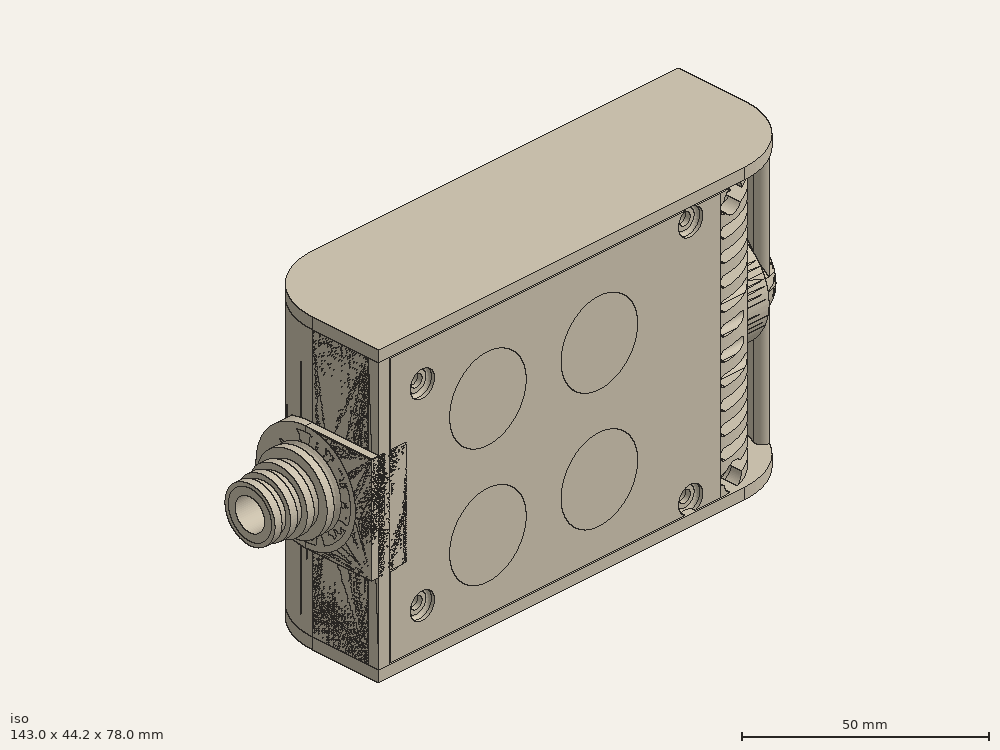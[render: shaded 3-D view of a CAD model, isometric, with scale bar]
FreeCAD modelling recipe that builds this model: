
FCSTD DOCUMENT  (FreeCAD 0.19R0.19.2)
Label: enclosure_137
License: All rights reserved
LicenseURL: http://en.wikipedia.org/wiki/All_rights_reserved
objects: Part::Feature×90, Part::Revolution×90, Part::MultiFuse×67, Sketcher::SketchObject×48, Part::Extrusion×36, Part::Cut×32, Part::Fillet×27, Part::Cylinder×26, Part::Box×19, App::MeasureDistance×4
note: 435 computed .brp shape members not serialized (recipe doc carries the construction recipe); baked Part::Feature solids carry a one-line shape summary decoded from their .brp

FEATURE [Sketcher::SketchObject] Sketch  label="topSketch"
  FullyConstrained = true
  sketch-geometry (20):
    g0: LineSegment StartX=5.21097e-06 StartY=3 StartZ=0 EndX=5.21097e-06 EndY=19 EndZ=0
    g1: ArcOfCircle CenterX=19 CenterY=19 CenterZ=0 NormalX=0 NormalY=0 NormalZ=1 AngleXU=0 Radius=19 StartAngle=1.5708 EndAngle=3.14159
    g2: ArcOfCircle CenterX=19 CenterY=19 CenterZ=0 NormalX=0 NormalY=0 NormalZ=1 AngleXU=0 Radius=16 StartAngle=1.5708 EndAngle=3.14159
    g3: LineSegment StartX=114 StartY=35 StartZ=0 EndX=19 EndY=35 EndZ=0
    g4: LineSegment StartX=5.21097e-06 StartY=3 StartZ=0 EndX=5.21097e-06 EndY=0 EndZ=0
    g5: LineSegment StartX=3 StartY=0 StartZ=0 EndX=5.21097e-06 EndY=0 EndZ=0
    g6: LineSegment StartX=3 StartY=19 StartZ=0 EndX=3 EndY=0 EndZ=0
    g7: LineSegment StartX=19 StartY=38 StartZ=0 EndX=124 EndY=38 EndZ=0
    g8: Circle CenterX=119 CenterY=35 CenterZ=0 NormalX=0 NormalY=0 NormalZ=1 AngleXU=0 Radius=1
    g9: Circle CenterX=121 CenterY=35 CenterZ=0 NormalX=0 NormalY=0 NormalZ=1 AngleXU=0 Radius=1
    g10: Circle CenterX=121 CenterY=33 CenterZ=0 NormalX=0 NormalY=0 NormalZ=1 AngleXU=0 Radius=1
    g11: BSplineCurve PolesCount=3 KnotsCount=2 Degree=2 IsPeriodic=0
    g12: GeomPoint X=119 Y=35 Z=0
    g13: GeomPoint X=121 Y=33 Z=0
    g14: LineSegment StartX=119 StartY=35 StartZ=0 EndX=114 EndY=35 EndZ=0
    g15: ArcOfCircle CenterX=105 CenterY=19 CenterZ=0 NormalX=0 NormalY=0 NormalZ=1 AngleXU=0 Radius=19 StartAngle=5.7297 EndAngle=6.28319
    g16: ArcOfCircle CenterX=105 CenterY=19 CenterZ=0 NormalX=0 NormalY=0 NormalZ=1 AngleXU=0 Radius=16 StartAngle=5.60905 EndAngle=6.28319
    g17: LineSegment StartX=121 StartY=33 StartZ=0 EndX=121 EndY=19 EndZ=0
    g18: LineSegment StartX=124 StartY=38 StartZ=0 EndX=124 EndY=19 EndZ=0
    g19: LineSegment StartX=117.5 StartY=9.01251 StartZ=0 EndX=121.163 EndY=9.0125 EndZ=0
  constraints (46):
    c: Vertical(g0)
    c: Block(g0)
    c: Coincident(g1,g0)
    c: Block(g1)
    c: Coincident(g2,g1)
    c: Block(g2)
    c: Coincident(g3,g2)
    c: Horizontal(g3)
    c: Tangent(g3,g2)
    c: Coincident(g4,g0)
    c: Distance(g4) = 3
    c: Vertical(g4)
    c: Coincident(g5,g4)
    c: Horizontal(g5)
    c: Coincident(g6,g2)
    c: Coincident(g6,g5)
    c: Vertical(g6)
    c: Horizontal(g7)
    c: Distance(g7) = 105
    c: Coincident(g7,g1)
    c: Block(g3)
    c: Weight(g8) = 1
    c: Equal(g8,g9)
    c: Equal(g8,g10)
    c: InternalAlignment(g8,g11)
    c: InternalAlignment(g9,g11)
    c: InternalAlignment(g10,g11)
    c: InternalAlignment(g12,g11)
    c: InternalAlignment(g13,g11)
    c: Block(g11)
    c: Coincident(g14,g11)
    c: Coincident(g14,g3)
    c: Horizontal(g14)
    c: Block(g15)
    c: Coincident(g16,g15)
    c: Block(g16)
    c: Coincident(g17,g11)
    c: Coincident(g17,g16)
    c: Vertical(g17)
    c: Distance(g17) = 14
    c: Coincident(g18,g7)
    c: Coincident(g18,g15)
    c: Vertical(g18)
    c: Distance(g18) = 19
    c: Coincident(g19,g16)
    c: Coincident(g19,g15)
FEATURE [Sketcher::SketchObject] Sketch001  label="bottomSketch"
  FullyConstrained = true
  sketch-geometry (32):
    g0: LineSegment StartX=3.3 StartY=-6.03275e-07 StartZ=0 EndX=98 EndY=-6.03275e-07 EndZ=0
    g1: ArcOfCircle CenterX=98 CenterY=19 CenterZ=0 NormalX=0 NormalY=0 NormalZ=1 AngleXU=0 Radius=19 StartAngle=4.71239 EndAngle=5.71103
    g2: LineSegment StartX=6.3 StartY=8 StartZ=0 EndX=3.3 EndY=8 EndZ=0
    g3: LineSegment StartX=3.3 StartY=8 StartZ=0 EndX=3.3 EndY=-6.03275e-07 EndZ=0
    g4: ArcOfCircle CenterX=8.3 CenterY=5 CenterZ=0 NormalX=0 NormalY=0 NormalZ=1 AngleXU=0 Radius=2 StartAngle=3.14159 EndAngle=4.71239
    g5: LineSegment StartX=6.3 StartY=8 StartZ=0 EndX=6.3 EndY=5 EndZ=0
    g6: ArcOfCircle CenterX=98 CenterY=19 CenterZ=0 NormalX=0 NormalY=0 NormalZ=1 AngleXU=0 Radius=12.7 StartAngle=4.71239 EndAngle=6.28319
    g7: LineSegment StartX=94.7 StartY=3 StartZ=0 EndX=8.3 EndY=3 EndZ=0
    g8-g12: Circle x5 (B-spline internal-alignment scaffolding for g13; pole/knot coordinates omitted)
    g13: BSplineCurve PolesCount=5 KnotsCount=3 Degree=3 IsPeriodic=0
    g14: GeomPoint X=98 Y=6.3 Z=0
    g15: GeomPoint X=96.3938 Y=4.71946 Z=0
    g16: GeomPoint X=94.7 Y=3 Z=0
    g17-g23: Circle x7 (B-spline internal-alignment scaffolding for g24; pole/knot coordinates omitted)
    g24: BSplineCurve PolesCount=7 KnotsCount=5 Degree=3 IsPeriodic=0
    g25-g29: GeomPoint x5 (B-spline internal-alignment scaffolding for g24; pole/knot coordinates omitted)
    g30: ArcOfCircle CenterX=98 CenterY=19 CenterZ=0 NormalX=0 NormalY=0 NormalZ=1 AngleXU=0 Radius=15.7 StartAngle=5.81226 EndAngle=6.28319
    g31: LineSegment StartX=110.7 StartY=19 StartZ=0 EndX=113.7 EndY=19 EndZ=0
  constraints (41):
    c: Horizontal(g0)
    c: Coincident(g1,g0)
    c: Block(g1)
    c: Horizontal(g2)
    c: Distance(g2) = 3
    c: Coincident(g3,g2)
    c: Vertical(g3)
    c: Coincident(g3,g0)
    c: Block(g4)
    c: Block(g2)
    c: Coincident(g5,g2)
    c: Coincident(g5,g4)
    c: Vertical(g5)
    c: Coincident(g6,g1)
    c: Block(g6)
    c: Coincident(g7,g4)
    c: Horizontal(g7)
    c: Block(g0)
    c: Block(g7)
    c: Block(g3)
    c: Coincident(g13,g6)
    c: Weight(g8) = 1
    c: Equal(g8, g9-g12) x4
    c: Coincident(g13,g7)
    c: InternalAlignment(g8-g12 -> g13) x5
    c: InternalAlignment(g14,g13)
    c: InternalAlignment(g15,g13)
    c: InternalAlignment(g16,g13)
    c: Block(g13)
    c: Weight(g17) = 1
    c: Equal(g17, g18-g23) x6
    c: Coincident(g24,g1)
    c: InternalAlignment(g17-g23 -> g24) x7
    c: InternalAlignment(g25-g29 -> g24) x5
    c: Block(g24)
    c: Coincident(g30,g24)
    c: Coincident(g31,g6)
    c: Coincident(g31,g30)
    c: Horizontal(g31)
    c: Block(g31)
    c: Block(g30)
FEATURE [Part::Extrusion] Extrude  label="top"
  Base = -> Sketch
  Dir = (0,0,1)
  DirMode = 2
  FaceMakerClass = Part::FaceMakerBullseye
  LengthFwd = 72
  LengthRev = 0
  Solid = true
  Symmetric = false
FEATURE [Part::Extrusion] Extrude001  label="bottom"
  Base = -> Sketch001
  Dir = (0,0,1)
  DirMode = 2
  FaceMakerClass = Part::FaceMakerBullseye
  LengthFwd = 71.4
  LengthRev = 0
  Placement = pos=(0,0,0.3) rot=(0,0,1;0rad)
  Solid = true
  Symmetric = false
FEATURE [Sketcher::SketchObject] Sketch002  label="topSketch001"
  FullyConstrained = true
  sketch-geometry (6):
    g0: ArcOfCircle CenterX=19 CenterY=19 CenterZ=0 NormalX=0 NormalY=0 NormalZ=1 AngleXU=0 Radius=19 StartAngle=1.5708 EndAngle=3.14159
    g1: LineSegment StartX=5.22862e-06 StartY=19 StartZ=0 EndX=5.22862e-06 EndY=1.19904e-11 EndZ=0
    g2: LineSegment StartX=19 StartY=38 StartZ=0 EndX=124 EndY=38 EndZ=0
    g3: LineSegment StartX=5.22862e-06 StartY=1.19904e-11 StartZ=0 EndX=105 EndY=1.19904e-11 EndZ=0
    g4: ArcOfCircle CenterX=105 CenterY=19 CenterZ=0 NormalX=0 NormalY=0 NormalZ=1 AngleXU=0 Radius=19 StartAngle=4.71239 EndAngle=6.28319
    g5: LineSegment StartX=124 StartY=38 StartZ=0 EndX=124 EndY=19 EndZ=0
  constraints (16):
    c: Block(g0)
    c: Coincident(g1,g0)
    c: Vertical(g1)
    c: Horizontal(g2)
    c: Distance(g2) = 105
    c: Coincident(g2,g0)
    c: Distance(g1) = 19
    c: Coincident(g3,g1)
    c: Horizontal(g3)
    c: Distance(g3) = 105
    c: Block(g4)
    c: Coincident(g4,g3)
    c: Coincident(g5,g2)
    c: Coincident(g5,g4)
    c: Vertical(g5)
    c: Distance(g5) = 19
FEATURE [Part::Extrusion] Extrude002  label="sideA"
  Base = -> Sketch002
  Dir = (0,0,1)
  DirMode = 2
  FaceMakerClass = Part::FaceMakerBullseye
  LengthFwd = 3
  LengthRev = 0
  Placement = pos=(0,0,-3) rot=(0,0,1;0rad)
  Solid = true
  Symmetric = false
FEATURE [Sketcher::SketchObject] Sketch003  label="topSketch002"
  FullyConstrained = true
  sketch-geometry (6):
    g0: LineSegment StartX=19 StartY=38 StartZ=0 EndX=117 EndY=38 EndZ=0
    g1: ArcOfCircle CenterX=19 CenterY=19 CenterZ=0 NormalX=0 NormalY=0 NormalZ=1 AngleXU=0 Radius=19 StartAngle=1.5708 EndAngle=3.14159
    g2: LineSegment StartX=117 StartY=38 StartZ=0 EndX=117 EndY=19 EndZ=0
    g3: LineSegment StartX=98 StartY=1.0161e-12 StartZ=0 EndX=5.22862e-06 EndY=1.0161e-12 EndZ=0
    g4: LineSegment StartX=5.22862e-06 StartY=19 StartZ=0 EndX=5.22862e-06 EndY=1.0161e-12 EndZ=0
    g5: ArcOfCircle CenterX=98 CenterY=19 CenterZ=0 NormalX=0 NormalY=0 NormalZ=1 AngleXU=0 Radius=19 StartAngle=4.71239 EndAngle=6.28319
  constraints (16):
    c: Horizontal(g0)
    c: Distance(g0) = 98
    c: Coincident(g1,g0)
    c: Block(g1)
    c: Coincident(g2,g0)
    c: Vertical(g2)
    c: Distance(g2) = 19
    c: Horizontal(g3)
    c: Coincident(g4,g1)
    c: Vertical(g4)
    c: Coincident(g3,g4)
    c: Block(g3)
    c: Coincident(g5,g2)
    c: Coincident(g5,g3)
    c: Block(g0)
    c: Block(g5)
FEATURE [Sketcher::SketchObject] Sketch004
  FullyConstrained = true
  MapMode = 3
  Placement = pos=(0,0,0) rot=(1,0,0;1.5708rad)
  Support = -> [Extrude]
  sketch-geometry (8):
    g0: Circle CenterX=80.351 CenterY=-67.6202 CenterZ=0 NormalX=0 NormalY=0 NormalZ=1 AngleXU=0 Radius=2
    g1: Circle CenterX=80.351 CenterY=-67.6202 CenterZ=0 NormalX=0 NormalY=0 NormalZ=1 AngleXU=0 Radius=3
    g2: Circle CenterX=80.351 CenterY=-4.92017 CenterZ=0 NormalX=0 NormalY=0 NormalZ=1 AngleXU=0 Radius=2
    g3: Circle CenterX=80.351 CenterY=-4.92017 CenterZ=0 NormalX=0 NormalY=0 NormalZ=1 AngleXU=0 Radius=3
    g4: Circle CenterX=23.851 CenterY=-4.92017 CenterZ=0 NormalX=0 NormalY=0 NormalZ=1 AngleXU=0 Radius=2
    g5: Circle CenterX=23.851 CenterY=-4.92017 CenterZ=0 NormalX=0 NormalY=0 NormalZ=1 AngleXU=0 Radius=3
    g6: Circle CenterX=23.851 CenterY=-67.6202 CenterZ=0 NormalX=0 NormalY=0 NormalZ=1 AngleXU=0 Radius=2
    g7: Circle CenterX=23.851 CenterY=-67.6202 CenterZ=0 NormalX=0 NormalY=0 NormalZ=1 AngleXU=0 Radius=3
  constraints (8):
    c: Block(g3)
    c: Block(g2)
    c: Block(g1)
    c: Block(g0)
    c: Block(g6)
    c: Block(g7)
    c: Block(g4)
    c: Block(g5)
FEATURE [Part::Extrusion] Extrude004
  Base = -> Sketch004
  Dir = (0,-1,2e-16)
  DirMode = 2
  FaceMakerClass = Part::FaceMakerBullseye
  LengthFwd = 6
  LengthRev = 0
  Placement = pos=(0,9,0) rot=(0,0,1;0rad)
  Solid = true
  Symmetric = false
FEATURE [Sketcher::SketchObject] Sketch005
  FullyConstrained = true
  MapMode = 3
  Placement = pos=(0,0,0) rot=(1,0,0;1.5708rad)
  Support = -> [Extrude]
  sketch-geometry (8):
    g0: Circle CenterX=80.351 CenterY=-67.6202 CenterZ=0 NormalX=0 NormalY=0 NormalZ=1 AngleXU=0 Radius=3
    g1: Circle CenterX=80.351 CenterY=-4.92017 CenterZ=0 NormalX=0 NormalY=0 NormalZ=1 AngleXU=0 Radius=3
    g2: Circle CenterX=23.851 CenterY=-4.92017 CenterZ=0 NormalX=0 NormalY=0 NormalZ=1 AngleXU=0 Radius=3
    g3: Circle CenterX=23.851 CenterY=-67.6202 CenterZ=0 NormalX=0 NormalY=0 NormalZ=1 AngleXU=0 Radius=3
    g4: Circle CenterX=23.851 CenterY=-67.6202 CenterZ=0 NormalX=0 NormalY=0 NormalZ=1 AngleXU=0 Radius=5
    g5: Circle CenterX=80.351 CenterY=-67.6202 CenterZ=0 NormalX=0 NormalY=0 NormalZ=1 AngleXU=0 Radius=5
    g6: Circle CenterX=23.851 CenterY=-4.92017 CenterZ=0 NormalX=0 NormalY=0 NormalZ=1 AngleXU=0 Radius=5
    g7: Circle CenterX=80.351 CenterY=-4.92017 CenterZ=0 NormalX=0 NormalY=0 NormalZ=1 AngleXU=0 Radius=5
  constraints (8):
    c: Block(g1)
    c: Block(g0)
    c: Block(g3)
    c: Block(g2)
    c: Block(g5)
    c: Block(g4)
    c: Block(g6)
    c: Block(g7)
FEATURE [Part::Extrusion] Extrude005
  Base = -> Sketch005
  Dir = (0,-1,2e-16)
  DirMode = 2
  FaceMakerClass = Part::FaceMakerBullseye
  LengthFwd = 2
  LengthRev = 0
  Solid = true
  Symmetric = false
FEATURE [Sketcher::SketchObject] Sketch006
  FullyConstrained = true
  MapMode = 3
  Placement = pos=(0,0,0) rot=(1,0,0;1.5708rad)
  sketch-geometry (8):
    g0: Circle CenterX=80.351 CenterY=-67.6202 CenterZ=0 NormalX=0 NormalY=0 NormalZ=1 AngleXU=0 Radius=3
    g1: Circle CenterX=80.351 CenterY=-4.92017 CenterZ=0 NormalX=0 NormalY=0 NormalZ=1 AngleXU=0 Radius=3
    g2: Circle CenterX=23.851 CenterY=-4.92017 CenterZ=0 NormalX=0 NormalY=0 NormalZ=1 AngleXU=0 Radius=3
    g3: Circle CenterX=23.851 CenterY=-67.6202 CenterZ=0 NormalX=0 NormalY=0 NormalZ=1 AngleXU=0 Radius=3
    g4: Circle CenterX=23.851 CenterY=-67.6202 CenterZ=0 NormalX=0 NormalY=0 NormalZ=1 AngleXU=0 Radius=5
    g5: Circle CenterX=80.351 CenterY=-67.6202 CenterZ=0 NormalX=0 NormalY=0 NormalZ=1 AngleXU=0 Radius=5
    g6: Circle CenterX=23.851 CenterY=-4.92017 CenterZ=0 NormalX=0 NormalY=0 NormalZ=1 AngleXU=0 Radius=5
    g7: Circle CenterX=80.351 CenterY=-4.92017 CenterZ=0 NormalX=0 NormalY=0 NormalZ=1 AngleXU=0 Radius=5
  constraints (8):
    c: Block(g1)
    c: Block(g0)
    c: Block(g3)
    c: Block(g2)
    c: Block(g5)
    c: Block(g4)
    c: Block(g6)
    c: Block(g7)
FEATURE [Part::Extrusion] Extrude007
  Base = -> Sketch006
  Dir = (0,-1,2e-16)
  DirMode = 2
  FaceMakerClass = Part::FaceMakerBullseye
  LengthFwd = 2
  LengthRev = 0
  Solid = true
  Symmetric = false
FEATURE [Part::Fillet] Fillet
  Base = -> Extrude007
  Edges = 4 edges r=1.99: [Edge6,Edge12,Edge18,Edge24]
FEATURE [Part::Cut] Cut
  Base = -> Extrude005
  Placement = pos=(0,5,0) rot=(0,0,1;0rad)
  Tool = -> Fillet
FEATURE [Part::MultiFuse] Fusion  label="pCBScrews"
  Placement = pos=(-2.5,0,72.3) rot=(0,0,1;0rad)
  Shapes = -> [Extrude004,Cut]
FEATURE [App::MeasureDistance] Distance  label="Distance: 0.69 mm"
  Distance = 0.685967
  P1 = (24.0138,2.9647,0.3)
  P2 = (23.8901,3,-0.373787)
FEATURE [App::MeasureDistance] Distance001  label="Distance: 0.53 mm"
  Distance = 0.533607
  P1 = (80.2939,3,72.2334)
  P2 = (80.281,2.99661,71.7)
FEATURE [Part::Fillet] Fillet001
  Base = -> Extrude001
  Edges = 1 edges r=2.4: [Edge17]
FEATURE [Part::Fillet] Fillet002  label="bottom001"
  Base = -> Fillet001
  Edges = 1 edges r=2.4: [Edge36]
FEATURE [Part::Fillet] Fillet003  label="top001"
  Base = -> Extrude
  Edges = 1 edges r=2: [Edge1]
FEATURE [Sketcher::SketchObject] Sketch007
  FullyConstrained = true
  sketch-geometry (16):
    g0: LineSegment StartX=4 StartY=0 StartZ=0 EndX=4 EndY=2.4 EndZ=0
    g1: LineSegment StartX=4 StartY=2.4 StartZ=0 EndX=7 EndY=2.4 EndZ=0
    g2: LineSegment StartX=4 StartY=0 StartZ=0 EndX=5.7 EndY=0 EndZ=0
    g3: LineSegment StartX=5.7 StartY=0 StartZ=0 EndX=5.7 EndY=-5.6 EndZ=0
    g4-g8: Circle x5 (B-spline internal-alignment scaffolding for g9; pole/knot coordinates omitted)
    g9: BSplineCurve PolesCount=5 KnotsCount=3 Degree=3 IsPeriodic=0
    g10: GeomPoint X=7 Y=2.4 Z=0
    g11: GeomPoint X=10.4582 Y=-1.55472 Z=0
    g12: GeomPoint X=14 Y=-5.6 Z=0
    g13: LineSegment StartX=14 StartY=-5.6 StartZ=0 EndX=14 EndY=-14.1 EndZ=0
    g14: LineSegment StartX=14 StartY=-14.1 StartZ=0 EndX=6.5 EndY=-14.1 EndZ=0
    g15: LineSegment StartX=5.7 StartY=-5.6 StartZ=0 EndX=6.5 EndY=-14.1 EndZ=0
  constraints (28):
    c: Distance(g0) = 2.4
    c: Vertical(g0)
    c: Block(g0)
    c: Coincident(g1,g0)
    c: Horizontal(g1)
    c: Distance(g1) = 3
    c: Coincident(g2,g0)
    c: Horizontal(g2)
    c: Distance(g2) = 1.7
    c: Coincident(g3,g2)
    c: Vertical(g3)
    c: Distance(g3) = 5.6
    c: Coincident(g9,g1)
    c: Weight(g4) = 1
    c: Equal(g4, g5-g8) x4
    c: InternalAlignment(g4-g8 -> g9) x5
    c: InternalAlignment(g10,g9)
    c: InternalAlignment(g11,g9)
    c: InternalAlignment(g12,g9)
    c: Block(g9)
    c: Coincident(g13,g9)
    c: Vertical(g13)
    c: Distance(g13) = 8.5
    c: Coincident(g14,g13)
    c: Horizontal(g14)
    c: Distance(g14) = 7.5
    c: Coincident(g15,g3)
    c: Coincident(g15,g14)
FEATURE [Part::Feature] Face
  shape: bbox 10 x 16.5 x 2e-07 mm, 1 faces, 0 solids (baked)
FEATURE [Part::Revolution] Revolve  label="plugHousing"
  Angle = 360
  Axis = (0,1,0)
  Base = (0,0,0)
  FaceMakerClass = Part::FaceMakerBullseye
  Placement = pos=(0,0,36.15) rot=(0,0,1;0rad)
  Solid = false
  Source = -> Face
  Symmetric = false
FEATURE [Part::Feature] Face001
  shape: bbox 10 x 16.5 x 2e-07 mm, 1 faces, 0 solids (baked)
FEATURE [Part::Revolution] Revolve001  label="plugHousing001"
  Angle = 360
  Axis = (0,1,0)
  Base = (0,0,0)
  FaceMakerClass = Part::FaceMakerBullseye
  Placement = pos=(0,0,36.15) rot=(0,0,1;0rad)
  Solid = false
  Source = -> Face001
  Symmetric = false
FEATURE [Part::MultiFuse] Fusion001  label="plugHousing002"
  Placement = pos=(0,0,0) rot=(0,0,1;1.5708rad)
  Shapes = -> [Revolve001,Revolve]
FEATURE [Part::Feature] Face002
  shape: bbox 10 x 16.5 x 2e-07 mm, 1 faces, 0 solids (baked)
FEATURE [Part::Revolution] Revolve003  label="plugHousing005"
  Angle = 360
  Axis = (0,1,0)
  Base = (0,0,0)
  FaceMakerClass = Part::FaceMakerBullseye
  Placement = pos=(0,0,36.15) rot=(0,0,1;0rad)
  Solid = false
  Source = -> Face002
  Symmetric = false
FEATURE [Part::Feature] Face003
  shape: bbox 10 x 16.5 x 2e-07 mm, 1 faces, 0 solids (baked)
FEATURE [Part::Revolution] Revolve002  label="plugHousing003"
  Angle = 360
  Axis = (0,1,0)
  Base = (0,0,0)
  FaceMakerClass = Part::FaceMakerBullseye
  Placement = pos=(0,0,36.15) rot=(0,0,1;0rad)
  Solid = false
  Source = -> Face003
  Symmetric = false
FEATURE [Part::MultiFuse] Fusion002  label="plugHousing004"
  Placement = pos=(0,0,0) rot=(0,0,1;1.5708rad)
  Shapes = -> [Revolve002,Revolve003]
FEATURE [Part::MultiFuse] Fusion003  label="plugHousing006"
  Placement = pos=(0,19,0) rot=(0,0,1;3.14159rad)
  Shapes = -> [Fusion002,Fusion001]
FEATURE [Part::Feature] Face004
  shape: bbox 10 x 16.5 x 2e-07 mm, 1 faces, 0 solids (baked)
FEATURE [Part::Revolution] Revolve006  label="plugHousing010"
  Angle = 360
  Axis = (0,1,0)
  Base = (0,0,0)
  FaceMakerClass = Part::FaceMakerBullseye
  Placement = pos=(0,0,36.15) rot=(0,0,1;0rad)
  Solid = false
  Source = -> Face004
  Symmetric = false
FEATURE [Part::Feature] Face005
  shape: bbox 10 x 16.5 x 2e-07 mm, 1 faces, 0 solids (baked)
FEATURE [Part::Revolution] Revolve007  label="plugHousing011"
  Angle = 360
  Axis = (0,1,0)
  Base = (0,0,0)
  FaceMakerClass = Part::FaceMakerBullseye
  Placement = pos=(0,0,36.15) rot=(0,0,1;0rad)
  Solid = false
  Source = -> Face005
  Symmetric = false
FEATURE [Part::Feature] Face006
  shape: bbox 10 x 16.5 x 2e-07 mm, 1 faces, 0 solids (baked)
FEATURE [Part::Revolution] Revolve004  label="plugHousing007"
  Angle = 360
  Axis = (0,1,0)
  Base = (0,0,0)
  FaceMakerClass = Part::FaceMakerBullseye
  Placement = pos=(0,0,36.15) rot=(0,0,1;0rad)
  Solid = false
  Source = -> Face006
  Symmetric = false
FEATURE [Part::MultiFuse] Fusion004  label="plugHousing009"
  Placement = pos=(0,0,0) rot=(0,0,1;1.5708rad)
  Shapes = -> [Revolve004,Revolve007]
FEATURE [Part::Feature] Face007
  shape: bbox 10 x 16.5 x 2e-07 mm, 1 faces, 0 solids (baked)
FEATURE [Part::Revolution] Revolve005  label="plugHousing008"
  Angle = 360
  Axis = (0,1,0)
  Base = (0,0,0)
  FaceMakerClass = Part::FaceMakerBullseye
  Placement = pos=(0,0,36.15) rot=(0,0,1;0rad)
  Solid = false
  Source = -> Face007
  Symmetric = false
FEATURE [Part::MultiFuse] Fusion005  label="plugHousing012"
  Placement = pos=(0,0,0) rot=(0,0,1;1.5708rad)
  Shapes = -> [Revolve006,Revolve005]
FEATURE [Part::MultiFuse] Fusion006  label="plugHousing013"
  Placement = pos=(0,19,0) rot=(0,0,1;3.14159rad)
  Shapes = -> [Fusion005,Fusion004]
FEATURE [Part::MultiFuse] Fusion007  label="plugHousing014"
  Placement = pos=(122.621,0,-0.15) rot=(0,0,1;0rad)
  Shapes = -> [Fusion003,Fusion006]
FEATURE [Part::Cylinder] Cylinder002
  Angle = 360
  AttacherType = Attacher::AttachEngine3D
  Height = 20
  Placement = pos=(0,0,36.15) rot=(0,0,1;0rad)
  Radius = 4
FEATURE [Part::Cylinder] Cylinder003
  Angle = 360
  AttacherType = Attacher::AttachEngine3D
  Height = 10
  Placement = pos=(0,0,36.15) rot=(0,0,1;0rad)
  Radius = 4
FEATURE [Part::MultiFuse] Fusion009  label="removeToCreateHoleForPlugHousing"
  Placement = pos=(70,19,36.15) rot=(0,1,0;1.5708rad)
  Shapes = -> [Cylinder002,Cylinder003]
FEATURE [Part::Cylinder] Cylinder004
  Angle = 360
  AttacherType = Attacher::AttachEngine3D
  Height = 20
  Placement = pos=(0,0,36.15) rot=(0,0,1;0rad)
  Radius = 4
FEATURE [Part::Cylinder] Cylinder005
  Angle = 360
  AttacherType = Attacher::AttachEngine3D
  Height = 10
  Placement = pos=(0,0,36.15) rot=(0,0,1;0rad)
  Radius = 4
FEATURE [Part::MultiFuse] Fusion010  label="removeToCreateHoleForPlugHousing001"
  Placement = pos=(70,19,36.15) rot=(0,1,0;1.5708rad)
  Shapes = -> [Cylinder004,Cylinder005]
FEATURE [Part::Cut] Cut001
  Base = -> Fillet003
  Tool = -> Fusion010
FEATURE [Part::Cut] Cut002  label="Bottom"
  Base = -> Fillet002
  Tool = -> Fusion009
FEATURE [Part::Feature] Face008
  shape: bbox 10 x 16.5 x 2e-07 mm, 1 faces, 0 solids (baked)
FEATURE [Part::Revolution] Revolve011  label="plugHousing021"
  Angle = 360
  Axis = (0,1,0)
  Base = (0,0,0)
  FaceMakerClass = Part::FaceMakerBullseye
  Placement = pos=(0,0,36.15) rot=(0,0,1;0rad)
  Solid = false
  Source = -> Face008
  Symmetric = false
FEATURE [Part::Feature] Face009
  shape: bbox 10 x 16.5 x 2e-07 mm, 1 faces, 0 solids (baked)
FEATURE [Part::Revolution] Revolve012  label="plugHousing022"
  Angle = 360
  Axis = (0,1,0)
  Base = (0,0,0)
  FaceMakerClass = Part::FaceMakerBullseye
  Placement = pos=(0,0,36.15) rot=(0,0,1;0rad)
  Solid = false
  Source = -> Face009
  Symmetric = false
FEATURE [Part::Feature] Face010 .. Face013  x4 (patterned run collapsed; names and placements below)
  shape: bbox 10 x 16.5 x 2e-07 mm, 1 faces, 0 solids (baked)
FEATURE [Part::Revolution] Revolve015  label="plugHousing027"
  Angle = 360
  Axis = (0,1,0)
  Base = (0,0,0)
  FaceMakerClass = Part::FaceMakerBullseye
  Placement = pos=(0,0,36.15) rot=(0,0,1;0rad)
  Solid = false
  Source = -> Face013
  Symmetric = false
FEATURE [Part::Feature] Face014
  shape: bbox 10 x 16.5 x 2e-07 mm, 1 faces, 0 solids (baked)
FEATURE [Part::Feature] Face015
  shape: bbox 10 x 16.5 x 2e-07 mm, 1 faces, 0 solids (baked)
FEATURE [Part::Feature] Face016
  shape: bbox 10 x 16.5 x 2e-07 mm, 1 faces, 0 solids (baked)
FEATURE [Part::Revolution] Revolve019  label="plugHousing033"
  Angle = 360
  Axis = (0,1,0)
  Base = (0,0,0)
  FaceMakerClass = Part::FaceMakerBullseye
  Placement = pos=(0,0,36.15) rot=(0,0,1;0rad)
  Solid = false
  Source = -> Face016
  Symmetric = false
FEATURE [Part::Feature] Face017
  shape: bbox 10 x 16.5 x 2e-07 mm, 1 faces, 0 solids (baked)
FEATURE [Part::Revolution] Revolve020  label="plugHousing034"
  Angle = 360
  Axis = (0,1,0)
  Base = (0,0,0)
  FaceMakerClass = Part::FaceMakerBullseye
  Placement = pos=(0,0,36.15) rot=(0,0,1;0rad)
  Solid = false
  Source = -> Face017
  Symmetric = false
FEATURE [Part::Feature] Face018
  shape: bbox 10 x 16.5 x 2e-07 mm, 1 faces, 0 solids (baked)
FEATURE [Part::Revolution] Revolve016  label="plugHousing030"
  Angle = 360
  Axis = (0,1,0)
  Base = (0,0,0)
  FaceMakerClass = Part::FaceMakerBullseye
  Placement = pos=(0,0,36.15) rot=(0,0,1;0rad)
  Solid = false
  Source = -> Face018
  Symmetric = false
FEATURE [Part::MultiFuse] Fusion020  label="plugHousing038"
  Placement = pos=(0,0,0) rot=(0,0,1;1.5708rad)
  Shapes = -> [Revolve016,Revolve020]
FEATURE [Part::Feature] Face019
  shape: bbox 10 x 16.5 x 2e-07 mm, 1 faces, 0 solids (baked)
FEATURE [Part::Feature] Face020
  shape: bbox 10 x 16.5 x 2e-07 mm, 1 faces, 0 solids (baked)
FEATURE [Part::Revolution] Revolve017  label="plugHousing031"
  Angle = 360
  Axis = (0,1,0)
  Base = (0,0,0)
  FaceMakerClass = Part::FaceMakerBullseye
  Placement = pos=(0,0,36.15) rot=(0,0,1;0rad)
  Solid = false
  Source = -> Face020
  Symmetric = false
FEATURE [Part::MultiFuse] Fusion021  label="plugHousing039"
  Placement = pos=(0,0,0) rot=(0,0,1;1.5708rad)
  Shapes = -> [Revolve019,Revolve017]
FEATURE [Part::MultiFuse] Fusion023  label="plugHousing041"
  Placement = pos=(0,19,0) rot=(0,0,1;3.14159rad)
  Shapes = -> [Fusion021,Fusion020]
FEATURE [Part::Revolution] Revolve022  label="plugHousing043"
  Angle = 360
  Axis = (0,1,0)
  Base = (0,0,0)
  FaceMakerClass = Part::FaceMakerBullseye
  Placement = pos=(0,0,36.15) rot=(0,0,1;0rad)
  Solid = false
  Source = -> Face019
  Symmetric = false
FEATURE [Part::Feature] Face021
  shape: bbox 10 x 16.5 x 2e-07 mm, 1 faces, 0 solids (baked)
FEATURE [Part::Revolution] Revolve023  label="plugHousing044"
  Angle = 360
  Axis = (0,1,0)
  Base = (0,0,0)
  FaceMakerClass = Part::FaceMakerBullseye
  Placement = pos=(0,0,36.15) rot=(0,0,1;0rad)
  Solid = false
  Source = -> Face021
  Symmetric = false
FEATURE [Part::Feature] Face022
  shape: bbox 10 x 16.5 x 2e-07 mm, 1 faces, 0 solids (baked)
FEATURE [Part::Revolution] Revolve018  label="plugHousing032"
  Angle = 360
  Axis = (0,1,0)
  Base = (0,0,0)
  FaceMakerClass = Part::FaceMakerBullseye
  Placement = pos=(0,0,36.15) rot=(0,0,1;0rad)
  Solid = false
  Source = -> Face022
  Symmetric = false
FEATURE [Part::MultiFuse] Fusion022  label="plugHousing040"
  Placement = pos=(0,0,0) rot=(0,0,1;1.5708rad)
  Shapes = -> [Revolve018,Revolve023]
FEATURE [Part::Feature] Face023
  shape: bbox 10 x 16.5 x 2e-07 mm, 1 faces, 0 solids (baked)
FEATURE [Part::Revolution] Revolve021  label="plugHousing035"
  Angle = 360
  Axis = (0,1,0)
  Base = (0,0,0)
  FaceMakerClass = Part::FaceMakerBullseye
  Placement = pos=(0,0,36.15) rot=(0,0,1;0rad)
  Solid = false
  Source = -> Face023
  Symmetric = false
FEATURE [Part::MultiFuse] Fusion018  label="plugHousing036"
  Placement = pos=(0,0,0) rot=(0,0,1;1.5708rad)
  Shapes = -> [Revolve022,Revolve021]
FEATURE [Part::MultiFuse] Fusion019  label="plugHousing037"
  Placement = pos=(0,19,0) rot=(0,0,1;3.14159rad)
  Shapes = -> [Fusion018,Fusion022]
FEATURE [Part::MultiFuse] Fusion024  label="plugHousing042"
  Placement = pos=(122.621,0,-0.15) rot=(0,0,1;0rad)
  Shapes = -> [Fusion023,Fusion019]
FEATURE [Part::Cylinder] Cylinder006
  Angle = 360
  AttacherType = Attacher::AttachEngine3D
  Height = 20
  Placement = pos=(0,0,36.15) rot=(0,0,1;0rad)
  Radius = 14.3
FEATURE [Part::Cylinder] Cylinder007
  Angle = 360
  AttacherType = Attacher::AttachEngine3D
  Height = 10
  Placement = pos=(0,0,36.15) rot=(0,0,1;0rad)
  Radius = 4
FEATURE [Part::MultiFuse] Fusion026  label="removeToCreteHoleForPlugHousing"
  Placement = pos=(70,19,36) rot=(0,1,0;1.5708rad)
  Shapes = -> [Cylinder006,Cylinder007]
FEATURE [Part::Box] Box001  label="Cube001"
  AttacherType = Attacher::AttachEngine3D
  Height = 28
  Length = 3
  Placement = pos=(110.7,19,22) rot=(0,0,1;0rad)
  Width = 15.7
FEATURE [Part::Cut] Cut003  label="top002"
  Base = -> Cut001
  Tool = -> Fusion007
FEATURE [Part::Revolution] Revolve008  label="plugHousing015"
  Angle = 360
  Axis = (0,1,0)
  Base = (0,0,0)
  FaceMakerClass = Part::FaceMakerBullseye
  Placement = pos=(0,0,36.15) rot=(0,0,1;0rad)
  Solid = false
  Source = -> Face010
  Symmetric = false
FEATURE [Part::MultiFuse] Fusion013  label="plugHousing020"
  Placement = pos=(0,0,0) rot=(0,0,1;1.5708rad)
  Shapes = -> [Revolve008,Revolve012]
FEATURE [Part::Cut] Cut004  label="top003"
  Base = -> Cut003
  Placement = pos=(1,0,0) rot=(0,0,1;0rad)
  Tool = -> Fusion026
FEATURE [Part::Cylinder] Cylinder008
  Angle = 360
  AttacherType = Attacher::AttachEngine3D
  Height = 20
  Placement = pos=(0,0,36.15) rot=(0,0,1;0rad)
  Radius = 10.3
FEATURE [Part::Cylinder] Cylinder009
  Angle = 360
  AttacherType = Attacher::AttachEngine3D
  Height = 10
  Placement = pos=(0,0,36.15) rot=(0,0,1;0rad)
  Radius = 4
FEATURE [Part::MultiFuse] Fusion027  label="removeToCreteHoleForPlugHousing001"
  Placement = pos=(70,19,36) rot=(0,1,0;1.5708rad)
  Shapes = -> [Cylinder008,Cylinder009]
FEATURE [Part::Cut] Cut005  label="plugHousingTab"
  Base = -> Box001
  Tool = -> Fusion027
FEATURE [Part::MultiFuse] Fusion028  label="plugHousing045"
  Shapes = -> [Fusion024,Cut005]
FEATURE [Part::Box] Box002  label="Cube002"
  AttacherType = Attacher::AttachEngine3D
  Height = 28.8
  Length = 3
  Placement = pos=(107.3,28,21.6) rot=(0,0,1;0rad)
  Width = 7
FEATURE [Part::Box] Box003  label="Cube003"
  AttacherType = Attacher::AttachEngine3D
  Height = 3
  Length = 6.4
  Placement = pos=(107.3,28,18.6) rot=(0,0,1;0rad)
  Width = 7
FEATURE [Part::Box] Box004  label="Cube004"
  AttacherType = Attacher::AttachEngine3D
  Height = 3
  Length = 6.4
  Placement = pos=(107.3,28,50.4) rot=(0,0,1;0rad)
  Width = 7
FEATURE [Part::MultiFuse] Fusion029  label="plugHousingBracketHolder"
  Shapes = -> [Box004,Box002,Box003]
FEATURE [Part::Cylinder] Cylinder010
  Angle = 360
  AttacherType = Attacher::AttachEngine3D
  Height = 20
  Placement = pos=(0,0,36.15) rot=(0,0,1;0rad)
  Radius = 14.3
FEATURE [Part::Cylinder] Cylinder011
  Angle = 360
  AttacherType = Attacher::AttachEngine3D
  Height = 10
  Placement = pos=(0,0,36.15) rot=(0,0,1;0rad)
  Radius = 4
FEATURE [Part::MultiFuse] Fusion030  label="removeToCreteHoleForPlugHousing002"
  Placement = pos=(70,19,36) rot=(0,1,0;1.5708rad)
  Shapes = -> [Cylinder010,Cylinder011]
FEATURE [Part::Cut] Cut006  label="plugHousingBracketHolder001"
  Base = -> Fusion029
  Tool = -> Fusion030
FEATURE [Part::Cylinder] Cylinder012
  Angle = 360
  AttacherType = Attacher::AttachEngine3D
  Height = 20
  Placement = pos=(0,0,36.15) rot=(0,0,1;0rad)
  Radius = 7
FEATURE [Part::Cylinder] Cylinder013
  Angle = 360
  AttacherType = Attacher::AttachEngine3D
  Height = 10
  Placement = pos=(0,0,36.15) rot=(0,0,1;0rad)
  Radius = 4
FEATURE [Part::MultiFuse] Fusion032  label="removeToCreteHoleForPlugHousing003"
  Placement = pos=(70,19,36) rot=(0,1,0;1.5708rad)
  Shapes = -> [Cylinder012,Cylinder013]
FEATURE [Part::Cut] Cut007  label="bottom002"
  Base = -> Cut002
  Tool = -> Fusion032
FEATURE [Sketcher::SketchObject] Sketch008
  FullyConstrained = true
  sketch-geometry (54):
    g0: LineSegment StartX=-4.2 StartY=0 StartZ=0 EndX=-6.2 EndY=0 EndZ=0
    g1: LineSegment StartX=-14 StartY=-18 StartZ=0 EndX=-14 EndY=-26.5 EndZ=0
    g2: LineSegment StartX=-4.2 StartY=0 StartZ=0 EndX=-4.2 EndY=-13.4877 EndZ=0
    g3: Circle CenterX=-4.2 CenterY=-13.4877 CenterZ=0 NormalX=0 NormalY=0 NormalZ=1 AngleXU=0 Radius=1
    g4: Circle CenterX=-4.2 CenterY=-26.5 CenterZ=0 NormalX=0 NormalY=0 NormalZ=1 AngleXU=0 Radius=1
    g5: Circle CenterX=-8.2 CenterY=-26.5 CenterZ=0 NormalX=0 NormalY=0 NormalZ=1 AngleXU=0 Radius=1
    g6: BSplineCurve PolesCount=3 KnotsCount=2 Degree=2 IsPeriodic=0
    g7: GeomPoint X=-4.2 Y=-13.4877 Z=0
    g8: GeomPoint X=-8.2 Y=-26.5 Z=0
    g9: LineSegment StartX=-14 StartY=-26.5 StartZ=0 EndX=-8.2 EndY=-26.5 EndZ=0
    g10: LineSegment StartX=-10.15 StartY=-12 StartZ=0 EndX=-10.15 EndY=-14 EndZ=0
    g11: LineSegment StartX=-12.8401 StartY=-16 StartZ=0 EndX=-10.1571 EndY=-16 EndZ=0
    g12: LineSegment StartX=-10.15 StartY=-14 StartZ=0 EndX=-8.70761 EndY=-14 EndZ=0
    g13: LineSegment StartX=-12.8401 StartY=-16 StartZ=0 EndX=-12.8401 EndY=-17.6958 EndZ=0
    g14: LineSegment StartX=-10.15 StartY=-12 StartZ=0 EndX=-7.79258 EndY=-12 EndZ=0
    g15: Circle CenterX=-6.2215 CenterY=-2 CenterZ=0 NormalX=0 NormalY=0 NormalZ=1 AngleXU=0 Radius=1
    g16: Circle CenterX=-6.22762 CenterY=-2.58724 CenterZ=0 NormalX=0 NormalY=0 NormalZ=1 AngleXU=0 Radius=1
    g17: Circle CenterX=-6.32538 CenterY=-4 CenterZ=0 NormalX=0 NormalY=0 NormalZ=1 AngleXU=0 Radius=1
    g18: BSplineCurve PolesCount=3 KnotsCount=2 Degree=2 IsPeriodic=0
    g19: GeomPoint X=-6.2215 Y=-2 Z=0
    g20: GeomPoint X=-6.32538 Y=-4 Z=0
    g21: Circle CenterX=-6.48644 CenterY=-5.99526 CenterZ=0 NormalX=0 NormalY=0 NormalZ=1 AngleXU=0 Radius=1
    g22: Circle CenterX=-6.58486 CenterY=-6.99526 CenterZ=0 NormalX=0 NormalY=0 NormalZ=1 AngleXU=0 Radius=1
    g23: Circle CenterX=-6.77343 CenterY=-8 CenterZ=0 NormalX=0 NormalY=0 NormalZ=1 AngleXU=0 Radius=1
    g24: BSplineCurve PolesCount=3 KnotsCount=2 Degree=2 IsPeriodic=0
    g25: GeomPoint X=-6.48644 Y=-5.99526 Z=0
    g26: GeomPoint X=-6.77343 Y=-8 Z=0
    g27: Circle CenterX=-7.19003 CenterY=-10 CenterZ=0 NormalX=0 NormalY=0 NormalZ=1 AngleXU=0 Radius=1
    g28: Circle CenterX=-7.44407 CenterY=-11.0915 CenterZ=0 NormalX=0 NormalY=0 NormalZ=1 AngleXU=0 Radius=1
    g29: Circle CenterX=-7.79258 CenterY=-12 CenterZ=0 NormalX=0 NormalY=0 NormalZ=1 AngleXU=0 Radius=1
    g30: BSplineCurve PolesCount=3 KnotsCount=2 Degree=2 IsPeriodic=0
    g31: GeomPoint X=-7.19003 Y=-10 Z=0
    g32: GeomPoint X=-7.79258 Y=-12 Z=0
    g33: Circle CenterX=-8.70761 CenterY=-14 CenterZ=0 NormalX=0 NormalY=0 NormalZ=1 AngleXU=0 Radius=1
    g34: Circle CenterX=-9.33087 CenterY=-15.1837 CenterZ=0 NormalX=0 NormalY=0 NormalZ=1 AngleXU=0 Radius=1
    g35: Circle CenterX=-10.1571 CenterY=-16 CenterZ=0 NormalX=0 NormalY=0 NormalZ=1 AngleXU=0 Radius=1
    g36: BSplineCurve PolesCount=3 KnotsCount=2 Degree=2 IsPeriodic=0
    g37: GeomPoint X=-8.70761 Y=-14 Z=0
    g38: GeomPoint X=-10.1571 Y=-16 Z=0
    g39: Circle CenterX=-12.8401 CenterY=-17.6958 CenterZ=0 NormalX=0 NormalY=0 NormalZ=1 AngleXU=0 Radius=1
    g40: Circle CenterX=-13.3521 CenterY=-17.9027 CenterZ=0 NormalX=0 NormalY=0 NormalZ=1 AngleXU=0 Radius=1
    g41: Circle CenterX=-14 CenterY=-18 CenterZ=0 NormalX=0 NormalY=0 NormalZ=1 AngleXU=0 Radius=1
    g42: BSplineCurve PolesCount=3 KnotsCount=2 Degree=2 IsPeriodic=0
    g43: GeomPoint X=-12.8401 Y=-17.6958 Z=0
    g44: GeomPoint X=-14 Y=-18 Z=0
    g45: LineSegment StartX=-6.2 StartY=0 StartZ=0 EndX=-7.2 EndY=0 EndZ=0
    g46: LineSegment StartX=-7.2 StartY=0 StartZ=0 EndX=-7.2 EndY=-2 EndZ=0
    g47: LineSegment StartX=-7.2 StartY=-2 StartZ=0 EndX=-6.2215 EndY=-2 EndZ=0
    g48: LineSegment StartX=-6.32538 StartY=-4 StartZ=0 EndX=-7.65538 EndY=-4 EndZ=0
    g49: LineSegment StartX=-7.65538 StartY=-4 StartZ=0 EndX=-7.65538 EndY=-5.99526 EndZ=0
    g50: LineSegment StartX=-7.65538 StartY=-5.99526 StartZ=0 EndX=-6.48644 EndY=-5.99526 EndZ=0
    g51: LineSegment StartX=-6.77343 StartY=-8 StartZ=0 EndX=-8.43343 EndY=-8 EndZ=0
    g52: LineSegment StartX=-8.43343 StartY=-8 StartZ=0 EndX=-8.43343 EndY=-10 EndZ=0
    g53: LineSegment StartX=-8.43343 StartY=-10 StartZ=0 EndX=-7.19003 EndY=-10 EndZ=0
  constraints (112):
    c: Horizontal(g0)
    c: Distance(g0) = 2
    c: Block(g0)
    c: Vertical(g1)
    c: Coincident(g2,g0)
    c: Vertical(g2)
    c: Block(g2)
    c: Coincident(g6,g2)
    c: Weight(g3) = 1
    c: Equal(g3,g4)
    c: Equal(g3,g5)
    c: InternalAlignment(g3,g6)
    c: InternalAlignment(g4,g6)
    c: InternalAlignment(g5,g6)
    c: InternalAlignment(g7,g6)
    c: InternalAlignment(g8,g6)
    c: Block(g6)
    c: Coincident(g9,g1)
    c: Coincident(g9,g6)
    c: Horizontal(g9)
    c: Vertical(g10)
    c: Block(g10)
    c: Horizontal(g11)
    c: Block(g11)
    c: Coincident(g12,g10)
    c: Horizontal(g12)
    c: Block(g12)
    c: Coincident(g13,g11)
    c: Vertical(g13)
    c: Block(g13)
    c: Coincident(g14,g10)
    c: Horizontal(g14)
    c: Block(g14)
    c: Block(g9)
    c: Block(g1)
    c: Weight(g15) = 1
    c: Equal(g15,g16)
    c: Equal(g15,g17)
    c: InternalAlignment(g15,g18)
    c: InternalAlignment(g16,g18)
    c: InternalAlignment(g17,g18)
    c: InternalAlignment(g19,g18)
    c: InternalAlignment(g20,g18)
    c: Weight(g21) = 1
    c: Equal(g21,g22)
    c: Equal(g21,g23)
    c: InternalAlignment(g21,g24)
    c: InternalAlignment(g22,g24)
    c: InternalAlignment(g23,g24)
    c: InternalAlignment(g25,g24)
    c: InternalAlignment(g26,g24)
    c: Weight(g27) = 1
    c: Equal(g27,g28)
    c: Equal(g27,g29)
    c: Coincident(g30,g14)
    c: InternalAlignment(g27,g30)
    c: InternalAlignment(g28,g30)
    c: InternalAlignment(g29,g30)
    c: InternalAlignment(g31,g30)
    c: InternalAlignment(g32,g30)
    c: Coincident(g36,g12)
    c: Weight(g33) = 1
    c: Equal(g33,g34)
    c: Equal(g33,g35)
    c: Coincident(g36,g11)
    c: InternalAlignment(g33,g36)
    c: InternalAlignment(g34,g36)
    c: InternalAlignment(g35,g36)
    c: InternalAlignment(g37,g36)
    c: InternalAlignment(g38,g36)
    c: Coincident(g42,g13)
    c: Weight(g39) = 1
    c: Equal(g39,g40)
    c: Equal(g39,g41)
    c: Coincident(g42,g1)
    c: InternalAlignment(g39,g42)
    c: InternalAlignment(g40,g42)
    c: InternalAlignment(g41,g42)
    c: InternalAlignment(g43,g42)
    c: InternalAlignment(g44,g42)
    c: Block(g18)
    c: Block(g24)
    c: Block(g30)
    c: Block(g36)
    c: Block(g42)
    c: Horizontal(g45)
    c: Coincident(g45,g0)
    c: Vertical(g46)
    c: Coincident(g46,g45)
    c: Coincident(g47,g46)
    c: Coincident(g47,g18)
    c: Horizontal(g47)
    c: Block(g46)
    c: Coincident(g48,g18)
    c: Horizontal(g48)
    c: Distance(g48) = 1.33
    c: Vertical(g49)
    c: Coincident(g49,g48)
    c: Coincident(g50,g49)
    c: Coincident(g50,g24)
    c: Horizontal(g50)
    c: Tangent(g50,g22)
    c: Horizontal(g51)
    c: Coincident(g51,g24)
    c: Block(g51)
    c: Vertical(g52)
    c: Block(g52)
    c: Coincident(g52,g51)
    c: Coincident(g53,g52)
    c: Coincident(g53,g30)
    c: Horizontal(g53)
    c: Distance(g1) = 8.5
FEATURE [Part::Feature] Face024
  shape: bbox 9.8 x 26.5 x 2e-07 mm, 1 faces, 0 solids (baked)
FEATURE [Part::Revolution] Revolve024
  Angle = 360
  Axis = (0,1,0)
  Base = (0,0,0)
  FaceMakerClass = Part::FaceMakerBullseye
  Placement = pos=(0,0,0) rot=(0,0,1;1.5708rad)
  Solid = false
  Source = -> Face024
  Symmetric = false
FEATURE [Part::Feature] Face025
  shape: bbox 9.8 x 26.5 x 2e-07 mm, 1 faces, 0 solids (baked)
FEATURE [Part::Revolution] Revolve025
  Angle = 360
  Axis = (0,1,0)
  Base = (0,0,0)
  FaceMakerClass = Part::FaceMakerBullseye
  Placement = pos=(0,0,0) rot=(0,0,1;1.5708rad)
  Solid = false
  Source = -> Face025
  Symmetric = false
FEATURE [Part::MultiFuse] Fusion033
  Placement = pos=(-18,19,36) rot=(0,0,1;0rad)
  Shapes = -> [Revolve025,Revolve024]
FEATURE [Part::Cylinder] Cylinder014
  Angle = 360
  AttacherType = Attacher::AttachEngine3D
  Height = 20
  Placement = pos=(0,0,36.15) rot=(0,0,1;0rad)
  Radius = 14.3
FEATURE [Part::Cylinder] Cylinder015
  Angle = 360
  AttacherType = Attacher::AttachEngine3D
  Height = 10
  Placement = pos=(0,0,36.15) rot=(0,0,1;0rad)
  Radius = 4
FEATURE [Part::MultiFuse] Fusion034  label="removeToCreteHoleForPlugHousing004"
  Placement = pos=(-42,19,36) rot=(0,1,0;1.5708rad)
  Shapes = -> [Cylinder014,Cylinder015]
FEATURE [Part::Cut] Cut008  label="top004"
  Base = -> Cut004
  Placement = pos=(-1,0,0) rot=(0,0,1;0rad)
  Tool = -> Fusion034
FEATURE [Part::Box] Box005  label="Cube005"
  AttacherType = Attacher::AttachEngine3D
  Height = 28
  Length = 3
  Placement = pos=(110.7,19,22) rot=(0,0,1;0rad)
  Width = 15.7
FEATURE [Part::Cylinder] Cylinder016
  Angle = 360
  AttacherType = Attacher::AttachEngine3D
  Height = 10
  Placement = pos=(0,0,36.15) rot=(0,0,1;0rad)
  Radius = 4
FEATURE [Part::Cylinder] Cylinder017
  Angle = 360
  AttacherType = Attacher::AttachEngine3D
  Height = 20
  Placement = pos=(0,0,36.15) rot=(0,0,1;0rad)
  Radius = 10.3
FEATURE [Part::MultiFuse] Fusion035  label="removeToCreteHoleForPlugHousing005"
  Placement = pos=(70,19,36) rot=(0,1,0;1.5708rad)
  Shapes = -> [Cylinder017,Cylinder016]
FEATURE [Part::Cut] Cut009  label="plugHousingTab001"
  Base = -> Box005
  Placement = pos=(-107.4,-14,0) rot=(0,0,1;0rad)
  Tool = -> Fusion035
FEATURE [Part::Box] Box006  label="Cube006"
  AttacherType = Attacher::AttachEngine3D
  Height = 28
  Length = 3
  Placement = pos=(110.7,19,22) rot=(0,0,1;0rad)
  Width = 15.7
FEATURE [Part::Cylinder] Cylinder018
  Angle = 360
  AttacherType = Attacher::AttachEngine3D
  Height = 10
  Placement = pos=(0,0,36.15) rot=(0,0,1;0rad)
  Radius = 4
FEATURE [Part::Cylinder] Cylinder019
  Angle = 360
  AttacherType = Attacher::AttachEngine3D
  Height = 20
  Placement = pos=(0,0,36.15) rot=(0,0,1;0rad)
  Radius = 10.3
FEATURE [Part::MultiFuse] Fusion036  label="removeToCreteHoleForPlugHousing006"
  Placement = pos=(70,19,36) rot=(0,1,0;1.5708rad)
  Shapes = -> [Cylinder019,Cylinder018]
FEATURE [Part::Cut] Cut010  label="plugHousingTab002"
  Base = -> Box006
  Placement = pos=(-107.4,-14,0) rot=(0,0,1;0rad)
  Tool = -> Fusion036
FEATURE [Part::MultiFuse] Fusion037
  Placement = pos=(9.6,23,0) rot=(0,0,1;3.14159rad)
  Shapes = -> [Cut009,Cut010]
FEATURE [Part::Box] Box  label="Cube"
  AttacherType = Attacher::AttachEngine3D
  Height = 10
  Length = 3
  Placement = pos=(3.3,4,12) rot=(0,0,1;0rad)
  Width = 10
FEATURE [Part::Fillet] Fillet004
  Base = -> Fusion028
  Edges = 1 edges r=2: [Edge25]
FEATURE [Part::Fillet] Fillet005  label="plugHousing046"
  Base = -> Fillet004
  Edges = 1 edges r=2: [Edge8]
FEATURE [Part::Fillet] Fillet006
  Base = -> Box
  Edges = 1 edges r=2: [Edge11]
FEATURE [Part::Box] Box007  label="Cube007"
  AttacherType = Attacher::AttachEngine3D
  Height = 10
  Length = 3
  Placement = pos=(3.3,4,50) rot=(0,0,1;0rad)
  Width = 10
FEATURE [Part::Fillet] Fillet007
  Base = -> Box007
  Edges = 1 edges r=2: [Edge12]
FEATURE [Part::Box] Box008  label="Cube008"
  AttacherType = Attacher::AttachEngine3D
  Height = 28
  Length = 4
  Placement = pos=(5,0,22) rot=(0,0,1;0rad)
  Width = 10
FEATURE [Part::Fillet] Fillet008
  Base = -> Box008
  Edges = 1 edges r=1: [Edge7]
FEATURE [Part::Fillet] Fillet009
  Base = -> Fillet008
  Edges = 1 edges r=2: [Edge5]
FEATURE [Part::Fillet] Fillet010
  Base = -> Fillet009
  Edges = 1 edges r=2: [Edge2]
FEATURE [Sketcher::SketchObject] Sketch009  label="topSketch003"
  FullyConstrained = true
  sketch-geometry (4):
    g0: LineSegment StartX=16.8446 StartY=31.512 StartZ=0 EndX=16.3251 EndY=34.4666 EndZ=0
    g1: ArcOfCircle CenterX=19 CenterY=19.2524 CenterZ=0 NormalX=0 NormalY=0 NormalZ=1 AngleXU=0 Radius=15.4476 StartAngle=1.74483 EndAngle=2.72717
    g2: ArcOfCircle CenterX=19 CenterY=19.2524 CenterZ=0 NormalX=0 NormalY=0 NormalZ=1 AngleXU=0 Radius=12.4476 StartAngle=1.74483 EndAngle=2.73189
    g3: LineSegment StartX=4.86004 StartY=25.4725 StartZ=0 EndX=7.58253 EndY=24.2107 EndZ=0
  constraints (7):
    c: Block(g0)
    c: Coincident(g1,g0)
    c: Coincident(g2,g0)
    c: Coincident(g3,g1)
    c: Coincident(g3,g2)
    c: Block(g1)
    c: Block(g2)
FEATURE [Part::Extrusion] Extrude008
  Base = -> Sketch009
  Dir = (0,0,1)
  DirMode = 2
  FaceMakerClass = Part::FaceMakerBullseye
  LengthFwd = 10
  LengthRev = 0
  Placement = pos=(0,0,31) rot=(0,0,1;0rad)
  Solid = true
  Symmetric = false
FEATURE [Part::Cylinder] Cylinder020
  Angle = 360
  AttacherType = Attacher::AttachEngine3D
  Height = 20
  Placement = pos=(0,0,36.15) rot=(0,0,1;0rad)
  Radius = 8.2
FEATURE [Part::Cylinder] Cylinder021
  Angle = 360
  AttacherType = Attacher::AttachEngine3D
  Height = 10
  Placement = pos=(0,0,36.15) rot=(0,0,1;0rad)
  Radius = 4
FEATURE [Part::MultiFuse] Fusion038  label="removeToCreteHoleForPlugHousing007"
  Placement = pos=(-42,19,36) rot=(0,1,0;1.5708rad)
  Shapes = -> [Cylinder020,Cylinder021]
FEATURE [Part::Cut] Cut011
  Base = -> Extrude008
  Tool = -> Fusion038
FEATURE [Part::Fillet] Fillet011
  Base = -> Cut011
  Edges = 1 edges r=2: [Edge1]
FEATURE [Part::Fillet] Fillet012
  Base = -> Fillet011
  Edges = 1 edges r=2.5: [Edge1]
FEATURE [Part::Fillet] Fillet013
  Base = -> Fillet012
  Edges = 1 edges r=2.5: [Edge2]
FEATURE [Part::Box] Box010  label="Cube010"
  AttacherType = Attacher::AttachEngine3D
  Height = 16
  Length = 8
  Placement = pos=(12.7,31.52,28) rot=(0,0,1;0rad)
  Width = 4
FEATURE [Sketcher::SketchObject] Sketch010  label="topSketch004"
  FullyConstrained = true
  sketch-geometry (4):
    g0: LineSegment StartX=16.8446 StartY=31.512 StartZ=0 EndX=16.3251 EndY=34.4666 EndZ=0
    g1: ArcOfCircle CenterX=19 CenterY=19.2524 CenterZ=0 NormalX=0 NormalY=0 NormalZ=1 AngleXU=0 Radius=15.4476 StartAngle=1.74483 EndAngle=2.72717
    g2: ArcOfCircle CenterX=19 CenterY=19.2524 CenterZ=0 NormalX=0 NormalY=0 NormalZ=1 AngleXU=0 Radius=12.4476 StartAngle=1.74483 EndAngle=2.73189
    g3: LineSegment StartX=4.86004 StartY=25.4725 StartZ=0 EndX=7.58253 EndY=24.2107 EndZ=0
  constraints (7):
    c: Block(g0)
    c: Coincident(g1,g0)
    c: Coincident(g2,g0)
    c: Coincident(g3,g1)
    c: Coincident(g3,g2)
    c: Block(g1)
    c: Block(g2)
FEATURE [Part::Cylinder] Cylinder022
  Angle = 360
  AttacherType = Attacher::AttachEngine3D
  Height = 10
  Placement = pos=(0,0,36.15) rot=(0,0,1;0rad)
  Radius = 4
FEATURE [Sketcher::SketchObject] Sketch011  label="topSketch005"
  FullyConstrained = true
  sketch-geometry (4):
    g0: LineSegment StartX=16.8446 StartY=31.512 StartZ=0 EndX=16.3251 EndY=34.4666 EndZ=0
    g1: ArcOfCircle CenterX=19 CenterY=19.2524 CenterZ=0 NormalX=0 NormalY=0 NormalZ=1 AngleXU=0 Radius=15.4476 StartAngle=1.74483 EndAngle=2.72717
    g2: ArcOfCircle CenterX=19 CenterY=19.2524 CenterZ=0 NormalX=0 NormalY=0 NormalZ=1 AngleXU=0 Radius=12.4476 StartAngle=1.74483 EndAngle=2.73189
    g3: LineSegment StartX=4.86004 StartY=25.4725 StartZ=0 EndX=7.58253 EndY=24.2107 EndZ=0
  constraints (7):
    c: Block(g0)
    c: Coincident(g1,g0)
    c: Coincident(g2,g0)
    c: Coincident(g3,g1)
    c: Coincident(g3,g2)
    c: Block(g1)
    c: Block(g2)
FEATURE [Part::Extrusion] Extrude010
  Base = -> Sketch011
  Dir = (0,0,1)
  DirMode = 2
  FaceMakerClass = Part::FaceMakerBullseye
  LengthFwd = 10.6
  LengthRev = 0
  Placement = pos=(0,0,31) rot=(0,0,1;0rad)
  Solid = true
  Symmetric = false
FEATURE [Part::Cylinder] Cylinder023
  Angle = 360
  AttacherType = Attacher::AttachEngine3D
  Height = 20
  Placement = pos=(0,0,36.15) rot=(0,0,1;0rad)
  Radius = 8.2
FEATURE [Part::MultiFuse] Fusion039  label="removeToCreteHoleForPlugHousing008"
  Placement = pos=(-42,19,36) rot=(0,1,0;1.5708rad)
  Shapes = -> [Cylinder023,Cylinder022]
FEATURE [Part::Cut] Cut012
  Base = -> Extrude010
  Placement = pos=(0,0,-0.3) rot=(0,0,1;0rad)
  Tool = -> Fusion039
FEATURE [Part::Cut] Cut013
  Base = -> Box010
  Tool = -> Cut012
FEATURE [Part::Fillet] Fillet014
  Base = -> Cut013
  Edges = 1 edges r=0.7: [Edge13]
FEATURE [Part::Fillet] Fillet015
  Base = -> Fillet014
  Edges = 1 edges r=0.7: [Edge13]
FEATURE [Part::Fillet] Fillet016
  Base = -> Fillet015
  Edges = 1 edges r=0.7: [Edge16]
FEATURE [Part::Fillet] Fillet017
  Base = -> Fillet016
  Edges = 1 edges r=0.7: [Edge11]
FEATURE [Part::Fillet] Fillet018
  Base = -> Fillet017
  Edges = 1 edges r=0.7: [Edge10]
FEATURE [Part::Fillet] Fillet019
  Base = -> Fillet018
  Edges = 1 edges r=1.2: [Edge5]
FEATURE [Part::Fillet] Fillet020
  Base = -> Fillet019
  Edges = 1 edges r=1.2: [Edge12]
FEATURE [Part::Fillet] Fillet021
  Base = -> Fillet020
  Edges = 1 edges r=2: [Edge1]
  Placement = pos=(0.3,0,0) rot=(0,0,1;0rad)
FEATURE [Part::MultiFuse] Fusion040  label="top005"
  Shapes = -> [Cut008,Fillet021]
FEATURE [Part::MultiFuse] Fusion041  label="wireHolder"
  Shapes = -> [Fusion033,Fillet013]
FEATURE [Part::MultiFuse] Fusion042
  Shapes = -> [Fillet007,Fusion041]
FEATURE [Part::MultiFuse] Fusion043  label="wireHolder001"
  Shapes = -> [Fusion042,Fillet010]
FEATURE [Part::MultiFuse] Fusion044  label="wireHolder002"
  Shapes = -> [Fillet006,Fusion037,Fusion043]
FEATURE [Part::Feature] Face026
  shape: bbox 11 x 6 x 2e-07 mm, 1 faces, 0 solids (baked)
FEATURE [Part::Revolution] Revolve026
  Angle = 360
  Axis = (0,1,0)
  Base = (0,0,0)
  FaceMakerClass = Part::FaceMakerBullseye
  Placement = pos=(30.3,-1,19.7) rot=(0,0,1;0rad)
  Solid = false
  Source = -> Face026
  Symmetric = false
FEATURE [Sketcher::SketchObject] Sketch013  label="topSketch006"
  FullyConstrained = true
  sketch-geometry (13):
    g0: LineSegment StartX=117 StartY=19 StartZ=0 EndX=117 EndY=38 EndZ=0
    g1: ArcOfCircle CenterX=98 CenterY=19 CenterZ=0 NormalX=0 NormalY=0 NormalZ=1 AngleXU=0 Radius=19 StartAngle=5.7297 EndAngle=6.28319
    g2: LineSegment StartX=0 StartY=3 StartZ=0 EndX=0 EndY=19 EndZ=0
    g3: LineSegment StartX=19 StartY=38 StartZ=0 EndX=117 EndY=38 EndZ=0
    g4: ArcOfCircle CenterX=19 CenterY=19 CenterZ=0 NormalX=0 NormalY=0 NormalZ=1 AngleXU=0 Radius=19 StartAngle=1.5708 EndAngle=3.14159
    g5: ArcOfCircle CenterX=19 CenterY=19 CenterZ=0 NormalX=0 NormalY=0 NormalZ=1 AngleXU=0 Radius=16 StartAngle=1.5708 EndAngle=3.14159
    g6: ArcOfCircle CenterX=98 CenterY=19 CenterZ=0 NormalX=0 NormalY=0 NormalZ=1 AngleXU=0 Radius=16 StartAngle=5.60905 EndAngle=6.28319
    g7: LineSegment StartX=114 StartY=19 StartZ=0 EndX=114 EndY=35 EndZ=0
    g8: LineSegment StartX=110.5 StartY=9.01251 StartZ=0 EndX=114.163 EndY=9.01251 EndZ=0
    g9: LineSegment StartX=114 StartY=35 StartZ=0 EndX=19 EndY=35 EndZ=0
    g10: LineSegment StartX=0 StartY=3 StartZ=0 EndX=0 EndY=0 EndZ=0
    g11: LineSegment StartX=3 StartY=0 StartZ=0 EndX=0 EndY=0 EndZ=0
    g12: LineSegment StartX=3 StartY=19 StartZ=0 EndX=3 EndY=0 EndZ=0
  constraints (33):
    c: Vertical(g0)
    c: Distance(g0) = 19
    c: Block(g0)
    c: Coincident(g1,g0)
    c: Block(g1)
    c: Vertical(g2)
    c: Block(g2)
    c: Coincident(g3,g0)
    c: Horizontal(g3)
    c: Distance(g3) = 98
    c: Coincident(g4,g3)
    c: Coincident(g4,g2)
    c: Block(g4)
    c: Coincident(g5,g4)
    c: Coincident(g6,g1)
    c: Block(g6)
    c: Block(g5)
    c: Coincident(g7,g6)
    c: Vertical(g7)
    c: Coincident(g8,g6)
    c: Coincident(g8,g1)
    c: Coincident(g9,g7)
    c: Coincident(g9,g5)
    c: Horizontal(g9)
    c: Tangent(g9,g5)
    c: Coincident(g10,g2)
    c: Distance(g10) = 3
    c: Vertical(g10)
    c: Coincident(g11,g10)
    c: Horizontal(g11)
    c: Coincident(g12,g5)
    c: Coincident(g12,g11)
    c: Vertical(g12)
FEATURE [Part::Extrusion] Extrude011  label="top006"
  Base = -> Sketch013
  Dir = (0,0,1)
  DirMode = 2
  FaceMakerClass = Part::FaceMakerBullseye
  LengthFwd = 72
  LengthRev = 0
  Solid = true
  Symmetric = false
FEATURE [Sketcher::SketchObject] Sketch014
  FullyConstrained = true
  MapMode = 3
  Placement = pos=(0,0,0) rot=(1,0,0;1.5708rad)
  Support = -> [Extrude011]
  sketch-geometry (8):
    g0: Circle CenterX=80.351 CenterY=-67.6202 CenterZ=0 NormalX=0 NormalY=0 NormalZ=1 AngleXU=0 Radius=2
    g1: Circle CenterX=80.351 CenterY=-67.6202 CenterZ=0 NormalX=0 NormalY=0 NormalZ=1 AngleXU=0 Radius=3
    g2: Circle CenterX=80.351 CenterY=-4.92017 CenterZ=0 NormalX=0 NormalY=0 NormalZ=1 AngleXU=0 Radius=2
    g3: Circle CenterX=80.351 CenterY=-4.92017 CenterZ=0 NormalX=0 NormalY=0 NormalZ=1 AngleXU=0 Radius=3
    g4: Circle CenterX=23.851 CenterY=-4.92017 CenterZ=0 NormalX=0 NormalY=0 NormalZ=1 AngleXU=0 Radius=2
    g5: Circle CenterX=23.851 CenterY=-4.92017 CenterZ=0 NormalX=0 NormalY=0 NormalZ=1 AngleXU=0 Radius=3
    g6: Circle CenterX=23.851 CenterY=-67.6202 CenterZ=0 NormalX=0 NormalY=0 NormalZ=1 AngleXU=0 Radius=2
    g7: Circle CenterX=23.851 CenterY=-67.6202 CenterZ=0 NormalX=0 NormalY=0 NormalZ=1 AngleXU=0 Radius=3
  constraints (8):
    c: Block(g3)
    c: Block(g2)
    c: Block(g1)
    c: Block(g0)
    c: Block(g6)
    c: Block(g7)
    c: Block(g4)
    c: Block(g5)
FEATURE [Part::Feature] Face027
  shape: bbox 11 x 6 x 2e-07 mm, 1 faces, 0 solids (baked)
FEATURE [Part::Revolution] Revolve027
  Angle = 360
  Axis = (0,1,0)
  Base = (0,0,0)
  FaceMakerClass = Part::FaceMakerBullseye
  Placement = pos=(30.3,-1,51.7) rot=(0,0,1;0rad)
  Solid = false
  Source = -> Face027
  Symmetric = false
FEATURE [Part::Feature] Face028
  shape: bbox 11 x 6 x 2e-07 mm, 1 faces, 0 solids (baked)
FEATURE [Part::Revolution] Revolve028
  Angle = 360
  Axis = (0,1,0)
  Base = (0,0,0)
  FaceMakerClass = Part::FaceMakerBullseye
  Placement = pos=(62.3,-1,19.7) rot=(0,0,1;0rad)
  Solid = false
  Source = -> Face028
  Symmetric = false
FEATURE [Part::Feature] Face029
  shape: bbox 11 x 6 x 2e-07 mm, 1 faces, 0 solids (baked)
FEATURE [Part::Revolution] Revolve029
  Angle = 360
  Axis = (0,1,0)
  Base = (0,0,0)
  FaceMakerClass = Part::FaceMakerBullseye
  Placement = pos=(62.3,-1,51.7) rot=(0,0,1;0rad)
  Solid = false
  Source = -> Face029
  Symmetric = false
FEATURE [Part::Feature] Wire
  shape: bbox 11 x 5.2 x 2e-07 mm, 0 faces, 0 solids (baked)
FEATURE [Part::Revolution] Revolve030
  Angle = 360
  Axis = (0,1,0)
  Base = (0,0,0)
  FaceMakerClass = Part::FaceMakerBullseye
  Placement = pos=(30.3,38,19.7) rot=(0,0,1;0rad)
  Solid = true
  Source = -> Wire
  Symmetric = false
FEATURE [Part::Feature] Wire001
  shape: bbox 11 x 5.2 x 2e-07 mm, 0 faces, 0 solids (baked)
FEATURE [Part::Revolution] Revolve031
  Angle = 360
  Axis = (0,1,0)
  Base = (0,0,0)
  FaceMakerClass = Part::FaceMakerBullseye
  Placement = pos=(30.3,38,51.7) rot=(0,0,1;0rad)
  Solid = true
  Source = -> Wire001
  Symmetric = false
FEATURE [Part::Feature] Wire002
  shape: bbox 11 x 5.2 x 2e-07 mm, 0 faces, 0 solids (baked)
FEATURE [Part::Revolution] Revolve032
  Angle = 360
  Axis = (0,1,0)
  Base = (0,0,0)
  FaceMakerClass = Part::FaceMakerBullseye
  Placement = pos=(62.3,38,51.7) rot=(0,0,1;0rad)
  Solid = true
  Source = -> Wire002
  Symmetric = false
FEATURE [Part::Feature] Wire003
  shape: bbox 11 x 5.2 x 2e-07 mm, 0 faces, 0 solids (baked)
FEATURE [Part::Revolution] Revolve033
  Angle = 360
  Axis = (0,1,0)
  Base = (0,0,0)
  FaceMakerClass = Part::FaceMakerBullseye
  Placement = pos=(62.3,38,19.7) rot=(0,0,1;0rad)
  Solid = true
  Source = -> Wire003
  Symmetric = false
FEATURE [Part::MultiFuse] Fusion045  label="altRandScrewHousing"
  Shapes = -> [Revolve029,Revolve027,Revolve028,Revolve026]
FEATURE [Part::MultiFuse] Fusion046  label="fanScrewHousing"
  Shapes = -> [Revolve033,Revolve032,Revolve031,Revolve030]
FEATURE [Sketcher::SketchObject] Sketch015
  FullyConstrained = true
  sketch-geometry (17):
    g0: Circle CenterX=-3.5 CenterY=23.5 CenterZ=0 NormalX=0 NormalY=0 NormalZ=1 AngleXU=0 Radius=1
    g1: Circle CenterX=-1 CenterY=15.25 CenterZ=0 NormalX=0 NormalY=0 NormalZ=1 AngleXU=0 Radius=1
    g2: Circle CenterX=-3.5 CenterY=7 CenterZ=0 NormalX=0 NormalY=0 NormalZ=1 AngleXU=0 Radius=1
    g3: BSplineCurve PolesCount=3 KnotsCount=2 Degree=2 IsPeriodic=0
    g4: GeomPoint X=-3.5 Y=23.5 Z=0
    g5: GeomPoint X=-3.5 Y=7 Z=0
    g6: Circle CenterX=-4.8 CenterY=30.5 CenterZ=0 NormalX=0 NormalY=0 NormalZ=1 AngleXU=0 Radius=1
    g7: Circle CenterX=-3.5 CenterY=30.5 CenterZ=0 NormalX=0 NormalY=0 NormalZ=1 AngleXU=0 Radius=1
    g8: Circle CenterX=-3.5 CenterY=29.2 CenterZ=0 NormalX=0 NormalY=0 NormalZ=1 AngleXU=0 Radius=1
    g9: BSplineCurve PolesCount=3 KnotsCount=2 Degree=2 IsPeriodic=0
    g10: GeomPoint X=-4.8 Y=30.5 Z=0
    g11: GeomPoint X=-3.5 Y=29.2 Z=0
    g12: LineSegment StartX=-3.5 StartY=29.2 StartZ=0 EndX=-3.5 EndY=23.5 EndZ=0
    g13: LineSegment StartX=-4.8 StartY=30.5 StartZ=0 EndX=0 EndY=30.5 EndZ=0
    g14: LineSegment StartX=-3.5 StartY=0.3 StartZ=0 EndX=0 EndY=0.3 EndZ=0
    g15: LineSegment StartX=-3.5 StartY=0.3 StartZ=0 EndX=-3.5 EndY=7 EndZ=0
    g16: LineSegment StartX=0 StartY=0.3 StartZ=0 EndX=0 EndY=30.5 EndZ=0
  constraints (33):
    c: Weight(g0) = 1
    c: Equal(g0,g1)
    c: Equal(g0,g2)
    c: InternalAlignment(g0,g3)
    c: InternalAlignment(g1,g3)
    c: InternalAlignment(g2,g3)
    c: InternalAlignment(g4,g3)
    c: InternalAlignment(g5,g3)
    c: Block(g3)
    c: Weight(g6) = 1
    c: Equal(g6,g7)
    c: Equal(g6,g8)
    c: InternalAlignment(g6,g9)
    c: InternalAlignment(g7,g9)
    c: InternalAlignment(g8,g9)
    c: InternalAlignment(g10,g9)
    c: InternalAlignment(g11,g9)
    c: Block(g9)
    c: Coincident(g12,g9)
    c: Coincident(g12,g3)
    c: Vertical(g12)
    c: Coincident(g13,g9)
    c: Horizontal(g13)
    c: Distance(g13) = 4.8
    c: Horizontal(g14)
    c: Block(g14)
    c: Coincident(g15,g14)
    c: Coincident(g15,g3)
    c: Vertical(g15)
    c: Coincident(g16,g14)
    c: Coincident(g16,g13)
    c: Vertical(g16)
    c: Tangent(g16,g1)
FEATURE [Sketcher::SketchObject] Sketch016
  FullyConstrained = true
  sketch-geometry (16):
    g0: Circle CenterX=-3.5 CenterY=23.5 CenterZ=0 NormalX=0 NormalY=0 NormalZ=1 AngleXU=0 Radius=1
    g1: Circle CenterX=-1 CenterY=15.25 CenterZ=0 NormalX=0 NormalY=0 NormalZ=1 AngleXU=0 Radius=1
    g2: Circle CenterX=-3.5 CenterY=7 CenterZ=0 NormalX=0 NormalY=0 NormalZ=1 AngleXU=0 Radius=1
    g3: BSplineCurve PolesCount=3 KnotsCount=2 Degree=2 IsPeriodic=0
    g4: GeomPoint X=-3.5 Y=23.5 Z=0
    g5: GeomPoint X=-3.5 Y=7 Z=0
    g6: LineSegment StartX=-3.5 StartY=28.2 StartZ=0 EndX=-3.5 EndY=23.5 EndZ=0
    g7: LineSegment StartX=0 StartY=29.5 StartZ=0 EndX=0 EndY=30 EndZ=0
    g8: LineSegment StartX=-3.5 StartY=28.2 StartZ=0 EndX=-3.5 EndY=30 EndZ=0
    g9: LineSegment StartX=0 StartY=30 StartZ=0 EndX=0 EndY=30.5 EndZ=0
    g10: LineSegment StartX=0 StartY=30.5 StartZ=0 EndX=-3.5 EndY=30.5 EndZ=0
    g11: LineSegment StartX=-3.5 StartY=30.5 StartZ=0 EndX=-3.5 EndY=30 EndZ=0
    g12: LineSegment StartX=0 StartY=29.5 StartZ=0 EndX=0 EndY=5 EndZ=0
    g13: LineSegment StartX=-3.5 StartY=0.3 StartZ=0 EndX=-3.5 EndY=7 EndZ=0
    g14: LineSegment StartX=-3.5 StartY=0.3 StartZ=0 EndX=0 EndY=0.3 EndZ=0
    g15: LineSegment StartX=0 StartY=5 StartZ=0 EndX=0 EndY=0.3 EndZ=0
  constraints (39):
    c: Weight(g0) = 1
    c: Equal(g0,g1)
    c: Equal(g0,g2)
    c: InternalAlignment(g0,g3)
    c: InternalAlignment(g1,g3)
    c: InternalAlignment(g2,g3)
    c: InternalAlignment(g4,g3)
    c: InternalAlignment(g5,g3)
    c: Block(g3)
    c: Coincident(g6,g3)
    c: Vertical(g6)
    c: Vertical(g7)
    c: Distance(g7) = 0.5
    c: Coincident(g8,g6)
    c: Vertical(g8)
    c: Block(g6)
    c: Block(g7)
    c: Vertical(g9)
    c: Equal(g7,g9) = 0.5
    c: Block(g9)
    c: Coincident(g9,g7)
    c: Horizontal(g10)
    c: Coincident(g10,g9)
    c: Coincident(g11,g10)
    c: Coincident(g11,g8)
    c: Vertical(g11)
    c: Block(g11)
    c: Coincident(g12,g7)
    c: Vertical(g12)
    c: Coincident(g13,g3)
    c: Vertical(g13)
    c: Distance(g13) = 6.7
    c: Coincident(g14,g13)
    c: Horizontal(g14)
    c: Block(g14)
    c: Coincident(g15,g12)
    c: Coincident(g15,g14)
    c: Vertical(g15)
    c: Block(g15)
FEATURE [Sketcher::SketchObject] Sketch017
  FullyConstrained = true
  sketch-geometry (11):
    g0: LineSegment StartX=-3.5 StartY=1e-16 StartZ=0 EndX=-1.6 EndY=1e-16 EndZ=0
    g1: LineSegment StartX=-1.6 StartY=1e-16 StartZ=0 EndX=-1.6 EndY=1.5 EndZ=0
    g2: LineSegment StartX=-3.5 StartY=1.5 StartZ=0 EndX=-1.6 EndY=1.5 EndZ=0
    g3: LineSegment StartX=-3.5 StartY=1e-16 StartZ=0 EndX=-4.8 EndY=1e-16 EndZ=0
    g4: Circle CenterX=-3.5 CenterY=1.3 CenterZ=0 NormalX=0 NormalY=0 NormalZ=1 AngleXU=0 Radius=1
    g5: Circle CenterX=-3.5 CenterY=1e-16 CenterZ=0 NormalX=0 NormalY=0 NormalZ=1 AngleXU=0 Radius=1
    g6: Circle CenterX=-4.8 CenterY=1e-16 CenterZ=0 NormalX=0 NormalY=0 NormalZ=1 AngleXU=0 Radius=1
    g7: BSplineCurve PolesCount=3 KnotsCount=2 Degree=2 IsPeriodic=0
    g8: GeomPoint X=-3.5 Y=1.3 Z=0
    g9: GeomPoint X=-4.8 Y=1e-16 Z=0
    g10: LineSegment StartX=-3.5 StartY=1.3 StartZ=0 EndX=-3.5 EndY=1.5 EndZ=0
  constraints (24):
    c: Horizontal(g0)
    c: Distance(g0) = 1.9
    c: Block(g0)
    c: Coincident(g1,g0)
    c: Vertical(g1)
    c: Coincident(g2,g1)
    c: Horizontal(g2)
    c: Coincident(g3,g0)
    c: Horizontal(g3)
    c: Distance(g3) = 1.3
    c: Weight(g4) = 1
    c: Equal(g4,g5)
    c: Coincident(g5,g0)
    c: Equal(g4,g6)
    c: Coincident(g7,g3)
    c: InternalAlignment(g4,g7)
    c: InternalAlignment(g5,g7)
    c: InternalAlignment(g6,g7)
    c: InternalAlignment(g8,g7)
    c: InternalAlignment(g9,g7)
    c: Coincident(g10,g7)
    c: Coincident(g10,g2)
    c: Vertical(g10)
    c: Block(g10)
FEATURE [Part::Feature] Face035
  shape: bbox 3.2 x 1.5 x 2e-07 mm, 1 faces, 0 solids (baked)
FEATURE [Part::Revolution] Revolve039  label="backCaseScrewRetainer"
  Angle = 360
  Axis = (0,1,0)
  Base = (0,0,0)
  FaceMakerClass = Part::FaceMakerBullseye
  Placement = pos=(12.5,3,62) rot=(0,0,1;0rad)
  Solid = false
  Source = -> Face035
  Symmetric = false
FEATURE [Part::Feature] Face036
  shape: bbox 3.2 x 1.5 x 2e-07 mm, 1 faces, 0 solids (baked)
FEATURE [Part::Feature] Face039
  shape: bbox 4.8 x 30.2 x 2e-07 mm, 1 faces, 0 solids (baked)
FEATURE [Part::Revolution] Revolve043  label="frontCaseScrewPost002"
  Angle = 360
  Axis = (0,1,0)
  Base = (0,0,0)
  FaceMakerClass = Part::FaceMakerBullseye
  Placement = pos=(89.5,4.5,3.5) rot=(0,0,1;0rad)
  Solid = false
  Source = -> Face039
  Symmetric = false
FEATURE [Part::Feature] Face042
  shape: bbox 4.8 x 30.2 x 2e-07 mm, 1 faces, 0 solids (baked)
FEATURE [Part::Revolution] Revolve046  label="frontCaseScrewPost003"
  Angle = 360
  Axis = (0,1,0)
  Base = (0,0,0)
  FaceMakerClass = Part::FaceMakerBullseye
  Placement = pos=(89.5,4.5,68.5) rot=(0,0,1;0rad)
  Solid = false
  Source = -> Face042
  Symmetric = false
FEATURE [Part::Feature] Face043
  shape: bbox 3.2 x 1.5 x 2e-07 mm, 1 faces, 0 solids (baked)
FEATURE [Part::Revolution] Revolve047  label="frontCaseScrewRetainer002"
  Angle = 360
  Axis = (0,1,0)
  Base = (0,0,0)
  FaceMakerClass = Part::FaceMakerBullseye
  Placement = pos=(89.5,3,68.5) rot=(0,0,1;0rad)
  Solid = false
  Source = -> Face043
  Symmetric = false
FEATURE [Part::Feature] Face044
  shape: bbox 3.2 x 1.5 x 2e-07 mm, 1 faces, 0 solids (baked)
FEATURE [Part::Revolution] Revolve048  label="frontCaseScrewRetainer003"
  Angle = 360
  Axis = (0,1,0)
  Base = (0,0,0)
  FaceMakerClass = Part::FaceMakerBullseye
  Placement = pos=(89.5,3,3.5) rot=(0,0,1;0rad)
  Solid = false
  Source = -> Face044
  Symmetric = false
FEATURE [App::MeasureDistance] Distance002  label="Distance: 1.67 mm"
  Distance = 1.66921
  P1 = (99.2361,4.7524,71.7)
  P2 = (99.2347,6.42161,71.7)
FEATURE [Sketcher::SketchObject] Sketch018
  FullyConstrained = true
  sketch-geometry (7):
    g0: LineSegment StartX=0 StartY=0 StartZ=0 EndX=0 EndY=6 EndZ=0
    g1: Circle CenterX=0 CenterY=0 CenterZ=0 NormalX=0 NormalY=0 NormalZ=1 AngleXU=0 Radius=1
    g2: Circle CenterX=8 CenterY=6 CenterZ=0 NormalX=0 NormalY=0 NormalZ=1 AngleXU=0 Radius=1
    g3: BSplineCurve PolesCount=3 KnotsCount=2 Degree=2 IsPeriodic=0
    g4: GeomPoint X=0 Y=0 Z=0
    g5: GeomPoint X=8 Y=6 Z=0
    g6: LineSegment StartX=0 StartY=6 StartZ=0 EndX=8 EndY=6 EndZ=0
  constraints (14):
    c: Coincident(g0,g-1)
    c: Distance(g0) = 6
    c: Vertical(g0)
    c: Coincident(g3,g0)
    c: Weight(g1) = 1
    c: Equal(g1,g2)
    c: InternalAlignment(g1,g3)
    c: InternalAlignment(g2,g3)
    c: InternalAlignment(g4,g3)
    c: InternalAlignment(g5,g3)
    c: Block(g3)
    c: Coincident(g6,g0)
    c: Coincident(g6,g3)
    c: Horizontal(g6)
FEATURE [Part::Extrusion] Extrude012  label="caseScrewPillarBracket"
  Base = -> Sketch018
  Dir = (0,0,1)
  DirMode = 2
  FaceMakerClass = Part::FaceMakerBullseye
  LengthFwd = 2.4
  LengthRev = 0
  Placement = pos=(15.76,29,8.8) rot=(0,1,0;0rad)
  Solid = true
  Symmetric = false
FEATURE [Sketcher::SketchObject] Sketch019
  FullyConstrained = true
  sketch-geometry (7):
    g0: LineSegment StartX=0 StartY=0 StartZ=0 EndX=0 EndY=6 EndZ=0
    g1: Circle CenterX=0 CenterY=0 CenterZ=0 NormalX=0 NormalY=0 NormalZ=1 AngleXU=0 Radius=1
    g2: Circle CenterX=8 CenterY=6 CenterZ=0 NormalX=0 NormalY=0 NormalZ=1 AngleXU=0 Radius=1
    g3: BSplineCurve PolesCount=3 KnotsCount=2 Degree=2 IsPeriodic=0
    g4: GeomPoint X=0 Y=0 Z=0
    g5: GeomPoint X=8 Y=6 Z=0
    g6: LineSegment StartX=0 StartY=6 StartZ=0 EndX=8 EndY=6 EndZ=0
  constraints (14):
    c: Coincident(g0,g-1)
    c: Distance(g0) = 6
    c: Vertical(g0)
    c: Coincident(g3,g0)
    c: Weight(g1) = 1
    c: Equal(g1,g2)
    c: InternalAlignment(g1,g3)
    c: InternalAlignment(g2,g3)
    c: InternalAlignment(g4,g3)
    c: InternalAlignment(g5,g3)
    c: Block(g3)
    c: Coincident(g6,g0)
    c: Coincident(g6,g3)
    c: Horizontal(g6)
FEATURE [Part::Extrusion] Extrude013  label="caseScrewPillarBracket001"
  Base = -> Sketch019
  Dir = (0,0,1)
  DirMode = 2
  FaceMakerClass = Part::FaceMakerBullseye
  LengthFwd = 2.4
  LengthRev = 0
  Placement = pos=(15.76,29,60.8) rot=(0,0,1;0rad)
  Solid = true
  Symmetric = false
FEATURE [Sketcher::SketchObject] Sketch020
  FullyConstrained = true
  sketch-geometry (7):
    g0: LineSegment StartX=0 StartY=0 StartZ=0 EndX=0 EndY=6 EndZ=0
    g1: Circle CenterX=0 CenterY=0 CenterZ=0 NormalX=0 NormalY=0 NormalZ=1 AngleXU=0 Radius=1
    g2: Circle CenterX=8 CenterY=6 CenterZ=0 NormalX=0 NormalY=0 NormalZ=1 AngleXU=0 Radius=1
    g3: BSplineCurve PolesCount=3 KnotsCount=2 Degree=2 IsPeriodic=0
    g4: GeomPoint X=0 Y=0 Z=0
    g5: GeomPoint X=8 Y=6 Z=0
    g6: LineSegment StartX=0 StartY=6 StartZ=0 EndX=8 EndY=6 EndZ=0
  constraints (14):
    c: Coincident(g0,g-1)
    c: Distance(g0) = 6
    c: Vertical(g0)
    c: Coincident(g3,g0)
    c: Weight(g1) = 1
    c: Equal(g1,g2)
    c: InternalAlignment(g1,g3)
    c: InternalAlignment(g2,g3)
    c: InternalAlignment(g4,g3)
    c: InternalAlignment(g5,g3)
    c: Block(g3)
    c: Coincident(g6,g0)
    c: Coincident(g6,g3)
    c: Horizontal(g6)
FEATURE [Part::Extrusion] Extrude014  label="caseScrewPillarBracket002"
  Base = -> Sketch020
  Dir = (0,0,1)
  DirMode = 2
  FaceMakerClass = Part::FaceMakerBullseye
  LengthFwd = 2.4
  LengthRev = 0
  Placement = pos=(13.7,29,13.26) rot=(0,-1,0;1.5708rad)
  Solid = true
  Symmetric = false
FEATURE [Sketcher::SketchObject] Sketch021
  FullyConstrained = true
  sketch-geometry (7):
    g0: LineSegment StartX=0 StartY=0 StartZ=0 EndX=0 EndY=6 EndZ=0
    g1: Circle CenterX=0 CenterY=0 CenterZ=0 NormalX=0 NormalY=0 NormalZ=1 AngleXU=0 Radius=1
    g2: Circle CenterX=8 CenterY=6 CenterZ=0 NormalX=0 NormalY=0 NormalZ=1 AngleXU=0 Radius=1
    g3: BSplineCurve PolesCount=3 KnotsCount=2 Degree=2 IsPeriodic=0
    g4: GeomPoint X=0 Y=0 Z=0
    g5: GeomPoint X=8 Y=6 Z=0
    g6: LineSegment StartX=0 StartY=6 StartZ=0 EndX=8 EndY=6 EndZ=0
  constraints (14):
    c: Coincident(g0,g-1)
    c: Distance(g0) = 6
    c: Vertical(g0)
    c: Coincident(g3,g0)
    c: Weight(g1) = 1
    c: Equal(g1,g2)
    c: InternalAlignment(g1,g3)
    c: InternalAlignment(g2,g3)
    c: InternalAlignment(g4,g3)
    c: InternalAlignment(g5,g3)
    c: Block(g3)
    c: Coincident(g6,g0)
    c: Coincident(g6,g3)
    c: Horizontal(g6)
FEATURE [Part::Extrusion] Extrude015  label="caseScrewPillarBracket003"
  Base = -> Sketch021
  Dir = (0,0,1)
  DirMode = 2
  FaceMakerClass = Part::FaceMakerBullseye
  LengthFwd = 2.4
  LengthRev = 0
  Placement = pos=(11.3,29,58.74) rot=(0,1,0;1.5708rad)
  Solid = true
  Symmetric = false
FEATURE [Sketcher::SketchObject] Sketch022
  FullyConstrained = true
  sketch-geometry (7):
    g0: LineSegment StartX=0 StartY=0 StartZ=0 EndX=0 EndY=6 EndZ=0
    g1: Circle CenterX=0 CenterY=0 CenterZ=0 NormalX=0 NormalY=0 NormalZ=1 AngleXU=0 Radius=1
    g2: Circle CenterX=8 CenterY=6 CenterZ=0 NormalX=0 NormalY=0 NormalZ=1 AngleXU=0 Radius=1
    g3: BSplineCurve PolesCount=3 KnotsCount=2 Degree=2 IsPeriodic=0
    g4: GeomPoint X=0 Y=0 Z=0
    g5: GeomPoint X=8 Y=6 Z=0
    g6: LineSegment StartX=0 StartY=6 StartZ=0 EndX=8 EndY=6 EndZ=0
  constraints (14):
    c: Coincident(g0,g-1)
    c: Distance(g0) = 6
    c: Vertical(g0)
    c: Coincident(g3,g0)
    c: Weight(g1) = 1
    c: Equal(g1,g2)
    c: InternalAlignment(g1,g3)
    c: InternalAlignment(g2,g3)
    c: InternalAlignment(g4,g3)
    c: InternalAlignment(g5,g3)
    c: Block(g3)
    c: Coincident(g6,g0)
    c: Coincident(g6,g3)
    c: Horizontal(g6)
FEATURE [Part::Extrusion] Extrude016  label="caseScrewPillarBracket004"
  Base = -> Sketch022
  Dir = (0,0,1)
  DirMode = 2
  FaceMakerClass = Part::FaceMakerBullseye
  LengthFwd = 2.4
  LengthRev = 0
  Placement = pos=(88.3,29,65.23) rot=(0,1,0;1.5708rad)
  Solid = true
  Symmetric = false
FEATURE [Sketcher::SketchObject] Sketch023
  FullyConstrained = true
  sketch-geometry (7):
    g0: LineSegment StartX=0 StartY=0 StartZ=0 EndX=0 EndY=6 EndZ=0
    g1: Circle CenterX=0 CenterY=0 CenterZ=0 NormalX=0 NormalY=0 NormalZ=1 AngleXU=0 Radius=1
    g2: Circle CenterX=8 CenterY=6 CenterZ=0 NormalX=0 NormalY=0 NormalZ=1 AngleXU=0 Radius=1
    g3: BSplineCurve PolesCount=3 KnotsCount=2 Degree=2 IsPeriodic=0
    g4: GeomPoint X=0 Y=0 Z=0
    g5: GeomPoint X=8 Y=6 Z=0
    g6: LineSegment StartX=0 StartY=6 StartZ=0 EndX=8 EndY=6 EndZ=0
  constraints (14):
    c: Coincident(g0,g-1)
    c: Distance(g0) = 6
    c: Vertical(g0)
    c: Coincident(g3,g0)
    c: Weight(g1) = 1
    c: Equal(g1,g2)
    c: InternalAlignment(g1,g3)
    c: InternalAlignment(g2,g3)
    c: InternalAlignment(g4,g3)
    c: InternalAlignment(g5,g3)
    c: Block(g3)
    c: Coincident(g6,g0)
    c: Coincident(g6,g3)
    c: Horizontal(g6)
FEATURE [Part::Extrusion] Extrude017  label="caseScrewPillarBracket005"
  Base = -> Sketch023
  Dir = (0,0,1)
  DirMode = 2
  FaceMakerClass = Part::FaceMakerBullseye
  LengthFwd = 2.4
  LengthRev = 0
  Placement = pos=(90.7,29,6.77) rot=(0,-1,0;1.5708rad)
  Solid = true
  Symmetric = false
FEATURE [Sketcher::SketchObject] Sketch024
  FullyConstrained = true
  sketch-geometry (7):
    g0: LineSegment StartX=0 StartY=0 StartZ=0 EndX=0 EndY=6 EndZ=0
    g1: Circle CenterX=0 CenterY=0 CenterZ=0 NormalX=0 NormalY=0 NormalZ=1 AngleXU=0 Radius=1
    g2: Circle CenterX=8 CenterY=6 CenterZ=0 NormalX=0 NormalY=0 NormalZ=1 AngleXU=0 Radius=1
    g3: BSplineCurve PolesCount=3 KnotsCount=2 Degree=2 IsPeriodic=0
    g4: GeomPoint X=0 Y=0 Z=0
    g5: GeomPoint X=8 Y=6 Z=0
    g6: LineSegment StartX=0 StartY=6 StartZ=0 EndX=8 EndY=6 EndZ=0
  constraints (14):
    c: Coincident(g0,g-1)
    c: Distance(g0) = 6
    c: Vertical(g0)
    c: Coincident(g3,g0)
    c: Weight(g1) = 1
    c: Equal(g1,g2)
    c: InternalAlignment(g1,g3)
    c: InternalAlignment(g2,g3)
    c: InternalAlignment(g4,g3)
    c: InternalAlignment(g5,g3)
    c: Block(g3)
    c: Coincident(g6,g0)
    c: Coincident(g6,g3)
    c: Horizontal(g6)
FEATURE [Part::Extrusion] Extrude018  label="caseScrewPillarBracket006"
  Base = -> Sketch024
  Dir = (0,0,1)
  DirMode = 2
  FaceMakerClass = Part::FaceMakerBullseye
  LengthFwd = 2.4
  LengthRev = 0
  Placement = pos=(103.7,29,6.77) rot=(0,-1,0;1.5708rad)
  Solid = true
  Symmetric = false
FEATURE [Sketcher::SketchObject] Sketch025
  FullyConstrained = true
  sketch-geometry (7):
    g0: LineSegment StartX=0 StartY=0 StartZ=0 EndX=0 EndY=6 EndZ=0
    g1: Circle CenterX=0 CenterY=0 CenterZ=0 NormalX=0 NormalY=0 NormalZ=1 AngleXU=0 Radius=1
    g2: Circle CenterX=8 CenterY=6 CenterZ=0 NormalX=0 NormalY=0 NormalZ=1 AngleXU=0 Radius=1
    g3: BSplineCurve PolesCount=3 KnotsCount=2 Degree=2 IsPeriodic=0
    g4: GeomPoint X=0 Y=0 Z=0
    g5: GeomPoint X=8 Y=6 Z=0
    g6: LineSegment StartX=0 StartY=6 StartZ=0 EndX=8 EndY=6 EndZ=0
  constraints (14):
    c: Coincident(g0,g-1)
    c: Distance(g0) = 6
    c: Vertical(g0)
    c: Coincident(g3,g0)
    c: Weight(g1) = 1
    c: Equal(g1,g2)
    c: InternalAlignment(g1,g3)
    c: InternalAlignment(g2,g3)
    c: InternalAlignment(g4,g3)
    c: InternalAlignment(g5,g3)
    c: Block(g3)
    c: Coincident(g6,g0)
    c: Coincident(g6,g3)
    c: Horizontal(g6)
FEATURE [Part::Extrusion] Extrude019  label="caseScrewPillarBracket007"
  Base = -> Sketch025
  Dir = (0,0,1)
  DirMode = 2
  FaceMakerClass = Part::FaceMakerBullseye
  LengthFwd = 2.4
  LengthRev = 0
  Placement = pos=(101.3,29,65.23) rot=(0,1,0;1.5708rad)
  Solid = true
  Symmetric = false
FEATURE [Part::Box] Box011  label="frontCaseScrewPillarBracket"
  AttacherType = Attacher::AttachEngine3D
  Height = 2.4
  Length = 16
  Placement = pos=(87,28,2.3) rot=(0,0,1;0rad)
  Width = 7
FEATURE [Part::Box] Box012  label="frontCaseScrewPillarBracket001"
  AttacherType = Attacher::AttachEngine3D
  Height = 2.4
  Length = 16
  Placement = pos=(87,28,67.3) rot=(0,0,1;0rad)
  Width = 7
FEATURE [Sketcher::SketchObject] Sketch026
  FullyConstrained = true
  sketch-geometry (17):
    g0: Circle CenterX=-3.5 CenterY=23.5 CenterZ=0 NormalX=0 NormalY=0 NormalZ=1 AngleXU=0 Radius=1
    g1: Circle CenterX=-1 CenterY=15.25 CenterZ=0 NormalX=0 NormalY=0 NormalZ=1 AngleXU=0 Radius=1
    g2: Circle CenterX=-3.5 CenterY=7 CenterZ=0 NormalX=0 NormalY=0 NormalZ=1 AngleXU=0 Radius=1
    g3: BSplineCurve PolesCount=3 KnotsCount=2 Degree=2 IsPeriodic=0
    g4: GeomPoint X=-3.5 Y=23.5 Z=0
    g5: GeomPoint X=-3.5 Y=7 Z=0
    g6: Circle CenterX=-4.8 CenterY=30.5 CenterZ=0 NormalX=0 NormalY=0 NormalZ=1 AngleXU=0 Radius=1
    g7: Circle CenterX=-3.5 CenterY=30.5 CenterZ=0 NormalX=0 NormalY=0 NormalZ=1 AngleXU=0 Radius=1
    g8: Circle CenterX=-3.5 CenterY=29.2 CenterZ=0 NormalX=0 NormalY=0 NormalZ=1 AngleXU=0 Radius=1
    g9: BSplineCurve PolesCount=3 KnotsCount=2 Degree=2 IsPeriodic=0
    g10: GeomPoint X=-4.8 Y=30.5 Z=0
    g11: GeomPoint X=-3.5 Y=29.2 Z=0
    g12: LineSegment StartX=-3.5 StartY=29.2 StartZ=0 EndX=-3.5 EndY=23.5 EndZ=0
    g13: LineSegment StartX=-4.8 StartY=30.5 StartZ=0 EndX=0 EndY=30.5 EndZ=0
    g14: LineSegment StartX=-3.5 StartY=5 StartZ=0 EndX=-3.5 EndY=7 EndZ=0
    g15: LineSegment StartX=0 StartY=5 StartZ=0 EndX=0 EndY=30.5 EndZ=0
    g16: LineSegment StartX=-3.5 StartY=5 StartZ=0 EndX=0 EndY=5 EndZ=0
  constraints (33):
    c: Weight(g0) = 1
    c: Equal(g0,g1)
    c: Equal(g0,g2)
    c: InternalAlignment(g0,g3)
    c: InternalAlignment(g1,g3)
    c: InternalAlignment(g2,g3)
    c: InternalAlignment(g4,g3)
    c: InternalAlignment(g5,g3)
    c: Block(g3)
    c: Weight(g6) = 1
    c: Equal(g6,g7)
    c: Equal(g6,g8)
    c: InternalAlignment(g6,g9)
    c: InternalAlignment(g7,g9)
    c: InternalAlignment(g8,g9)
    c: InternalAlignment(g10,g9)
    c: InternalAlignment(g11,g9)
    c: Block(g9)
    c: Coincident(g12,g9)
    c: Coincident(g12,g3)
    c: Vertical(g12)
    c: Coincident(g13,g9)
    c: Horizontal(g13)
    c: Distance(g13) = 4.8
    c: Coincident(g14,g3)
    c: Vertical(g14)
    c: Coincident(g15,g13)
    c: Vertical(g15)
    c: Tangent(g15,g1)
    c: Distance(g14) = 2
    c: Coincident(g16,g14)
    c: Horizontal(g16)
    c: Coincident(g15,g16)
FEATURE [Part::Feature] Face050
  shape: bbox 4.8 x 25.5 x 2e-07 mm, 1 faces, 0 solids (baked)
FEATURE [Part::Revolution] Revolve054  label="moreFrontCaseScrewPost001"
  Angle = 360
  Axis = (0,1,0)
  Base = (0,0,0)
  FaceMakerClass = Part::FaceMakerBullseye
  Placement = pos=(102.5,4.5,3.5) rot=(0,0,1;0rad)
  Solid = false
  Source = -> Face050
  Symmetric = false
FEATURE [Part::Feature] Face051
  shape: bbox 4.8 x 25.5 x 2e-07 mm, 1 faces, 0 solids (baked)
FEATURE [Part::Revolution] Revolve055  label="moreFrontCaseScrewPost002"
  Angle = 360
  Axis = (0,1,0)
  Base = (0,0,0)
  FaceMakerClass = Part::FaceMakerBullseye
  Placement = pos=(102.5,4.5,68.5) rot=(0,0,1;0rad)
  Solid = false
  Source = -> Face051
  Symmetric = false
FEATURE [Sketcher::SketchObject] Sketch027
  FullyConstrained = true
  sketch-geometry (10):
    g0: LineSegment StartX=-1.6 StartY=4.7 StartZ=0 EndX=-1.6 EndY=1.7 EndZ=0
    g1: LineSegment StartX=-3.5 StartY=4.7 StartZ=0 EndX=-1.6 EndY=4.7 EndZ=0
    g2: LineSegment StartX=-1.6 StartY=1.7 StartZ=0 EndX=-1.6 EndY=1.5 EndZ=0
    g3: LineSegment StartX=-1.6 StartY=1.5 StartZ=0 EndX=-5.2 EndY=1.5 EndZ=0
    g4: Circle CenterX=-3.5 CenterY=4.7 CenterZ=0 NormalX=0 NormalY=0 NormalZ=1 AngleXU=0 Radius=1
    g5: Circle CenterX=-3.59627 CenterY=2.99743 CenterZ=0 NormalX=0 NormalY=0 NormalZ=1 AngleXU=0 Radius=1
    g6: Circle CenterX=-5.2 CenterY=1.5 CenterZ=0 NormalX=0 NormalY=0 NormalZ=1 AngleXU=0 Radius=1
    g7: BSplineCurve PolesCount=3 KnotsCount=2 Degree=2 IsPeriodic=0
    g8: GeomPoint X=-3.5 Y=4.7 Z=0
    g9: GeomPoint X=-5.2 Y=1.5 Z=0
  constraints (23):
    c: Vertical(g0)
    c: Distance(g0) = 3
    c: Coincident(g1,g0)
    c: Horizontal(g1)
    c: Block(g0)
    c: Block(g1)
    c: Coincident(g2,g0)
    c: Vertical(g2)
    c: Distance(g2) = 0.2
    c: Coincident(g3,g2)
    c: Horizontal(g3)
    c: Block(g3)
    c: Coincident(g7,g1)
    c: Weight(g4) = 1
    c: Equal(g4,g5)
    c: Equal(g4,g6)
    c: Coincident(g7,g3)
    c: InternalAlignment(g4,g7)
    c: InternalAlignment(g5,g7)
    c: InternalAlignment(g6,g7)
    c: InternalAlignment(g8,g7)
    c: InternalAlignment(g9,g7)
    c: Block(g7)
FEATURE [Sketcher::SketchObject] Sketch028
  FullyConstrained = true
  sketch-geometry (18):
    g0: LineSegment StartX=0 StartY=3e-16 StartZ=0 EndX=0 EndY=1.7 EndZ=0
    g1: LineSegment StartX=-3.5 StartY=0 StartZ=0 EndX=-3.5 EndY=0.9 EndZ=0
    g2: Circle CenterX=-2.7 CenterY=1.7 CenterZ=0 NormalX=0 NormalY=0 NormalZ=1 AngleXU=0 Radius=1
    g3: Circle CenterX=-3.5 CenterY=1.7 CenterZ=0 NormalX=0 NormalY=0 NormalZ=1 AngleXU=0 Radius=1
    g4: Circle CenterX=-3.5 CenterY=0.9 CenterZ=0 NormalX=0 NormalY=0 NormalZ=1 AngleXU=0 Radius=1
    g5: BSplineCurve PolesCount=3 KnotsCount=2 Degree=2 IsPeriodic=0
    g6: GeomPoint X=-2.7 Y=1.7 Z=0
    g7: GeomPoint X=-3.5 Y=0.9 Z=0
    g8: LineSegment StartX=-3.5 StartY=0 StartZ=0 EndX=-3.5 EndY=-7 EndZ=0
    g9: LineSegment StartX=0 StartY=3e-16 StartZ=0 EndX=0 EndY=-7 EndZ=0
    g10: LineSegment StartX=-3.5 StartY=-7 StartZ=0 EndX=0 EndY=-7 EndZ=0
    g11: LineSegment StartX=-2.7 StartY=1.7 StartZ=0 EndX=-1.6 EndY=1.7 EndZ=0
    g12: LineSegment StartX=0 StartY=1.7 StartZ=0 EndX=0 EndY=4.5 EndZ=0
    g13: LineSegment StartX=0 StartY=4.5 StartZ=0 EndX=0 EndY=10.8 EndZ=0
    g14: LineSegment StartX=0 StartY=10.8 StartZ=0 EndX=-2 EndY=10.8 EndZ=0
    g15: LineSegment StartX=-1.6 StartY=4.7 StartZ=0 EndX=-1.6 EndY=1.7 EndZ=0
    g16: LineSegment StartX=-1.6 StartY=4.7 StartZ=0 EndX=-2 EndY=4.7 EndZ=0
    g17: LineSegment StartX=-2 StartY=4.7 StartZ=0 EndX=-2 EndY=10.8 EndZ=0
  constraints (44):
    c: Vertical(g0)
    c: Vertical(g1)
    c: Distance(g1) = 0.9
    c: Block(g0)
    c: Distance(g0) = 1.7
    c: Weight(g2) = 1
    c: Equal(g2,g3)
    c: Equal(g2,g4)
    c: Coincident(g5,g1)
    c: InternalAlignment(g2,g5)
    c: InternalAlignment(g3,g5)
    c: InternalAlignment(g4,g5)
    c: InternalAlignment(g6,g5)
    c: InternalAlignment(g7,g5)
    c: Block(g5)
    c: Coincident(g8,g1)
    c: Vertical(g8)
    c: Distance(g8) = 7
    c: Vertical(g9)
    c: Equal(g8,g9) = 7
    c: Coincident(g9,g0)
    c: Coincident(g10,g8)
    c: Coincident(g10,g9)
    c: Horizontal(g10)
    c: Coincident(g11,g5)
    c: Horizontal(g11)
    c: Coincident(g12,g0)
    c: Vertical(g12)
    c: Distance(g12) = 2.8
    c: Coincident(g13,g12)
    c: Vertical(g13)
    c: Distance(g13) = 6.3
    c: Coincident(g14,g13)
    c: Horizontal(g14)
    c: Distance(g14) = 2
    c: Vertical(g15)
    c: Distance(g15) = 3
    c: Block(g11)
    c: Coincident(g15,g11)
    c: Coincident(g16,g15)
    c: Horizontal(g16)
    c: Coincident(g17,g16)
    c: Coincident(g17,g14)
    c: Vertical(g17)
FEATURE [Part::Revolution] Revolve040  label="backCaseScrewRetainer001"
  Angle = 360
  Axis = (0,1,0)
  Base = (0,0,0)
  FaceMakerClass = Part::FaceMakerBullseye
  Placement = pos=(12.5,3,10) rot=(0,0,1;0rad)
  Solid = false
  Source = -> Face036
  Symmetric = false
FEATURE [Part::Feature] Face055
  shape: bbox 3.5 x 30.2 x 2e-07 mm, 1 faces, 0 solids (baked)
FEATURE [Part::Revolution] Revolve059  label="backCaseScrewPost"
  Angle = 360
  Axis = (0,1,0)
  Base = (0,0,0)
  FaceMakerClass = Part::FaceMakerBullseye
  Placement = pos=(12.5,4.5,10) rot=(0,0,1;0rad)
  Solid = false
  Source = -> Face055
  Symmetric = false
FEATURE [Part::Feature] Face056
  shape: bbox 3.5 x 30.2 x 2e-07 mm, 1 faces, 0 solids (baked)
FEATURE [Part::Revolution] Revolve060  label="backCaseScrewPost001"
  Angle = 360
  Axis = (0,1,0)
  Base = (0,0,0)
  FaceMakerClass = Part::FaceMakerBullseye
  Placement = pos=(12.5,4.5,62) rot=(0,0,1;0rad)
  Solid = false
  Source = -> Face056
  Symmetric = false
FEATURE [Part::Feature] Face057
  shape: bbox 3.5 x 17.8 x 2e-07 mm, 1 faces, 0 solids (baked)
FEATURE [Part::Revolution] Revolve061  label="removeToCreateScrewAndThreadedInsertHole"
  Angle = 360
  Axis = (0,1,0)
  Base = (0,0,0)
  FaceMakerClass = Part::FaceMakerBullseye
  Placement = pos=(12.5,0,10) rot=(0,0,1;0rad)
  Solid = false
  Source = -> Face057
  Symmetric = false
FEATURE [Part::Feature] Face058
  shape: bbox 3.5 x 17.8 x 2e-07 mm, 1 faces, 0 solids (baked)
FEATURE [Part::Revolution] Revolve062  label="removeToCreateScrewAndThreadedInsertHole001"
  Angle = 360
  Axis = (0,1,0)
  Base = (0,0,0)
  FaceMakerClass = Part::FaceMakerBullseye
  Placement = pos=(12.5,0,62) rot=(0,0,1;0rad)
  Solid = false
  Source = -> Face058
  Symmetric = false
FEATURE [Part::Feature] Face059
  shape: bbox 3.5 x 17.8 x 2e-07 mm, 1 faces, 0 solids (baked)
FEATURE [Part::Revolution] Revolve063  label="removeToCreateScrewAndThreadedInsertHole002"
  Angle = 360
  Axis = (0,1,0)
  Base = (0,0,0)
  FaceMakerClass = Part::FaceMakerBullseye
  Placement = pos=(89.5,0,68.5) rot=(0,0,1;0rad)
  Solid = false
  Source = -> Face059
  Symmetric = false
FEATURE [Part::Feature] Face060
  shape: bbox 3.5 x 17.8 x 2e-07 mm, 1 faces, 0 solids (baked)
FEATURE [Part::Revolution] Revolve064  label="removeToCreateScrewAndThreadedInsertHole003"
  Angle = 360
  Axis = (0,1,0)
  Base = (0,0,0)
  FaceMakerClass = Part::FaceMakerBullseye
  Placement = pos=(89.5,0,3.5) rot=(0,0,1;0rad)
  Solid = false
  Source = -> Face060
  Symmetric = false
FEATURE [Part::Feature] Face061
  shape: bbox 3.5 x 17.8 x 2e-07 mm, 1 faces, 0 solids (baked)
FEATURE [Part::Revolution] Revolve065  label="removeToCreateScrewAndThreadedInsertHole004"
  Angle = 360
  Axis = (0,1,0)
  Base = (0,0,0)
  FaceMakerClass = Part::FaceMakerBullseye
  Placement = pos=(102.5,4.7,3.5) rot=(0,0,1;0rad)
  Solid = false
  Source = -> Face061
  Symmetric = false
FEATURE [Part::Feature] Face062
  shape: bbox 3.5 x 17.8 x 2e-07 mm, 1 faces, 0 solids (baked)
FEATURE [Part::Revolution] Revolve066  label="removeToCreateScrewAndThreadedInsertHole005"
  Angle = 360
  Axis = (0,1,0)
  Base = (0,0,0)
  FaceMakerClass = Part::FaceMakerBullseye
  Placement = pos=(102.5,4.7,68.5) rot=(0,0,1;0rad)
  Solid = false
  Source = -> Face062
  Symmetric = false
FEATURE [Part::MultiFuse] Fusion047  label="makeHoles"
  Shapes = -> [Revolve066,Revolve065,Revolve064,Revolve063,Revolve062,Revolve061]
FEATURE [Part::Feature] Face063
  shape: bbox 3.6 x 3.2 x 2e-07 mm, 1 faces, 0 solids (baked)
FEATURE [Part::Revolution] Revolve067  label="moreFrontCaseScrewRetainer002"
  Angle = 360
  Axis = (0,1,0)
  Base = (0,0,0)
  FaceMakerClass = Part::FaceMakerBullseye
  Placement = pos=(102.5,4.5,68.5) rot=(0,0,1;0rad)
  Solid = false
  Source = -> Face063
  Symmetric = false
FEATURE [Part::Feature] Face064
  shape: bbox 3.6 x 3.2 x 2e-07 mm, 1 faces, 0 solids (baked)
FEATURE [Part::Revolution] Revolve068  label="moreFrontCaseScrewRetainer003"
  Angle = 360
  Axis = (0,1,0)
  Base = (0,0,0)
  FaceMakerClass = Part::FaceMakerBullseye
  Placement = pos=(102.5,4.5,3.5) rot=(0,0,1;0rad)
  Solid = false
  Source = -> Face064
  Symmetric = false
FEATURE [Part::Feature] Face065
  shape: bbox 3.5 x 17.8 x 2e-07 mm, 1 faces, 0 solids (baked)
FEATURE [Part::Revolution] Revolve069  label="removeToCreateScrewAndThreadedInsertHole006"
  Angle = 360
  Axis = (0,1,0)
  Base = (0,0,0)
  FaceMakerClass = Part::FaceMakerBullseye
  Placement = pos=(12.5,0,10) rot=(0,0,1;0rad)
  Solid = false
  Source = -> Face065
  Symmetric = false
FEATURE [Part::Feature] Face066
  shape: bbox 3.5 x 17.8 x 2e-07 mm, 1 faces, 0 solids (baked)
FEATURE [Part::Revolution] Revolve070  label="removeToCreateScrewAndThreadedInsertHole007"
  Angle = 360
  Axis = (0,1,0)
  Base = (0,0,0)
  FaceMakerClass = Part::FaceMakerBullseye
  Placement = pos=(12.5,0,62) rot=(0,0,1;0rad)
  Solid = false
  Source = -> Face066
  Symmetric = false
FEATURE [Part::Feature] Face067
  shape: bbox 3.5 x 17.8 x 2e-07 mm, 1 faces, 0 solids (baked)
FEATURE [Part::Revolution] Revolve071  label="removeToCreateScrewAndThreadedInsertHole008"
  Angle = 360
  Axis = (0,1,0)
  Base = (0,0,0)
  FaceMakerClass = Part::FaceMakerBullseye
  Placement = pos=(89.5,0,68.5) rot=(0,0,1;0rad)
  Solid = false
  Source = -> Face067
  Symmetric = false
FEATURE [Part::Feature] Face068
  shape: bbox 3.5 x 17.8 x 2e-07 mm, 1 faces, 0 solids (baked)
FEATURE [Part::Revolution] Revolve072  label="removeToCreateScrewAndThreadedInsertHole009"
  Angle = 360
  Axis = (0,1,0)
  Base = (0,0,0)
  FaceMakerClass = Part::FaceMakerBullseye
  Placement = pos=(89.5,0,3.5) rot=(0,0,1;0rad)
  Solid = false
  Source = -> Face068
  Symmetric = false
FEATURE [Part::Feature] Face069
  shape: bbox 3.5 x 17.8 x 2e-07 mm, 1 faces, 0 solids (baked)
FEATURE [Part::Feature] Face070
  shape: bbox 3.5 x 17.8 x 2e-07 mm, 1 faces, 0 solids (baked)
FEATURE [Part::Revolution] Revolve073  label="removeToCreateScrewAndThreadedInsertHole010"
  Angle = 360
  Axis = (0,1,0)
  Base = (0,0,0)
  FaceMakerClass = Part::FaceMakerBullseye
  Placement = pos=(102.5,4.7,3.5) rot=(0,0,1;0rad)
  Solid = false
  Source = -> Face069
  Symmetric = false
FEATURE [Part::Revolution] Revolve074  label="removeToCreateScrewAndThreadedInsertHole011"
  Angle = 360
  Axis = (0,1,0)
  Base = (0,0,0)
  FaceMakerClass = Part::FaceMakerBullseye
  Placement = pos=(102.5,4.7,68.5) rot=(0,0,1;0rad)
  Solid = false
  Source = -> Face070
  Symmetric = false
FEATURE [Part::MultiFuse] Fusion048  label="makeHoles001"
  Shapes = -> [Revolve074,Revolve073,Revolve072,Revolve071,Revolve070,Revolve069]
FEATURE [Part::MultiFuse] Fusion049  label="caseScrewRetainers"
  Shapes = -> [Revolve067,Revolve068,Revolve048,Revolve047,Revolve039,Revolve040]
FEATURE [Part::Cut] Cut015  label="caseScrewRetainers001"
  Base = -> Fusion049
  Tool = -> Fusion048
FEATURE [Part::MultiFuse] Fusion050  label="casePillars"
  Shapes = -> [Revolve055,Revolve054,Revolve043,Revolve046,Revolve059,Revolve060]
FEATURE [Part::Feature] Face071 .. Face076  x6 (patterned run collapsed; names and placements below)
  shape: bbox 3.5 x 17.8 x 2e-07 mm, 1 faces, 0 solids (baked)
FEATURE [Part::Revolution] Revolve075  label="removeToCreateScrewAndThreadedInsertHole012"
  Angle = 360
  Axis = (0,1,0)
  Base = (0,0,0)
  FaceMakerClass = Part::FaceMakerBullseye
  Placement = pos=(12.5,0,10) rot=(0,0,1;0rad)
  Solid = false
  Source = -> Face071
  Symmetric = false
FEATURE [Part::Revolution] Revolve076  label="removeToCreateScrewAndThreadedInsertHole013"
  Angle = 360
  Axis = (0,1,0)
  Base = (0,0,0)
  FaceMakerClass = Part::FaceMakerBullseye
  Placement = pos=(12.5,0,62) rot=(0,0,1;0rad)
  Solid = false
  Source = -> Face072
  Symmetric = false
FEATURE [Part::Revolution] Revolve077  label="removeToCreateScrewAndThreadedInsertHole014"
  Angle = 360
  Axis = (0,1,0)
  Base = (0,0,0)
  FaceMakerClass = Part::FaceMakerBullseye
  Placement = pos=(89.5,0,68.5) rot=(0,0,1;0rad)
  Solid = false
  Source = -> Face073
  Symmetric = false
FEATURE [Part::Revolution] Revolve078  label="removeToCreateScrewAndThreadedInsertHole015"
  Angle = 360
  Axis = (0,1,0)
  Base = (0,0,0)
  FaceMakerClass = Part::FaceMakerBullseye
  Placement = pos=(89.5,0,3.5) rot=(0,0,1;0rad)
  Solid = false
  Source = -> Face074
  Symmetric = false
FEATURE [Part::Revolution] Revolve079  label="removeToCreateScrewAndThreadedInsertHole016"
  Angle = 360
  Axis = (0,1,0)
  Base = (0,0,0)
  FaceMakerClass = Part::FaceMakerBullseye
  Placement = pos=(102.5,4.7,3.5) rot=(0,0,1;0rad)
  Solid = false
  Source = -> Face075
  Symmetric = false
FEATURE [Part::Revolution] Revolve080  label="removeToCreateScrewAndThreadedInsertHole017"
  Angle = 360
  Axis = (0,1,0)
  Base = (0,0,0)
  FaceMakerClass = Part::FaceMakerBullseye
  Placement = pos=(102.5,4.7,68.5) rot=(0,0,1;0rad)
  Solid = false
  Source = -> Face076
  Symmetric = false
FEATURE [Part::MultiFuse] Fusion051  label="makeHoles002"
  Shapes = -> [Revolve080,Revolve079,Revolve078,Revolve077,Revolve076,Revolve075]
FEATURE [Part::Cut] Cut016  label="caesPillars"
  Base = -> Fusion050
  Tool = -> Fusion051
FEATURE [Part::Revolution] Revolve009  label="plugHousing016"
  Angle = 360
  Axis = (0,1,0)
  Base = (0,0,0)
  FaceMakerClass = Part::FaceMakerBullseye
  Placement = pos=(0,0,36.15) rot=(0,0,1;0rad)
  Solid = false
  Source = -> Face012
  Symmetric = false
FEATURE [Part::MultiFuse] Fusion014  label="plugHousing023"
  Placement = pos=(0,0,0) rot=(0,0,1;1.5708rad)
  Shapes = -> [Revolve011,Revolve009]
FEATURE [Part::Revolution] Revolve010  label="plugHousing017"
  Angle = 360
  Axis = (0,1,0)
  Base = (0,0,0)
  FaceMakerClass = Part::FaceMakerBullseye
  Placement = pos=(0,0,36.15) rot=(0,0,1;0rad)
  Solid = false
  Source = -> Face014
  Symmetric = false
FEATURE [Part::MultiFuse] Fusion015  label="plugHousing024"
  Placement = pos=(0,0,0) rot=(0,0,1;1.5708rad)
  Shapes = -> [Revolve010,Revolve015]
FEATURE [Part::Revolution] Revolve014  label="plugHousing026"
  Angle = 360
  Axis = (0,1,0)
  Base = (0,0,0)
  FaceMakerClass = Part::FaceMakerBullseye
  Placement = pos=(0,0,36.15) rot=(0,0,1;0rad)
  Solid = false
  Source = -> Face011
  Symmetric = false
FEATURE [Part::Revolution] Revolve013  label="plugHousing025"
  Angle = 360
  Axis = (0,1,0)
  Base = (0,0,0)
  FaceMakerClass = Part::FaceMakerBullseye
  Placement = pos=(0,0,36.15) rot=(0,0,1;0rad)
  Solid = false
  Source = -> Face015
  Symmetric = false
FEATURE [Part::MultiFuse] Fusion016  label="plugHousing028"
  Placement = pos=(0,19,0) rot=(0,0,1;3.14159rad)
  Shapes = -> [Fusion014,Fusion013]
FEATURE [Part::MultiFuse] Fusion011  label="plugHousing018"
  Placement = pos=(0,0,0) rot=(0,0,1;1.5708rad)
  Shapes = -> [Revolve014,Revolve013]
FEATURE [Part::MultiFuse] Fusion012  label="plugHousing019"
  Placement = pos=(0,19,0) rot=(0,0,1;3.14159rad)
  Shapes = -> [Fusion011,Fusion015]
FEATURE [Part::MultiFuse] Fusion017  label="plugHousing029"
  Placement = pos=(122.621,0,-0.15) rot=(0,0,1;0rad)
  Shapes = -> [Fusion016,Fusion012]
FEATURE [Part::MultiFuse] Fusion052  label="casePillarRetainers"
  Shapes = -> [Extrude012,Extrude013,Extrude014,Extrude015,Extrude016,Extrude017,Extrude018,Extrude019,Box011,Box012]
FEATURE [Part::Feature] Face077
  shape: bbox 3.5 x 17.8 x 2e-07 mm, 1 faces, 0 solids (baked)
FEATURE [Part::Revolution] Revolve081  label="removeToCreateScrewAndThreadedInsertHole018"
  Angle = 360
  Axis = (0,1,0)
  Base = (0,0,0)
  FaceMakerClass = Part::FaceMakerBullseye
  Placement = pos=(62.3,30.3,19.7) rot=(0,0,1;0rad)
  Solid = false
  Source = -> Face077
  Symmetric = false
FEATURE [Part::Feature] Face078
  shape: bbox 3.5 x 17.8 x 2e-07 mm, 1 faces, 0 solids (baked)
FEATURE [Part::Revolution] Revolve082  label="removeToCreateScrewAndThreadedInsertHole019"
  Angle = 360
  Axis = (0,1,0)
  Base = (0,0,0)
  FaceMakerClass = Part::FaceMakerBullseye
  Placement = pos=(62.3,30.3,51.7) rot=(0,0,1;0rad)
  Solid = false
  Source = -> Face078
  Symmetric = false
FEATURE [Part::Feature] Face079
  shape: bbox 3.5 x 17.8 x 2e-07 mm, 1 faces, 0 solids (baked)
FEATURE [Part::Revolution] Revolve083  label="removeToCreateScrewAndThreadedInsertHole020"
  Angle = 360
  Axis = (0,1,0)
  Base = (0,0,0)
  FaceMakerClass = Part::FaceMakerBullseye
  Placement = pos=(30.3,30.3,19.7) rot=(0,0,1;0rad)
  Solid = false
  Source = -> Face079
  Symmetric = false
FEATURE [Part::Feature] Face080
  shape: bbox 3.5 x 17.8 x 2e-07 mm, 1 faces, 0 solids (baked)
FEATURE [Part::Revolution] Revolve084  label="removeToCreateScrewAndThreadedInsertHole021"
  Angle = 360
  Axis = (0,1,0)
  Base = (0,0,0)
  FaceMakerClass = Part::FaceMakerBullseye
  Placement = pos=(30.3,30.3,51.7) rot=(0,0,1;0rad)
  Solid = false
  Source = -> Face080
  Symmetric = false
FEATURE [Part::MultiFuse] Fusion053  label="createThreadedInsertHolesForFan"
  Shapes = -> [Revolve081,Revolve082,Revolve083,Revolve084]
FEATURE [Part::Cut] Cut017  label="fanScrewHousing001"
  Base = -> Fusion046
  Tool = -> Fusion053
FEATURE [Part::Feature] Face081
  shape: bbox 3.5 x 17.8 x 2e-07 mm, 1 faces, 0 solids (baked)
FEATURE [Part::Revolution] Revolve085  label="removeToCreateScrewAndThreadedInsertHole022"
  Angle = 360
  Axis = (0,1,0)
  Base = (0,0,0)
  FaceMakerClass = Part::FaceMakerBullseye
  Placement = pos=(62.3,30.3,19.7) rot=(0,0,1;0rad)
  Solid = false
  Source = -> Face081
  Symmetric = false
FEATURE [Part::Feature] Face082
  shape: bbox 3.5 x 17.8 x 2e-07 mm, 1 faces, 0 solids (baked)
FEATURE [Part::Revolution] Revolve086  label="removeToCreateScrewAndThreadedInsertHole023"
  Angle = 360
  Axis = (0,1,0)
  Base = (0,0,0)
  FaceMakerClass = Part::FaceMakerBullseye
  Placement = pos=(62.3,30.3,51.7) rot=(0,0,1;0rad)
  Solid = false
  Source = -> Face082
  Symmetric = false
FEATURE [Part::Feature] Face083
  shape: bbox 3.5 x 17.8 x 2e-07 mm, 1 faces, 0 solids (baked)
FEATURE [Part::Revolution] Revolve087  label="removeToCreateScrewAndThreadedInsertHole024"
  Angle = 360
  Axis = (0,1,0)
  Base = (0,0,0)
  FaceMakerClass = Part::FaceMakerBullseye
  Placement = pos=(30.3,30.3,19.7) rot=(0,0,1;0rad)
  Solid = false
  Source = -> Face083
  Symmetric = false
FEATURE [Part::Feature] Face084
  shape: bbox 3.5 x 17.8 x 2e-07 mm, 1 faces, 0 solids (baked)
FEATURE [Part::Revolution] Revolve088  label="removeToCreateScrewAndThreadedInsertHole025"
  Angle = 360
  Axis = (0,1,0)
  Base = (0,0,0)
  FaceMakerClass = Part::FaceMakerBullseye
  Placement = pos=(30.3,30.3,51.7) rot=(0,0,1;0rad)
  Solid = false
  Source = -> Face084
  Symmetric = false
FEATURE [Part::MultiFuse] Fusion054  label="createThreadedInsertHolesForFan001"
  Shapes = -> [Revolve085,Revolve086,Revolve087,Revolve088]
FEATURE [Part::Cut] Cut018  label="top007"
  Base = -> Fusion040
  Tool = -> Fusion054
FEATURE [Sketcher::SketchObject] Sketch029
  FullyConstrained = false
  Placement = pos=(0,0,0) rot=(1,0,0;1.5708rad)
  sketch-geometry (24):
    g0: ArcOfCircle CenterX=-4 CenterY=-10.5 CenterZ=0 NormalX=0 NormalY=0 NormalZ=1 AngleXU=0 Radius=1.5 StartAngle=6e-16 EndAngle=3.14159
    g1: ArcOfCircle CenterX=-34.2 CenterY=-10.5 CenterZ=0 NormalX=0 NormalY=0 NormalZ=1 AngleXU=0 Radius=1.5 StartAngle=0 EndAngle=3.14159
    g2: ArcOfCircle CenterX=-34.2 CenterY=-27.7 CenterZ=0 NormalX=0 NormalY=0 NormalZ=1 AngleXU=0 Radius=1.5 StartAngle=3.14159 EndAngle=6.28319
    g3: ArcOfCircle CenterX=-4 CenterY=-27.7 CenterZ=0 NormalX=0 NormalY=0 NormalZ=1 AngleXU=0 Radius=1.5 StartAngle=3.1416 EndAngle=6.28319
    g4: ArcOfCircle CenterX=-10 CenterY=-4.3 CenterZ=0 NormalX=0 NormalY=0 NormalZ=1 AngleXU=0 Radius=1.5 StartAngle=2e-16 EndAngle=3.14159
    g5: ArcOfCircle CenterX=-16.1 CenterY=-1.8 CenterZ=0 NormalX=0 NormalY=0 NormalZ=1 AngleXU=0 Radius=1.5 StartAngle=5e-16 EndAngle=3.14159
    g6: ArcOfCircle CenterX=-22.1 CenterY=-1.8 CenterZ=0 NormalX=0 NormalY=0 NormalZ=1 AngleXU=0 Radius=1.5 StartAngle=5e-16 EndAngle=3.14159
    g7: ArcOfCircle CenterX=-28.2 CenterY=-4.3 CenterZ=0 NormalX=0 NormalY=0 NormalZ=1 AngleXU=0 Radius=1.5 StartAngle=2e-16 EndAngle=3.14159
    g8: ArcOfCircle CenterX=-10 CenterY=-33.9 CenterZ=0 NormalX=0 NormalY=0 NormalZ=1 AngleXU=0 Radius=1.5 StartAngle=3.14159 EndAngle=6.28319
    g9: ArcOfCircle CenterX=-16.1 CenterY=-36.4 CenterZ=0 NormalX=0 NormalY=0 NormalZ=1 AngleXU=0 Radius=1.5 StartAngle=3.14159 EndAngle=6.28319
    g10: ArcOfCircle CenterX=-22.1 CenterY=-36.4 CenterZ=0 NormalX=0 NormalY=0 NormalZ=1 AngleXU=0 Radius=1.5 StartAngle=3.14159 EndAngle=6.28319
    g11: ArcOfCircle CenterX=-28.2 CenterY=-33.9 CenterZ=0 NormalX=0 NormalY=0 NormalZ=1 AngleXU=0 Radius=1.5 StartAngle=3.14159 EndAngle=6.28319
    g12: LineSegment StartX=-35.7 StartY=-10.5 StartZ=0 EndX=-35.7 EndY=-27.7 EndZ=0
    g13: LineSegment StartX=-32.7 StartY=-10.5 StartZ=0 EndX=-32.7 EndY=-27.7 EndZ=0
    g14: LineSegment StartX=-29.7 StartY=-33.9 StartZ=0 EndX=-29.7 EndY=-4.3 EndZ=0
    g15: LineSegment StartX=-26.7 StartY=-33.9 StartZ=0 EndX=-26.7 EndY=-4.3 EndZ=0
    g16: LineSegment StartX=-2.5 StartY=-10.5 StartZ=0 EndX=-2.5 EndY=-27.7 EndZ=0
    g17: LineSegment StartX=-8.5 StartY=-4.3 StartZ=0 EndX=-8.5 EndY=-33.9 EndZ=0
    g18: LineSegment StartX=-5.5 StartY=-10.5 StartZ=0 EndX=-5.5 EndY=-27.7 EndZ=0
    g19: LineSegment StartX=-11.5 StartY=-4.3 StartZ=0 EndX=-11.5 EndY=-33.9 EndZ=0
    g20: LineSegment StartX=-14.6 StartY=-1.8 StartZ=0 EndX=-14.6 EndY=-36.4 EndZ=0
    g21: LineSegment StartX=-17.6 StartY=-1.8 StartZ=0 EndX=-17.6 EndY=-36.4 EndZ=0
    g22: LineSegment StartX=-20.6 StartY=-36.4 StartZ=0 EndX=-20.6 EndY=-1.8 EndZ=0
    g23: LineSegment StartX=-23.6 StartY=-1.8 StartZ=0 EndX=-23.6 EndY=-36.4 EndZ=0
  constraints (48):
    c: Block(g0)
    c: Block(g1)
    c: Block(g2)
    c: Block(g3)
    c: Block(g4)
    c: Block(g5)
    c: Block(g6)
    c: Block(g7)
    c: Block(g8)
    c: Block(g9)
    c: Block(g10)
    c: Block(g11)
    c: Coincident(g12,g1)
    c: Coincident(g12,g2)
    c: Vertical(g12)
    c: Coincident(g13,g1)
    c: Coincident(g13,g2)
    c: Vertical(g13)
    c: Coincident(g14,g11)
    c: Coincident(g14,g7)
    c: Vertical(g14)
    c: Coincident(g15,g11)
    c: Coincident(g15,g7)
    c: Vertical(g15)
    c: Coincident(g16,g0)
    c: Coincident(g16,g3)
    c: Vertical(g16)
    c: Coincident(g17,g4)
    c: Coincident(g17,g8)
    c: Vertical(g17)
    c: Coincident(g18,g0)
    c: Coincident(g18,g3)
    c: Vertical(g18)
    c: Coincident(g19,g4)
    c: Coincident(g19,g8)
    c: Vertical(g19)
    c: Coincident(g20,g5)
    c: Coincident(g20,g9)
    c: Vertical(g20)
    c: Coincident(g21,g5)
    c: Coincident(g21,g9)
    c: Vertical(g21)
    c: Coincident(g22,g10)
    c: Coincident(g22,g6)
    c: Vertical(g22)
    c: Coincident(g23,g6)
    c: Coincident(g23,g10)
    c: Vertical(g23)
FEATURE [Part::Extrusion] Extrude020  label="removeToCreateFanGrillHoles"
  Base = -> Sketch029
  Dir = (0,-1,6e-16)
  DirMode = 2
  FaceMakerClass = Part::FaceMakerBullseye
  LengthFwd = 10
  LengthRev = 0
  Placement = pos=(65.4,44,54.82) rot=(0,0,1;0rad)
  Solid = true
  Symmetric = false
FEATURE [Part::MultiFuse] Fusion055  label="top008"
  Shapes = -> [Cut017,Cut018]
FEATURE [Part::Cut] Cut019  label="top009"
  Base = -> Fusion055
  Tool = -> Extrude020
FEATURE [App::MeasureDistance] Distance003  label="Distance: 71.95 mm"
  Distance = 71.9513
  P1 = (117,38,72)
  P2 = (117,38,0.0487319)
FEATURE [Sketcher::SketchObject] Sketch030
  FullyConstrained = true
  Placement = pos=(117,19,0) rot=(0.57735,0.57735,0.57735;2.0944rad)
  sketch-geometry (48):
    g0: LineSegment StartX=-49.19 StartY=69.25 StartZ=0 EndX=-49.19 EndY=66.25 EndZ=0
    g1: LineSegment StartX=-49.19 StartY=63.5 StartZ=0 EndX=-49.19 EndY=60.5 EndZ=0
    g2: LineSegment StartX=-49.19 StartY=57.75 StartZ=0 EndX=-49.19 EndY=54.75 EndZ=0
    g3: LineSegment StartX=-49.19 StartY=52 StartZ=0 EndX=-49.19 EndY=49 EndZ=0
    g4: LineSegment StartX=-49.19 StartY=46.25 StartZ=0 EndX=-49.19 EndY=43.25 EndZ=0
    g5: LineSegment StartX=-49.19 StartY=40.5 StartZ=0 EndX=-49.19 EndY=37.5 EndZ=0
    g6: LineSegment StartX=-49.19 StartY=34.5 StartZ=0 EndX=-49.19 EndY=31.5 EndZ=0
    g7: LineSegment StartX=-49.19 StartY=28.75 StartZ=0 EndX=-49.19 EndY=25.75 EndZ=0
    g8: LineSegment StartX=-49.19 StartY=23 StartZ=0 EndX=-49.19 EndY=20 EndZ=0
    g9: LineSegment StartX=-49.19 StartY=17.25 StartZ=0 EndX=-49.19 EndY=14.25 EndZ=0
    g10: LineSegment StartX=-49.19 StartY=11.5 StartZ=0 EndX=-49.19 EndY=8.5 EndZ=0
    g11: LineSegment StartX=-49.19 StartY=5.75 StartZ=0 EndX=-49.19 EndY=2.75 EndZ=0
    g12: ArcOfCircle CenterX=-1.5 CenterY=67.75 CenterZ=0 NormalX=0 NormalY=0 NormalZ=1 AngleXU=0 Radius=1.5 StartAngle=4.71239 EndAngle=7.85398
    g13: ArcOfCircle CenterX=-1.5 CenterY=62 CenterZ=0 NormalX=0 NormalY=0 NormalZ=1 AngleXU=0 Radius=1.5 StartAngle=4.71239 EndAngle=7.85398
    g14: ArcOfCircle CenterX=-1.5 CenterY=56.25 CenterZ=0 NormalX=0 NormalY=0 NormalZ=1 AngleXU=0 Radius=1.5 StartAngle=4.71239 EndAngle=7.85398
    g15: ArcOfCircle CenterX=-11.49 CenterY=50.5 CenterZ=0 NormalX=0 NormalY=0 NormalZ=1 AngleXU=0 Radius=1.5 StartAngle=4.71239 EndAngle=7.85398
    g16: ArcOfCircle CenterX=-16.28 CenterY=44.75 CenterZ=0 NormalX=0 NormalY=0 NormalZ=1 AngleXU=0 Radius=1.5 StartAngle=4.71239 EndAngle=7.85398
    g17: ArcOfCircle CenterX=-18.2337 CenterY=39 CenterZ=0 NormalX=0 NormalY=0 NormalZ=1 AngleXU=0 Radius=1.5 StartAngle=4.71485 EndAngle=7.85398
    g18: ArcOfCircle CenterX=-16.2837 CenterY=27.25 CenterZ=0 NormalX=0 NormalY=0 NormalZ=1 AngleXU=0 Radius=1.5 StartAngle=4.71485 EndAngle=7.85398
    g19: ArcOfCircle CenterX=-18.2337 CenterY=33 CenterZ=0 NormalX=0 NormalY=0 NormalZ=1 AngleXU=0 Radius=1.5 StartAngle=4.71485 EndAngle=7.85398
    g20: ArcOfCircle CenterX=-11.49 CenterY=21.5 CenterZ=0 NormalX=0 NormalY=0 NormalZ=1 AngleXU=0 Radius=1.5 StartAngle=4.71239 EndAngle=7.85398
    g21: ArcOfCircle CenterX=-1.5 CenterY=4.25 CenterZ=0 NormalX=0 NormalY=0 NormalZ=1 AngleXU=0 Radius=1.5 StartAngle=4.71239 EndAngle=7.85398
    g22: ArcOfCircle CenterX=-1.5 CenterY=10 CenterZ=0 NormalX=0 NormalY=0 NormalZ=1 AngleXU=0 Radius=1.5 StartAngle=4.71239 EndAngle=7.85398
    g23: ArcOfCircle CenterX=-1.5 CenterY=15.75 CenterZ=0 NormalX=0 NormalY=0 NormalZ=1 AngleXU=0 Radius=1.5 StartAngle=4.71239 EndAngle=7.85398
    g24: LineSegment StartX=-49.19 StartY=69.25 StartZ=0 EndX=-1.5 EndY=69.25 EndZ=0
    g25: LineSegment StartX=-49.19 StartY=66.25 StartZ=0 EndX=-1.5 EndY=66.25 EndZ=0
    g26: LineSegment StartX=-49.19 StartY=63.5 StartZ=0 EndX=-1.5 EndY=63.5 EndZ=0
    g27: LineSegment StartX=-49.19 StartY=60.5 StartZ=0 EndX=-1.5 EndY=60.5 EndZ=0
    g28: LineSegment StartX=-49.19 StartY=57.75 StartZ=0 EndX=-1.5 EndY=57.75 EndZ=0
    g29: LineSegment StartX=-49.19 StartY=54.75 StartZ=0 EndX=-1.5 EndY=54.75 EndZ=0
    g30: LineSegment StartX=-49.19 StartY=52 StartZ=0 EndX=-11.49 EndY=52 EndZ=0
    g31: LineSegment StartX=-49.19 StartY=49 StartZ=0 EndX=-11.49 EndY=49 EndZ=0
    g32: LineSegment StartX=-49.19 StartY=46.25 StartZ=0 EndX=-16.28 EndY=46.25 EndZ=0
    g33: LineSegment StartX=-49.19 StartY=43.25 StartZ=0 EndX=-16.28 EndY=43.25 EndZ=0
    g34: LineSegment StartX=-49.19 StartY=40.5 StartZ=0 EndX=-18.2337 EndY=40.5 EndZ=0
    g35: LineSegment StartX=-49.19 StartY=37.5 StartZ=0 EndX=-18.23 EndY=37.5 EndZ=0
    g36: LineSegment StartX=-49.19 StartY=34.5 StartZ=0 EndX=-18.2337 EndY=34.5 EndZ=0
    g37: LineSegment StartX=-49.19 StartY=31.5 StartZ=0 EndX=-18.23 EndY=31.5 EndZ=0
    g38: LineSegment StartX=-49.19 StartY=28.75 StartZ=0 EndX=-16.2837 EndY=28.75 EndZ=0
    g39: LineSegment StartX=-49.19 StartY=25.75 StartZ=0 EndX=-16.28 EndY=25.75 EndZ=0
    g40: LineSegment StartX=-49.19 StartY=23 StartZ=0 EndX=-11.49 EndY=23 EndZ=0
    g41: LineSegment StartX=-49.19 StartY=20 StartZ=0 EndX=-11.49 EndY=20 EndZ=0
    g42: LineSegment StartX=-49.19 StartY=17.25 StartZ=0 EndX=-1.5 EndY=17.25 EndZ=0
    g43: LineSegment StartX=-49.19 StartY=14.25 StartZ=0 EndX=-1.5 EndY=14.25 EndZ=0
    g44: LineSegment StartX=-49.19 StartY=11.5 StartZ=0 EndX=-1.5 EndY=11.5 EndZ=0
    g45: LineSegment StartX=-49.19 StartY=8.5 StartZ=0 EndX=-1.5 EndY=8.5 EndZ=0
    g46: LineSegment StartX=-49.19 StartY=5.75 StartZ=0 EndX=-1.5 EndY=5.75 EndZ=0
    g47: LineSegment StartX=-49.19 StartY=2.75 StartZ=0 EndX=-1.5 EndY=2.75 EndZ=0
  constraints (120):
    c: Vertical(g0)
    c: Distance(g0) = 3
    c: Block(g0)
    c: Vertical(g1)
    c: Distance(g1) = 3
    c: Vertical(g2)
    c: Equal(g0,g2) = 3
    c: Block(g2)
    c: Vertical(g3)
    c: Equal(g1,g3) = 3
    c: Vertical(g4)
    c: Equal(g0,g4) = 3
    c: Block(g4)
    c: Vertical(g5)
    c: Equal(g1,g5) = 3
    c: Vertical(g6)
    c: Equal(g0,g6) = 3
    c: Block(g6)
    c: Vertical(g7)
    c: Equal(g1,g7) = 3
    c: Vertical(g8)
    c: Equal(g0,g8) = 3
    c: Block(g8)
    c: Vertical(g9)
    c: Equal(g1,g9) = 3
    c: Vertical(g10)
    c: Equal(g0,g10) = 3
    c: Block(g10)
    c: Vertical(g11)
    c: Equal(g1,g11) = 3
    c: Block(g12)
    c: Block(g13)
    c: Block(g14)
    c: Block(g15)
    c: Block(g16)
    c: Block(g17)
    c: Block(g18)
    c: Block(g19)
    c: Block(g20)
    c: Block(g21)
    c: Block(g22)
    c: Block(g23)
    c: Block(g11)
    c: Block(g9)
    c: Block(g7)
    c: Block(g5)
    c: Block(g3)
    c: Block(g1)
    c: Coincident(g24,g0)
    c: Coincident(g24,g12)
    c: Horizontal(g24)
    c: Coincident(g25,g0)
    c: Coincident(g25,g12)
    c: Horizontal(g25)
    c: Coincident(g26,g1)
    c: Coincident(g26,g13)
    c: Horizontal(g26)
    c: Coincident(g27,g1)
    c: Coincident(g27,g13)
    c: Horizontal(g27)
    c: Coincident(g28,g2)
    c: Coincident(g28,g14)
    c: Horizontal(g28)
    c: Coincident(g29,g2)
    c: Coincident(g29,g14)
    c: Horizontal(g29)
    c: Coincident(g30,g3)
    c: Coincident(g30,g15)
    c: Horizontal(g30)
    c: Coincident(g31,g3)
    c: Coincident(g31,g15)
    c: Horizontal(g31)
    c: Coincident(g32,g4)
    c: Coincident(g32,g16)
    c: Horizontal(g32)
    c: Coincident(g33,g4)
    c: Coincident(g33,g16)
    c: Horizontal(g33)
    c: Coincident(g34,g5)
    c: Coincident(g34,g17)
    c: Horizontal(g34)
    c: Coincident(g35,g5)
    c: Coincident(g35,g17)
    c: Horizontal(g35)
    c: Coincident(g36,g6)
    c: Coincident(g36,g19)
    c: Horizontal(g36)
    c: Coincident(g37,g6)
    c: Coincident(g37,g19)
    c: Horizontal(g37)
    c: Coincident(g38,g7)
    c: Coincident(g38,g18)
    c: Horizontal(g38)
    c: Coincident(g39,g7)
    c: Coincident(g39,g18)
    c: Horizontal(g39)
    c: Coincident(g40,g8)
    c: Coincident(g40,g20)
    c: Horizontal(g40)
    c: Coincident(g41,g8)
    c: Coincident(g41,g20)
    c: Horizontal(g41)
    c: Coincident(g42,g9)
    c: Coincident(g42,g23)
    c: Horizontal(g42)
    c: Coincident(g43,g9)
    c: Coincident(g43,g23)
    c: Horizontal(g43)
    c: Coincident(g44,g10)
    c: Coincident(g44,g22)
    c: Horizontal(g44)
    c: Coincident(g45,g10)
    c: Coincident(g45,g22)
    c: Horizontal(g45)
    c: Coincident(g46,g11)
    c: Coincident(g46,g21)
    c: Horizontal(g46)
    c: Coincident(g47,g11)
    c: Coincident(g47,g21)
    c: Horizontal(g47)
FEATURE [Sketcher::SketchObject] Sketch031
  FullyConstrained = true
  Placement = pos=(117,19,0) rot=(0.57735,0.57735,0.57735;2.0944rad)
  sketch-geometry (24):
    g0: ArcOfCircle CenterX=-49.19 CenterY=67.75 CenterZ=0 NormalX=0 NormalY=0 NormalZ=1 AngleXU=0 Radius=1.5 StartAngle=1.5708 EndAngle=4.71239
    g1: ArcOfCircle CenterX=-49.19 CenterY=62 CenterZ=0 NormalX=0 NormalY=0 NormalZ=1 AngleXU=0 Radius=1.5 StartAngle=1.5708 EndAngle=4.71239
    g2: ArcOfCircle CenterX=-49.19 CenterY=56.25 CenterZ=0 NormalX=0 NormalY=0 NormalZ=1 AngleXU=0 Radius=1.5 StartAngle=1.5708 EndAngle=4.71239
    g3: ArcOfCircle CenterX=-49.19 CenterY=50.5 CenterZ=0 NormalX=0 NormalY=0 NormalZ=1 AngleXU=0 Radius=1.5 StartAngle=1.5708 EndAngle=4.71239
    g4: ArcOfCircle CenterX=-49.19 CenterY=44.75 CenterZ=0 NormalX=0 NormalY=0 NormalZ=1 AngleXU=0 Radius=1.5 StartAngle=1.5708 EndAngle=4.71239
    g5: ArcOfCircle CenterX=-49.19 CenterY=39 CenterZ=0 NormalX=0 NormalY=0 NormalZ=1 AngleXU=0 Radius=1.5 StartAngle=1.5708 EndAngle=4.71239
    g6: ArcOfCircle CenterX=-49.19 CenterY=33 CenterZ=0 NormalX=0 NormalY=0 NormalZ=1 AngleXU=0 Radius=1.5 StartAngle=1.5708 EndAngle=4.71239
    g7: ArcOfCircle CenterX=-49.19 CenterY=27.25 CenterZ=0 NormalX=0 NormalY=0 NormalZ=1 AngleXU=0 Radius=1.5 StartAngle=1.5708 EndAngle=4.71239
    g8: ArcOfCircle CenterX=-49.19 CenterY=21.5 CenterZ=0 NormalX=0 NormalY=0 NormalZ=1 AngleXU=0 Radius=1.5 StartAngle=1.5708 EndAngle=4.71239
    g9: ArcOfCircle CenterX=-49.19 CenterY=15.75 CenterZ=0 NormalX=0 NormalY=0 NormalZ=1 AngleXU=0 Radius=1.5 StartAngle=1.5708 EndAngle=4.71239
    g10: ArcOfCircle CenterX=-49.19 CenterY=10 CenterZ=0 NormalX=0 NormalY=0 NormalZ=1 AngleXU=0 Radius=1.5 StartAngle=1.5708 EndAngle=4.71239
    g11: ArcOfCircle CenterX=-49.19 CenterY=4.25 CenterZ=0 NormalX=0 NormalY=0 NormalZ=1 AngleXU=0 Radius=1.5 StartAngle=1.5708 EndAngle=4.71239
    g12: LineSegment StartX=-49.19 StartY=69.25 StartZ=0 EndX=-49.19 EndY=66.25 EndZ=0
    g13: LineSegment StartX=-49.19 StartY=63.5 StartZ=0 EndX=-49.19 EndY=60.5 EndZ=0
    g14: LineSegment StartX=-49.19 StartY=57.75 StartZ=0 EndX=-49.19 EndY=54.75 EndZ=0
    g15: LineSegment StartX=-49.19 StartY=52 StartZ=0 EndX=-49.19 EndY=49 EndZ=0
    g16: LineSegment StartX=-49.19 StartY=46.25 StartZ=0 EndX=-49.19 EndY=43.25 EndZ=0
    g17: LineSegment StartX=-49.19 StartY=40.5 StartZ=0 EndX=-49.19 EndY=37.5 EndZ=0
    g18: LineSegment StartX=-49.19 StartY=34.5 StartZ=0 EndX=-49.19 EndY=31.5 EndZ=0
    g19: LineSegment StartX=-49.19 StartY=28.75 StartZ=0 EndX=-49.19 EndY=25.75 EndZ=0
    g20: LineSegment StartX=-49.19 StartY=23 StartZ=0 EndX=-49.19 EndY=20 EndZ=0
    g21: LineSegment StartX=-49.19 StartY=17.25 StartZ=0 EndX=-49.19 EndY=14.25 EndZ=0
    g22: LineSegment StartX=-49.19 StartY=11.5 StartZ=0 EndX=-49.19 EndY=8.5 EndZ=0
    g23: LineSegment StartX=-49.19 StartY=5.75 StartZ=0 EndX=-49.19 EndY=2.75 EndZ=0
  constraints (48):
    c: Block(g0)
    c: Block(g1)
    c: Block(g2)
    c: Block(g3)
    c: Block(g4)
    c: Block(g5)
    c: Block(g6)
    c: Block(g7)
    c: Block(g8)
    c: Block(g9)
    c: Block(g10)
    c: Block(g11)
    c: Coincident(g12,g0)
    c: Coincident(g12,g0)
    c: Vertical(g12)
    c: Vertical(g13)
    c: Coincident(g13,g1)
    c: Vertical(g14)
    c: Coincident(g14,g2)
    c: Vertical(g15)
    c: Coincident(g15,g3)
    c: Vertical(g16)
    c: Coincident(g16,g4)
    c: Vertical(g17)
    c: Coincident(g17,g5)
    c: Vertical(g18)
    c: Coincident(g18,g6)
    c: Vertical(g19)
    c: Coincident(g19,g7)
    c: Vertical(g20)
    c: Coincident(g20,g8)
    c: Vertical(g21)
    c: Coincident(g21,g9)
    c: Vertical(g22)
    c: Coincident(g22,g10)
    c: Vertical(g23)
    c: Coincident(g23,g11)
    c: Block(g23)
    c: Block(g22)
    c: Block(g21)
    c: Block(g20)
    c: Block(g13)
    c: Block(g14)
    c: Block(g15)
    c: Block(g16)
    c: Block(g17)
    c: Block(g18)
    c: Block(g19)
FEATURE [Part::Extrusion] Extrude022
  Base = -> Sketch030
  Dir = (1,-2e-16,2e-16)
  DirMode = 2
  FaceMakerClass = Part::FaceMakerBullseye
  LengthFwd = 19
  LengthRev = 0
  Placement = pos=(-19,0,0) rot=(0,0,1;0rad)
  Solid = true
  Symmetric = false
FEATURE [Part::Fillet] Fillet022
  Base = -> Extrude022
  Edges = 24 edges r=1.49: [Edge6,Edge11,Edge18,Edge23,Edge30,Edge35,Edge42,Edge47,Edge54,Edge59,Edge66,Edge71,Edge78,Edge83,Edge90,Edge95,Edge102,Edge107,Edge114,Edge119,Edge126,Edge131,Edge138,Edge143]
FEATURE [Part::Cut] Cut020  label="top010"
  Base = -> Cut019
  Tool = -> Fillet022
FEATURE [Sketcher::SketchObject] Sketch032
  FullyConstrained = true
  Placement = pos=(117,19,0) rot=(0.57735,0.57735,0.57735;2.0944rad)
  sketch-geometry (48):
    g0: LineSegment StartX=-49.19 StartY=69.25 StartZ=0 EndX=-49.19 EndY=66.25 EndZ=0
    g1: LineSegment StartX=-49.19 StartY=63.5 StartZ=0 EndX=-49.19 EndY=60.5 EndZ=0
    g2: LineSegment StartX=-49.19 StartY=57.75 StartZ=0 EndX=-49.19 EndY=54.75 EndZ=0
    g3: LineSegment StartX=-49.19 StartY=52 StartZ=0 EndX=-49.19 EndY=49 EndZ=0
    g4: LineSegment StartX=-49.19 StartY=46.25 StartZ=0 EndX=-49.19 EndY=43.25 EndZ=0
    g5: LineSegment StartX=-49.19 StartY=40.5 StartZ=0 EndX=-49.19 EndY=37.5 EndZ=0
    g6: LineSegment StartX=-49.19 StartY=34.5 StartZ=0 EndX=-49.19 EndY=31.5 EndZ=0
    g7: LineSegment StartX=-49.19 StartY=28.75 StartZ=0 EndX=-49.19 EndY=25.75 EndZ=0
    g8: LineSegment StartX=-49.19 StartY=23 StartZ=0 EndX=-49.19 EndY=20 EndZ=0
    g9: LineSegment StartX=-49.19 StartY=17.25 StartZ=0 EndX=-49.19 EndY=14.25 EndZ=0
    g10: LineSegment StartX=-49.19 StartY=11.5 StartZ=0 EndX=-49.19 EndY=8.5 EndZ=0
    g11: LineSegment StartX=-49.19 StartY=5.75 StartZ=0 EndX=-49.19 EndY=2.75 EndZ=0
    g12: ArcOfCircle CenterX=-1.5 CenterY=67.75 CenterZ=0 NormalX=0 NormalY=0 NormalZ=1 AngleXU=0 Radius=1.5 StartAngle=4.71239 EndAngle=7.85398
    g13: ArcOfCircle CenterX=-1.5 CenterY=62 CenterZ=0 NormalX=0 NormalY=0 NormalZ=1 AngleXU=0 Radius=1.5 StartAngle=4.71239 EndAngle=7.85398
    g14: ArcOfCircle CenterX=-1.5 CenterY=56.25 CenterZ=0 NormalX=0 NormalY=0 NormalZ=1 AngleXU=0 Radius=1.5 StartAngle=4.71239 EndAngle=7.85398
    g15: ArcOfCircle CenterX=-11.49 CenterY=50.5 CenterZ=0 NormalX=0 NormalY=0 NormalZ=1 AngleXU=0 Radius=1.5 StartAngle=4.71239 EndAngle=7.85398
    g16: ArcOfCircle CenterX=-16.28 CenterY=44.75 CenterZ=0 NormalX=0 NormalY=0 NormalZ=1 AngleXU=0 Radius=1.5 StartAngle=4.71239 EndAngle=7.85398
    g17: ArcOfCircle CenterX=-18.2337 CenterY=39 CenterZ=0 NormalX=0 NormalY=0 NormalZ=1 AngleXU=0 Radius=1.5 StartAngle=4.71485 EndAngle=7.85398
    g18: ArcOfCircle CenterX=-16.2837 CenterY=27.25 CenterZ=0 NormalX=0 NormalY=0 NormalZ=1 AngleXU=0 Radius=1.5 StartAngle=4.71485 EndAngle=7.85398
    g19: ArcOfCircle CenterX=-18.2337 CenterY=33 CenterZ=0 NormalX=0 NormalY=0 NormalZ=1 AngleXU=0 Radius=1.5 StartAngle=4.71485 EndAngle=7.85398
    g20: ArcOfCircle CenterX=-11.49 CenterY=21.5 CenterZ=0 NormalX=0 NormalY=0 NormalZ=1 AngleXU=0 Radius=1.5 StartAngle=4.71239 EndAngle=7.85398
    g21: ArcOfCircle CenterX=-1.5 CenterY=4.25 CenterZ=0 NormalX=0 NormalY=0 NormalZ=1 AngleXU=0 Radius=1.5 StartAngle=4.71239 EndAngle=7.85398
    g22: ArcOfCircle CenterX=-1.5 CenterY=10 CenterZ=0 NormalX=0 NormalY=0 NormalZ=1 AngleXU=0 Radius=1.5 StartAngle=4.71239 EndAngle=7.85398
    g23: ArcOfCircle CenterX=-1.5 CenterY=15.75 CenterZ=0 NormalX=0 NormalY=0 NormalZ=1 AngleXU=0 Radius=1.5 StartAngle=4.71239 EndAngle=7.85398
    g24: LineSegment StartX=-49.19 StartY=69.25 StartZ=0 EndX=-1.5 EndY=69.25 EndZ=0
    g25: LineSegment StartX=-49.19 StartY=66.25 StartZ=0 EndX=-1.5 EndY=66.25 EndZ=0
    g26: LineSegment StartX=-49.19 StartY=63.5 StartZ=0 EndX=-1.5 EndY=63.5 EndZ=0
    g27: LineSegment StartX=-49.19 StartY=60.5 StartZ=0 EndX=-1.5 EndY=60.5 EndZ=0
    g28: LineSegment StartX=-49.19 StartY=57.75 StartZ=0 EndX=-1.5 EndY=57.75 EndZ=0
    g29: LineSegment StartX=-49.19 StartY=54.75 StartZ=0 EndX=-1.5 EndY=54.75 EndZ=0
    g30: LineSegment StartX=-49.19 StartY=52 StartZ=0 EndX=-11.49 EndY=52 EndZ=0
    g31: LineSegment StartX=-49.19 StartY=49 StartZ=0 EndX=-11.49 EndY=49 EndZ=0
    g32: LineSegment StartX=-49.19 StartY=46.25 StartZ=0 EndX=-16.28 EndY=46.25 EndZ=0
    g33: LineSegment StartX=-49.19 StartY=43.25 StartZ=0 EndX=-16.28 EndY=43.25 EndZ=0
    g34: LineSegment StartX=-49.19 StartY=40.5 StartZ=0 EndX=-18.2337 EndY=40.5 EndZ=0
    g35: LineSegment StartX=-49.19 StartY=37.5 StartZ=0 EndX=-18.23 EndY=37.5 EndZ=0
    g36: LineSegment StartX=-49.19 StartY=34.5 StartZ=0 EndX=-18.2337 EndY=34.5 EndZ=0
    g37: LineSegment StartX=-49.19 StartY=31.5 StartZ=0 EndX=-18.23 EndY=31.5 EndZ=0
    g38: LineSegment StartX=-49.19 StartY=28.75 StartZ=0 EndX=-16.2837 EndY=28.75 EndZ=0
    g39: LineSegment StartX=-49.19 StartY=25.75 StartZ=0 EndX=-16.28 EndY=25.75 EndZ=0
    g40: LineSegment StartX=-49.19 StartY=23 StartZ=0 EndX=-11.49 EndY=23 EndZ=0
    g41: LineSegment StartX=-49.19 StartY=20 StartZ=0 EndX=-11.49 EndY=20 EndZ=0
    g42: LineSegment StartX=-49.19 StartY=17.25 StartZ=0 EndX=-1.5 EndY=17.25 EndZ=0
    g43: LineSegment StartX=-49.19 StartY=14.25 StartZ=0 EndX=-1.5 EndY=14.25 EndZ=0
    g44: LineSegment StartX=-49.19 StartY=11.5 StartZ=0 EndX=-1.5 EndY=11.5 EndZ=0
    g45: LineSegment StartX=-49.19 StartY=8.5 StartZ=0 EndX=-1.5 EndY=8.5 EndZ=0
    g46: LineSegment StartX=-49.19 StartY=5.75 StartZ=0 EndX=-1.5 EndY=5.75 EndZ=0
    g47: LineSegment StartX=-49.19 StartY=2.75 StartZ=0 EndX=-1.5 EndY=2.75 EndZ=0
  constraints (120):
    c: Vertical(g0)
    c: Distance(g0) = 3
    c: Block(g0)
    c: Vertical(g1)
    c: Distance(g1) = 3
    c: Vertical(g2)
    c: Equal(g0,g2) = 3
    c: Block(g2)
    c: Vertical(g3)
    c: Equal(g1,g3) = 3
    c: Vertical(g4)
    c: Equal(g0,g4) = 3
    c: Block(g4)
    c: Vertical(g5)
    c: Equal(g1,g5) = 3
    c: Vertical(g6)
    c: Equal(g0,g6) = 3
    c: Block(g6)
    c: Vertical(g7)
    c: Equal(g1,g7) = 3
    c: Vertical(g8)
    c: Equal(g0,g8) = 3
    c: Block(g8)
    c: Vertical(g9)
    c: Equal(g1,g9) = 3
    c: Vertical(g10)
    c: Equal(g0,g10) = 3
    c: Block(g10)
    c: Vertical(g11)
    c: Equal(g1,g11) = 3
    c: Block(g12)
    c: Block(g13)
    c: Block(g14)
    c: Block(g15)
    c: Block(g16)
    c: Block(g17)
    c: Block(g18)
    c: Block(g19)
    c: Block(g20)
    c: Block(g21)
    c: Block(g22)
    c: Block(g23)
    c: Block(g11)
    c: Block(g9)
    c: Block(g7)
    c: Block(g5)
    c: Block(g3)
    c: Block(g1)
    c: Coincident(g24,g0)
    c: Coincident(g24,g12)
    c: Horizontal(g24)
    c: Coincident(g25,g0)
    c: Coincident(g25,g12)
    c: Horizontal(g25)
    c: Coincident(g26,g1)
    c: Coincident(g26,g13)
    c: Horizontal(g26)
    c: Coincident(g27,g1)
    c: Coincident(g27,g13)
    c: Horizontal(g27)
    c: Coincident(g28,g2)
    c: Coincident(g28,g14)
    c: Horizontal(g28)
    c: Coincident(g29,g2)
    c: Coincident(g29,g14)
    c: Horizontal(g29)
    c: Coincident(g30,g3)
    c: Coincident(g30,g15)
    c: Horizontal(g30)
    c: Coincident(g31,g3)
    c: Coincident(g31,g15)
    c: Horizontal(g31)
    c: Coincident(g32,g4)
    c: Coincident(g32,g16)
    c: Horizontal(g32)
    c: Coincident(g33,g4)
    c: Coincident(g33,g16)
    c: Horizontal(g33)
    c: Coincident(g34,g5)
    c: Coincident(g34,g17)
    c: Horizontal(g34)
    c: Coincident(g35,g5)
    c: Coincident(g35,g17)
    c: Horizontal(g35)
    c: Coincident(g36,g6)
    c: Coincident(g36,g19)
    c: Horizontal(g36)
    c: Coincident(g37,g6)
    c: Coincident(g37,g19)
    c: Horizontal(g37)
    c: Coincident(g38,g7)
    c: Coincident(g38,g18)
    c: Horizontal(g38)
    c: Coincident(g39,g7)
    c: Coincident(g39,g18)
    c: Horizontal(g39)
    c: Coincident(g40,g8)
    c: Coincident(g40,g20)
    c: Horizontal(g40)
    c: Coincident(g41,g8)
    c: Coincident(g41,g20)
    c: Horizontal(g41)
    c: Coincident(g42,g9)
    c: Coincident(g42,g23)
    c: Horizontal(g42)
    c: Coincident(g43,g9)
    c: Coincident(g43,g23)
    c: Horizontal(g43)
    c: Coincident(g44,g10)
    c: Coincident(g44,g22)
    c: Horizontal(g44)
    c: Coincident(g45,g10)
    c: Coincident(g45,g22)
    c: Horizontal(g45)
    c: Coincident(g46,g11)
    c: Coincident(g46,g21)
    c: Horizontal(g46)
    c: Coincident(g47,g11)
    c: Coincident(g47,g21)
    c: Horizontal(g47)
FEATURE [Part::Extrusion] Extrude023
  Base = -> Sketch032
  Dir = (1,-2e-16,2e-16)
  DirMode = 2
  FaceMakerClass = Part::FaceMakerBullseye
  LengthFwd = 19
  LengthRev = 0
  Placement = pos=(-19,0,0) rot=(0,0,1;0rad)
  Solid = true
  Symmetric = false
FEATURE [Part::Fillet] Fillet023
  Base = -> Extrude023
  Edges = 24 edges r=1.49: [Edge6,Edge11,Edge18,Edge23,Edge30,Edge35,Edge42,Edge47,Edge54,Edge59,Edge66,Edge71,Edge78,Edge83,Edge90,Edge95,Edge102,Edge107,Edge114,Edge119,Edge126,Edge131,Edge138,Edge143]
  Placement = pos=(0,0.05,0) rot=(0,0,1;0rad)
FEATURE [Part::Cut] Cut014  label="bottom003"
  Base = -> Cut007
  Tool = -> Fusion047
FEATURE [Part::Cut] Cut021  label="bottom004"
  Base = -> Cut014
  Tool = -> Fillet023
FEATURE [Sketcher::SketchObject] Sketch033
  FullyConstrained = true
  Placement = pos=(117,19,0) rot=(0.57735,0.57735,0.57735;2.0944rad)
  sketch-geometry (8):
    g0: LineSegment StartX=-49.19 StartY=69.25 StartZ=0 EndX=-49.19 EndY=66.25 EndZ=0
    g1: LineSegment StartX=-49.19 StartY=5.75 StartZ=0 EndX=-49.19 EndY=2.75 EndZ=0
    g2: ArcOfCircle CenterX=-1.5 CenterY=67.75 CenterZ=0 NormalX=0 NormalY=0 NormalZ=1 AngleXU=0 Radius=1.5 StartAngle=4.71239 EndAngle=7.85398
    g3: ArcOfCircle CenterX=-1.5 CenterY=4.25 CenterZ=0 NormalX=0 NormalY=0 NormalZ=1 AngleXU=0 Radius=1.5 StartAngle=4.71239 EndAngle=7.85398
    g4: LineSegment StartX=-49.19 StartY=69.25 StartZ=0 EndX=-1.5 EndY=69.25 EndZ=0
    g5: LineSegment StartX=-49.19 StartY=66.25 StartZ=0 EndX=-1.5 EndY=66.25 EndZ=0
    g6: LineSegment StartX=-49.19 StartY=5.75 StartZ=0 EndX=-1.5 EndY=5.75 EndZ=0
    g7: LineSegment StartX=-49.19 StartY=2.75 StartZ=0 EndX=-1.5 EndY=2.75 EndZ=0
  constraints (19):
    c: Vertical(g0)
    c: Distance(g0) = 3
    c: Block(g0)
    c: Vertical(g1)
    c: Block(g2)
    c: Block(g3)
    c: Block(g1)
    c: Coincident(g4,g0)
    c: Coincident(g4,g2)
    c: Horizontal(g4)
    c: Coincident(g5,g0)
    c: Coincident(g5,g2)
    c: Horizontal(g5)
    c: Coincident(g6,g1)
    c: Coincident(g6,g3)
    c: Horizontal(g6)
    c: Coincident(g7,g1)
    c: Coincident(g7,g3)
    c: Horizontal(g7)
FEATURE [Sketcher::SketchObject] Sketch034
  FullyConstrained = true
  Placement = pos=(117,19,0) rot=(0.57735,0.57735,0.57735;2.0944rad)
  sketch-geometry (8):
    g0: LineSegment StartX=-49.19 StartY=63.5 StartZ=0 EndX=-49.19 EndY=60.5 EndZ=0
    g1: LineSegment StartX=-49.19 StartY=11.5 StartZ=0 EndX=-49.19 EndY=8.5 EndZ=0
    g2: ArcOfCircle CenterX=-1.5 CenterY=62 CenterZ=0 NormalX=0 NormalY=0 NormalZ=1 AngleXU=0 Radius=1.5 StartAngle=4.71239 EndAngle=7.85398
    g3: ArcOfCircle CenterX=-1.5 CenterY=10 CenterZ=0 NormalX=0 NormalY=0 NormalZ=1 AngleXU=0 Radius=1.5 StartAngle=4.71239 EndAngle=7.85398
    g4: LineSegment StartX=-49.19 StartY=63.5 StartZ=0 EndX=-1.5 EndY=63.5 EndZ=0
    g5: LineSegment StartX=-49.19 StartY=60.5 StartZ=0 EndX=-1.5 EndY=60.5 EndZ=0
    g6: LineSegment StartX=-49.19 StartY=11.5 StartZ=0 EndX=-1.5 EndY=11.5 EndZ=0
    g7: LineSegment StartX=-49.19 StartY=8.5 StartZ=0 EndX=-1.5 EndY=8.5 EndZ=0
  constraints (19):
    c: Vertical(g0)
    c: Distance(g0) = 3
    c: Vertical(g1)
    c: Block(g1)
    c: Block(g2)
    c: Block(g3)
    c: Block(g0)
    c: Coincident(g4,g0)
    c: Coincident(g4,g2)
    c: Horizontal(g4)
    c: Coincident(g5,g0)
    c: Coincident(g5,g2)
    c: Horizontal(g5)
    c: Coincident(g6,g1)
    c: Coincident(g6,g3)
    c: Horizontal(g6)
    c: Coincident(g7,g1)
    c: Coincident(g7,g3)
    c: Horizontal(g7)
FEATURE [Part::Extrusion] Extrude024
  Base = -> Sketch033
  Dir = (1,0,0)
  DirMode = 2
  FaceMakerClass = Part::FaceMakerBullseye
  LengthFwd = 10
  LengthRev = 0
  Solid = true
  Symmetric = false
FEATURE [Part::Extrusion] Extrude025
  Base = -> Sketch034
  Dir = (1,0,0)
  DirMode = 2
  FaceMakerClass = Part::FaceMakerBullseye
  LengthFwd = 10
  LengthRev = 0
  Solid = true
  Symmetric = false
FEATURE [Part::Fillet] Fillet024  label="removeFromtMoreFrontCaseScrewRetainers"
  Base = -> Extrude024
  Edges = 4 edges r=1.49: [Edge6,Edge11,Edge18,Edge23]
  Placement = pos=(-11,0,0) rot=(0,0,1;0rad)
FEATURE [Part::Fillet] Fillet025  label="removeFromtMoreFrontCaseScrewRetainers001"
  Base = -> Extrude025
  Edges = 4 edges r=1.49: [Edge6,Edge11,Edge18,Edge23]
  Placement = pos=(-19,0,0) rot=(0,0,1;0rad)
FEATURE [Part::Cut] Cut022
  Base = -> Cut015
  Tool = -> Fillet025
FEATURE [Part::Cut] Cut023  label="screwRetainers"
  Base = -> Cut022
  Tool = -> Fillet024
FEATURE [Part::MultiFuse] Fusion056  label="bottom005"
  Shapes = -> [Fusion044,Cut021]
FEATURE [Part::MultiFuse] Fusion057  label="casePillars001"
  Shapes = -> [Cut016,Fusion052]
FEATURE [Part::MultiFuse] Fusion058  label="bottom006"
  Shapes = -> [Fusion056,Cut023]
FEATURE [Part::MultiFuse] Fusion059  label="bottom007"
  Shapes = -> [Fusion058,Fillet005]
FEATURE [Part::MultiFuse] Fusion060  label="bottom008"
  Shapes = -> [Fusion059,Fusion]
FEATURE [Part::MultiFuse] Fusion061  label="top011"
  Shapes = -> [Cut006,Cut020]
FEATURE [Part::MultiFuse] Fusion062  label="top012"
  Shapes = -> [Fusion057,Fusion061]
FEATURE [Sketcher::SketchObject] Sketch035  label="topSketch007"
  FullyConstrained = true
  sketch-geometry (6):
    g0: LineSegment StartX=19 StartY=38 StartZ=0 EndX=117 EndY=38 EndZ=0
    g1: ArcOfCircle CenterX=19 CenterY=19 CenterZ=0 NormalX=0 NormalY=0 NormalZ=1 AngleXU=0 Radius=19 StartAngle=1.5708 EndAngle=3.14159
    g2: LineSegment StartX=117 StartY=38 StartZ=0 EndX=117 EndY=19 EndZ=0
    g3: LineSegment StartX=98 StartY=1.0161e-12 StartZ=0 EndX=5.22862e-06 EndY=1.0161e-12 EndZ=0
    g4: LineSegment StartX=5.22862e-06 StartY=19 StartZ=0 EndX=5.22862e-06 EndY=1.0161e-12 EndZ=0
    g5: ArcOfCircle CenterX=98 CenterY=19 CenterZ=0 NormalX=0 NormalY=0 NormalZ=1 AngleXU=0 Radius=19 StartAngle=4.71239 EndAngle=6.28319
  constraints (16):
    c: Horizontal(g0)
    c: Distance(g0) = 98
    c: Coincident(g1,g0)
    c: Block(g1)
    c: Coincident(g2,g0)
    c: Vertical(g2)
    c: Distance(g2) = 19
    c: Horizontal(g3)
    c: Coincident(g4,g1)
    c: Vertical(g4)
    c: Coincident(g3,g4)
    c: Block(g3)
    c: Coincident(g5,g2)
    c: Coincident(g5,g3)
    c: Block(g0)
    c: Block(g5)
FEATURE [Part::Extrusion] Extrude026  label="sideA001"
  Base = -> Sketch035
  Dir = (0,0,1)
  DirMode = 2
  FaceMakerClass = Part::FaceMakerBullseye
  LengthFwd = 3
  LengthRev = 0
  Placement = pos=(0,0,-2.7) rot=(0,0,1;0rad)
  Solid = true
  Symmetric = false
FEATURE [Sketcher::SketchObject] Sketch036  label="topSketch008"
  FullyConstrained = true
  sketch-geometry (6):
    g0: LineSegment StartX=19 StartY=38 StartZ=0 EndX=117 EndY=38 EndZ=0
    g1: ArcOfCircle CenterX=19 CenterY=19 CenterZ=0 NormalX=0 NormalY=0 NormalZ=1 AngleXU=0 Radius=19 StartAngle=1.5708 EndAngle=3.14159
    g2: LineSegment StartX=117 StartY=38 StartZ=0 EndX=117 EndY=19 EndZ=0
    g3: LineSegment StartX=98 StartY=1.0161e-12 StartZ=0 EndX=5.22862e-06 EndY=1.0161e-12 EndZ=0
    g4: LineSegment StartX=5.22862e-06 StartY=19 StartZ=0 EndX=5.22862e-06 EndY=1.0161e-12 EndZ=0
    g5: ArcOfCircle CenterX=98 CenterY=19 CenterZ=0 NormalX=0 NormalY=0 NormalZ=1 AngleXU=0 Radius=19 StartAngle=4.71239 EndAngle=6.28319
  constraints (16):
    c: Horizontal(g0)
    c: Distance(g0) = 98
    c: Coincident(g1,g0)
    c: Block(g1)
    c: Coincident(g2,g0)
    c: Vertical(g2)
    c: Distance(g2) = 19
    c: Horizontal(g3)
    c: Coincident(g4,g1)
    c: Vertical(g4)
    c: Coincident(g3,g4)
    c: Block(g3)
    c: Coincident(g5,g2)
    c: Coincident(g5,g3)
    c: Block(g0)
    c: Block(g5)
FEATURE [Part::Extrusion] Extrude027  label="sideB001"
  Base = -> Sketch036
  Dir = (0,0,1)
  DirMode = 2
  FaceMakerClass = Part::FaceMakerBullseye
  LengthFwd = 3
  LengthRev = 0
  Placement = pos=(0,0,71.7) rot=(0,0,1;0rad)
  Solid = true
  Symmetric = false
FEATURE [Part::MultiFuse] Fusion064  label="removeFromBottom"
  Shapes = -> [Extrude026,Extrude027]
FEATURE [Part::Cut] Cut024  label="bottom009"
  Base = -> Fusion060
  Tool = -> Fusion064
FEATURE [Sketcher::SketchObject] Sketch037  label="topSketch009"
  FullyConstrained = true
  sketch-geometry (6):
    g0: ArcOfCircle CenterX=19 CenterY=19 CenterZ=0 NormalX=0 NormalY=0 NormalZ=1 AngleXU=0 Radius=19 StartAngle=1.5708 EndAngle=3.14159
    g1: LineSegment StartX=5.22862e-06 StartY=19 StartZ=0 EndX=5.22862e-06 EndY=1.19904e-11 EndZ=0
    g2: LineSegment StartX=19 StartY=38 StartZ=0 EndX=124 EndY=38 EndZ=0
    g3: LineSegment StartX=5.22862e-06 StartY=1.19904e-11 StartZ=0 EndX=105 EndY=1.19904e-11 EndZ=0
    g4: ArcOfCircle CenterX=105 CenterY=19 CenterZ=0 NormalX=0 NormalY=0 NormalZ=1 AngleXU=0 Radius=19 StartAngle=4.71239 EndAngle=6.28319
    g5: LineSegment StartX=124 StartY=38 StartZ=0 EndX=124 EndY=19 EndZ=0
  constraints (16):
    c: Block(g0)
    c: Coincident(g1,g0)
    c: Vertical(g1)
    c: Horizontal(g2)
    c: Distance(g2) = 105
    c: Coincident(g2,g0)
    c: Distance(g1) = 19
    c: Coincident(g3,g1)
    c: Horizontal(g3)
    c: Distance(g3) = 105
    c: Block(g4)
    c: Coincident(g4,g3)
    c: Coincident(g5,g2)
    c: Coincident(g5,g4)
    c: Vertical(g5)
    c: Distance(g5) = 19
FEATURE [Part::Extrusion] Extrude028  label="sideB"
  Base = -> Sketch037
  Dir = (0,0,1)
  DirMode = 2
  FaceMakerClass = Part::FaceMakerBullseye
  LengthFwd = 3
  LengthRev = 0
  Placement = pos=(0,0,72) rot=(0,0,1;0rad)
  Solid = true
  Symmetric = false
FEATURE [Sketcher::SketchObject] Sketch038  label="topSketch010"
  FullyConstrained = true
  sketch-geometry (20):
    g0: LineSegment StartX=5.21097e-06 StartY=3 StartZ=0 EndX=5.21097e-06 EndY=19 EndZ=0
    g1: ArcOfCircle CenterX=19 CenterY=19 CenterZ=0 NormalX=0 NormalY=0 NormalZ=1 AngleXU=0 Radius=19 StartAngle=1.5708 EndAngle=3.14159
    g2: ArcOfCircle CenterX=19 CenterY=19 CenterZ=0 NormalX=0 NormalY=0 NormalZ=1 AngleXU=0 Radius=16 StartAngle=1.5708 EndAngle=3.14159
    g3: LineSegment StartX=114 StartY=35 StartZ=0 EndX=19 EndY=35 EndZ=0
    g4: LineSegment StartX=5.21097e-06 StartY=3 StartZ=0 EndX=5.21097e-06 EndY=0 EndZ=0
    g5: LineSegment StartX=3 StartY=0 StartZ=0 EndX=5.21097e-06 EndY=0 EndZ=0
    g6: LineSegment StartX=3 StartY=19 StartZ=0 EndX=3 EndY=0 EndZ=0
    g7: LineSegment StartX=19 StartY=38 StartZ=0 EndX=124 EndY=38 EndZ=0
    g8: Circle CenterX=119 CenterY=35 CenterZ=0 NormalX=0 NormalY=0 NormalZ=1 AngleXU=0 Radius=1
    g9: Circle CenterX=121 CenterY=35 CenterZ=0 NormalX=0 NormalY=0 NormalZ=1 AngleXU=0 Radius=1
    g10: Circle CenterX=121 CenterY=33 CenterZ=0 NormalX=0 NormalY=0 NormalZ=1 AngleXU=0 Radius=1
    g11: BSplineCurve PolesCount=3 KnotsCount=2 Degree=2 IsPeriodic=0
    g12: GeomPoint X=119 Y=35 Z=0
    g13: GeomPoint X=121 Y=33 Z=0
    g14: LineSegment StartX=119 StartY=35 StartZ=0 EndX=114 EndY=35 EndZ=0
    g15: ArcOfCircle CenterX=105 CenterY=19 CenterZ=0 NormalX=0 NormalY=0 NormalZ=1 AngleXU=0 Radius=19 StartAngle=5.7297 EndAngle=6.28319
    g16: ArcOfCircle CenterX=105 CenterY=19 CenterZ=0 NormalX=0 NormalY=0 NormalZ=1 AngleXU=0 Radius=16 StartAngle=5.60905 EndAngle=6.28319
    g17: LineSegment StartX=121 StartY=33 StartZ=0 EndX=121 EndY=19 EndZ=0
    g18: LineSegment StartX=124 StartY=38 StartZ=0 EndX=124 EndY=19 EndZ=0
    g19: LineSegment StartX=117.5 StartY=9.01251 StartZ=0 EndX=121.163 EndY=9.0125 EndZ=0
  constraints (46):
    c: Vertical(g0)
    c: Block(g0)
    c: Coincident(g1,g0)
    c: Block(g1)
    c: Coincident(g2,g1)
    c: Block(g2)
    c: Coincident(g3,g2)
    c: Horizontal(g3)
    c: Tangent(g3,g2)
    c: Coincident(g4,g0)
    c: Distance(g4) = 3
    c: Vertical(g4)
    c: Coincident(g5,g4)
    c: Horizontal(g5)
    c: Coincident(g6,g2)
    c: Coincident(g6,g5)
    c: Vertical(g6)
    c: Horizontal(g7)
    c: Distance(g7) = 105
    c: Coincident(g7,g1)
    c: Block(g3)
    c: Weight(g8) = 1
    c: Equal(g8,g9)
    c: Equal(g8,g10)
    c: InternalAlignment(g8,g11)
    c: InternalAlignment(g9,g11)
    c: InternalAlignment(g10,g11)
    c: InternalAlignment(g12,g11)
    c: InternalAlignment(g13,g11)
    c: Block(g11)
    c: Coincident(g14,g11)
    c: Coincident(g14,g3)
    c: Horizontal(g14)
    c: Block(g15)
    c: Coincident(g16,g15)
    c: Block(g16)
    c: Coincident(g17,g11)
    c: Coincident(g17,g16)
    c: Vertical(g17)
    c: Distance(g17) = 14
    c: Coincident(g18,g7)
    c: Coincident(g18,g15)
    c: Vertical(g18)
    c: Distance(g18) = 19
    c: Coincident(g19,g16)
    c: Coincident(g19,g15)
FEATURE [Part::Extrusion] Extrude029
  Base = -> Sketch038
  Dir = (0,0,1)
  DirMode = 2
  FaceMakerClass = Part::FaceMakerBullseye
  LengthFwd = 72
  LengthRev = 0
  Solid = true
  Symmetric = false
FEATURE [Part::Feature] Face085
  shape: bbox 4.8 x 25.5 x 2e-07 mm, 1 faces, 0 solids (baked)
FEATURE [Part::Revolution] Revolve089  label="moreFrontCaseScrewPost003"
  Angle = 360
  Axis = (0,1,0)
  Base = (0,0,0)
  FaceMakerClass = Part::FaceMakerBullseye
  Placement = pos=(109.5,4.5,3.5) rot=(0,0,1;0rad)
  Solid = false
  Source = -> Face085
  Symmetric = false
FEATURE [Part::Feature] Face086
  shape: bbox 4.8 x 25.5 x 2e-07 mm, 1 faces, 0 solids (baked)
FEATURE [Part::Revolution] Revolve090  label="moreFrontCaseScrewPost004"
  Angle = 360
  Axis = (0,1,0)
  Base = (0,0,0)
  FaceMakerClass = Part::FaceMakerBullseye
  Placement = pos=(109.5,4.5,68.5) rot=(0,0,1;0rad)
  Solid = false
  Source = -> Face086
  Symmetric = false
FEATURE [Part::Fillet] Fillet026  label="top013"
  Base = -> Extrude029
  Edges = 1 edges r=2: [Edge35]
FEATURE [Sketcher::SketchObject] Sketch039
  FullyConstrained = true
  sketch-geometry (7):
    g0: LineSegment StartX=0 StartY=0 StartZ=0 EndX=0 EndY=6 EndZ=0
    g1: Circle CenterX=0 CenterY=0 CenterZ=0 NormalX=0 NormalY=0 NormalZ=1 AngleXU=0 Radius=1
    g2: Circle CenterX=8 CenterY=6 CenterZ=0 NormalX=0 NormalY=0 NormalZ=1 AngleXU=0 Radius=1
    g3: BSplineCurve PolesCount=3 KnotsCount=2 Degree=2 IsPeriodic=0
    g4: GeomPoint X=0 Y=0 Z=0
    g5: GeomPoint X=8 Y=6 Z=0
    g6: LineSegment StartX=0 StartY=6 StartZ=0 EndX=8 EndY=6 EndZ=0
  constraints (14):
    c: Coincident(g0,g-1)
    c: Distance(g0) = 6
    c: Vertical(g0)
    c: Coincident(g3,g0)
    c: Weight(g1) = 1
    c: Equal(g1,g2)
    c: InternalAlignment(g1,g3)
    c: InternalAlignment(g2,g3)
    c: InternalAlignment(g4,g3)
    c: InternalAlignment(g5,g3)
    c: Block(g3)
    c: Coincident(g6,g0)
    c: Coincident(g6,g3)
    c: Horizontal(g6)
FEATURE [Sketcher::SketchObject] Sketch040
  FullyConstrained = true
  sketch-geometry (7):
    g0: LineSegment StartX=0 StartY=0 StartZ=0 EndX=0 EndY=6 EndZ=0
    g1: Circle CenterX=0 CenterY=0 CenterZ=0 NormalX=0 NormalY=0 NormalZ=1 AngleXU=0 Radius=1
    g2: Circle CenterX=8 CenterY=6 CenterZ=0 NormalX=0 NormalY=0 NormalZ=1 AngleXU=0 Radius=1
    g3: BSplineCurve PolesCount=3 KnotsCount=2 Degree=2 IsPeriodic=0
    g4: GeomPoint X=0 Y=0 Z=0
    g5: GeomPoint X=8 Y=6 Z=0
    g6: LineSegment StartX=0 StartY=6 StartZ=0 EndX=8 EndY=6 EndZ=0
  constraints (14):
    c: Coincident(g0,g-1)
    c: Distance(g0) = 6
    c: Vertical(g0)
    c: Coincident(g3,g0)
    c: Weight(g1) = 1
    c: Equal(g1,g2)
    c: InternalAlignment(g1,g3)
    c: InternalAlignment(g2,g3)
    c: InternalAlignment(g4,g3)
    c: InternalAlignment(g5,g3)
    c: Block(g3)
    c: Coincident(g6,g0)
    c: Coincident(g6,g3)
    c: Horizontal(g6)
FEATURE [Sketcher::SketchObject] Sketch041
  FullyConstrained = true
  sketch-geometry (7):
    g0: LineSegment StartX=0 StartY=0 StartZ=0 EndX=0 EndY=6 EndZ=0
    g1: Circle CenterX=0 CenterY=0 CenterZ=0 NormalX=0 NormalY=0 NormalZ=1 AngleXU=0 Radius=1
    g2: Circle CenterX=8 CenterY=6 CenterZ=0 NormalX=0 NormalY=0 NormalZ=1 AngleXU=0 Radius=1
    g3: BSplineCurve PolesCount=3 KnotsCount=2 Degree=2 IsPeriodic=0
    g4: GeomPoint X=0 Y=0 Z=0
    g5: GeomPoint X=8 Y=6 Z=0
    g6: LineSegment StartX=0 StartY=6 StartZ=0 EndX=8 EndY=6 EndZ=0
  constraints (14):
    c: Coincident(g0,g-1)
    c: Distance(g0) = 6
    c: Vertical(g0)
    c: Coincident(g3,g0)
    c: Weight(g1) = 1
    c: Equal(g1,g2)
    c: InternalAlignment(g1,g3)
    c: InternalAlignment(g2,g3)
    c: InternalAlignment(g4,g3)
    c: InternalAlignment(g5,g3)
    c: Block(g3)
    c: Coincident(g6,g0)
    c: Coincident(g6,g3)
    c: Horizontal(g6)
FEATURE [Sketcher::SketchObject] Sketch042
  FullyConstrained = true
  sketch-geometry (7):
    g0: LineSegment StartX=0 StartY=0 StartZ=0 EndX=0 EndY=6 EndZ=0
    g1: Circle CenterX=0 CenterY=0 CenterZ=0 NormalX=0 NormalY=0 NormalZ=1 AngleXU=0 Radius=1
    g2: Circle CenterX=8 CenterY=6 CenterZ=0 NormalX=0 NormalY=0 NormalZ=1 AngleXU=0 Radius=1
    g3: BSplineCurve PolesCount=3 KnotsCount=2 Degree=2 IsPeriodic=0
    g4: GeomPoint X=0 Y=0 Z=0
    g5: GeomPoint X=8 Y=6 Z=0
    g6: LineSegment StartX=0 StartY=6 StartZ=0 EndX=8 EndY=6 EndZ=0
  constraints (14):
    c: Coincident(g0,g-1)
    c: Distance(g0) = 6
    c: Vertical(g0)
    c: Coincident(g3,g0)
    c: Weight(g1) = 1
    c: Equal(g1,g2)
    c: InternalAlignment(g1,g3)
    c: InternalAlignment(g2,g3)
    c: InternalAlignment(g4,g3)
    c: InternalAlignment(g5,g3)
    c: Block(g3)
    c: Coincident(g6,g0)
    c: Coincident(g6,g3)
    c: Horizontal(g6)
FEATURE [Part::Extrusion] Extrude030  label="caseScrewPillarBracket008"
  Base = -> Sketch039
  Dir = (0,0,1)
  DirMode = 2
  FaceMakerClass = Part::FaceMakerBullseye
  LengthFwd = 2.4
  LengthRev = 0
  Placement = pos=(15.76,29,8.8) rot=(0,1,0;0rad)
  Solid = true
  Symmetric = false
FEATURE [Part::Extrusion] Extrude031  label="caseScrewPillarBracket009"
  Base = -> Sketch040
  Dir = (0,0,1)
  DirMode = 2
  FaceMakerClass = Part::FaceMakerBullseye
  LengthFwd = 2.4
  LengthRev = 0
  Placement = pos=(15.76,29,60.8) rot=(0,0,1;0rad)
  Solid = true
  Symmetric = false
FEATURE [Part::Extrusion] Extrude032  label="caseScrewPillarBracket010"
  Base = -> Sketch041
  Dir = (0,0,1)
  DirMode = 2
  FaceMakerClass = Part::FaceMakerBullseye
  LengthFwd = 2.4
  LengthRev = 0
  Placement = pos=(13.7,29,13.26) rot=(0,-1,0;1.5708rad)
  Solid = true
  Symmetric = false
FEATURE [Part::Extrusion] Extrude033  label="caseScrewPillarBracket011"
  Base = -> Sketch042
  Dir = (0,0,1)
  DirMode = 2
  FaceMakerClass = Part::FaceMakerBullseye
  LengthFwd = 2.4
  LengthRev = 0
  Placement = pos=(11.3,29,58.74) rot=(0,1,0;1.5708rad)
  Solid = true
  Symmetric = false
FEATURE [Sketcher::SketchObject] Sketch043
  FullyConstrained = true
  sketch-geometry (7):
    g0: LineSegment StartX=0 StartY=0 StartZ=0 EndX=0 EndY=6 EndZ=0
    g1: Circle CenterX=0 CenterY=0 CenterZ=0 NormalX=0 NormalY=0 NormalZ=1 AngleXU=0 Radius=1
    g2: Circle CenterX=8 CenterY=6 CenterZ=0 NormalX=0 NormalY=0 NormalZ=1 AngleXU=0 Radius=1
    g3: BSplineCurve PolesCount=3 KnotsCount=2 Degree=2 IsPeriodic=0
    g4: GeomPoint X=0 Y=0 Z=0
    g5: GeomPoint X=8 Y=6 Z=0
    g6: LineSegment StartX=0 StartY=6 StartZ=0 EndX=8 EndY=6 EndZ=0
  constraints (14):
    c: Coincident(g0,g-1)
    c: Distance(g0) = 6
    c: Vertical(g0)
    c: Coincident(g3,g0)
    c: Weight(g1) = 1
    c: Equal(g1,g2)
    c: InternalAlignment(g1,g3)
    c: InternalAlignment(g2,g3)
    c: InternalAlignment(g4,g3)
    c: InternalAlignment(g5,g3)
    c: Block(g3)
    c: Coincident(g6,g0)
    c: Coincident(g6,g3)
    c: Horizontal(g6)
FEATURE [Part::Extrusion] Extrude034  label="caseScrewPillarBracket012"
  Base = -> Sketch043
  Dir = (0,0,1)
  DirMode = 2
  FaceMakerClass = Part::FaceMakerBullseye
  LengthFwd = 2.4
  LengthRev = 0
  Placement = pos=(88.3,29,65.23) rot=(0,1,0;1.5708rad)
  Solid = true
  Symmetric = false
FEATURE [Sketcher::SketchObject] Sketch044
  FullyConstrained = true
  sketch-geometry (7):
    g0: LineSegment StartX=0 StartY=0 StartZ=0 EndX=0 EndY=6 EndZ=0
    g1: Circle CenterX=0 CenterY=0 CenterZ=0 NormalX=0 NormalY=0 NormalZ=1 AngleXU=0 Radius=1
    g2: Circle CenterX=8 CenterY=6 CenterZ=0 NormalX=0 NormalY=0 NormalZ=1 AngleXU=0 Radius=1
    g3: BSplineCurve PolesCount=3 KnotsCount=2 Degree=2 IsPeriodic=0
    g4: GeomPoint X=0 Y=0 Z=0
    g5: GeomPoint X=8 Y=6 Z=0
    g6: LineSegment StartX=0 StartY=6 StartZ=0 EndX=8 EndY=6 EndZ=0
  constraints (14):
    c: Coincident(g0,g-1)
    c: Distance(g0) = 6
    c: Vertical(g0)
    c: Coincident(g3,g0)
    c: Weight(g1) = 1
    c: Equal(g1,g2)
    c: InternalAlignment(g1,g3)
    c: InternalAlignment(g2,g3)
    c: InternalAlignment(g4,g3)
    c: InternalAlignment(g5,g3)
    c: Block(g3)
    c: Coincident(g6,g0)
    c: Coincident(g6,g3)
    c: Horizontal(g6)
FEATURE [Part::Extrusion] Extrude035  label="caseScrewPillarBracket013"
  Base = -> Sketch044
  Dir = (0,0,1)
  DirMode = 2
  FaceMakerClass = Part::FaceMakerBullseye
  LengthFwd = 2.4
  LengthRev = 0
  Placement = pos=(90.7,29,6.77) rot=(0,-1,0;1.5708rad)
  Solid = true
  Symmetric = false
FEATURE [Sketcher::SketchObject] Sketch045
  FullyConstrained = true
  sketch-geometry (7):
    g0: LineSegment StartX=0 StartY=0 StartZ=0 EndX=0 EndY=6 EndZ=0
    g1: Circle CenterX=0 CenterY=0 CenterZ=0 NormalX=0 NormalY=0 NormalZ=1 AngleXU=0 Radius=1
    g2: Circle CenterX=8 CenterY=6 CenterZ=0 NormalX=0 NormalY=0 NormalZ=1 AngleXU=0 Radius=1
    g3: BSplineCurve PolesCount=3 KnotsCount=2 Degree=2 IsPeriodic=0
    g4: GeomPoint X=0 Y=0 Z=0
    g5: GeomPoint X=8 Y=6 Z=0
    g6: LineSegment StartX=0 StartY=6 StartZ=0 EndX=8 EndY=6 EndZ=0
  constraints (14):
    c: Coincident(g0,g-1)
    c: Distance(g0) = 6
    c: Vertical(g0)
    c: Coincident(g3,g0)
    c: Weight(g1) = 1
    c: Equal(g1,g2)
    c: InternalAlignment(g1,g3)
    c: InternalAlignment(g2,g3)
    c: InternalAlignment(g4,g3)
    c: InternalAlignment(g5,g3)
    c: Block(g3)
    c: Coincident(g6,g0)
    c: Coincident(g6,g3)
    c: Horizontal(g6)
FEATURE [Sketcher::SketchObject] Sketch046
  FullyConstrained = true
  sketch-geometry (7):
    g0: LineSegment StartX=0 StartY=0 StartZ=0 EndX=0 EndY=6 EndZ=0
    g1: Circle CenterX=0 CenterY=0 CenterZ=0 NormalX=0 NormalY=0 NormalZ=1 AngleXU=0 Radius=1
    g2: Circle CenterX=8 CenterY=6 CenterZ=0 NormalX=0 NormalY=0 NormalZ=1 AngleXU=0 Radius=1
    g3: BSplineCurve PolesCount=3 KnotsCount=2 Degree=2 IsPeriodic=0
    g4: GeomPoint X=0 Y=0 Z=0
    g5: GeomPoint X=8 Y=6 Z=0
    g6: LineSegment StartX=0 StartY=6 StartZ=0 EndX=8 EndY=6 EndZ=0
  constraints (14):
    c: Coincident(g0,g-1)
    c: Distance(g0) = 6
    c: Vertical(g0)
    c: Coincident(g3,g0)
    c: Weight(g1) = 1
    c: Equal(g1,g2)
    c: InternalAlignment(g1,g3)
    c: InternalAlignment(g2,g3)
    c: InternalAlignment(g4,g3)
    c: InternalAlignment(g5,g3)
    c: Block(g3)
    c: Coincident(g6,g0)
    c: Coincident(g6,g3)
    c: Horizontal(g6)
FEATURE [Part::Extrusion] Extrude036  label="caseScrewPillarBracket014"
  Base = -> Sketch045
  Dir = (0,0,1)
  DirMode = 2
  FaceMakerClass = Part::FaceMakerBullseye
  LengthFwd = 2.4
  LengthRev = 0
  Placement = pos=(110.7,29,6.77) rot=(0,-1,0;1.5708rad)
  Solid = true
  Symmetric = false
FEATURE [Part::Extrusion] Extrude037  label="caseScrewPillarBracket015"
  Base = -> Sketch046
  Dir = (0,0,1)
  DirMode = 2
  FaceMakerClass = Part::FaceMakerBullseye
  LengthFwd = 2.4
  LengthRev = 0
  Placement = pos=(108.3,29,65.23) rot=(0,1,0;1.5708rad)
  Solid = true
  Symmetric = false
FEATURE [Part::Box] Box013  label="frontCaseScrewPillarBracket002"
  AttacherType = Attacher::AttachEngine3D
  Height = 2.4
  Length = 22
  Placement = pos=(87,28,2.3) rot=(0,0,1;0rad)
  Width = 7
FEATURE [Part::Box] Box014  label="frontCaseScrewPillarBracket003"
  AttacherType = Attacher::AttachEngine3D
  Height = 2.4
  Length = 22
  Placement = pos=(87,28,67.3) rot=(0,0,1;0rad)
  Width = 7
FEATURE [Part::Feature] Face087
  shape: bbox 4.8 x 30.2 x 2e-07 mm, 1 faces, 0 solids (baked)
FEATURE [Part::Revolution] Revolve091  label="frontCaseScrewPost004"
  Angle = 360
  Axis = (0,1,0)
  Base = (0,0,0)
  FaceMakerClass = Part::FaceMakerBullseye
  Placement = pos=(89.5,4.5,3.5) rot=(0,0,1;0rad)
  Solid = false
  Source = -> Face087
  Symmetric = false
FEATURE [Part::Feature] Face088
  shape: bbox 4.8 x 30.2 x 2e-07 mm, 1 faces, 0 solids (baked)
FEATURE [Part::Revolution] Revolve092  label="frontCaseScrewPost005"
  Angle = 360
  Axis = (0,1,0)
  Base = (0,0,0)
  FaceMakerClass = Part::FaceMakerBullseye
  Placement = pos=(89.5,4.5,68.5) rot=(0,0,1;0rad)
  Solid = false
  Source = -> Face088
  Symmetric = false
FEATURE [Part::Feature] Face089
  shape: bbox 3.5 x 30.2 x 2e-07 mm, 1 faces, 0 solids (baked)
FEATURE [Part::Revolution] Revolve093  label="backCaseScrewPost002"
  Angle = 360
  Axis = (0,1,0)
  Base = (0,0,0)
  FaceMakerClass = Part::FaceMakerBullseye
  Placement = pos=(12.5,4.5,10) rot=(0,0,1;0rad)
  Solid = false
  Source = -> Face089
  Symmetric = false
FEATURE [Part::Feature] Face090
  shape: bbox 3.5 x 30.2 x 2e-07 mm, 1 faces, 0 solids (baked)
FEATURE [Part::Revolution] Revolve094  label="backCaseScrewPost003"
  Angle = 360
  Axis = (0,1,0)
  Base = (0,0,0)
  FaceMakerClass = Part::FaceMakerBullseye
  Placement = pos=(12.5,4.5,62) rot=(0,0,1;0rad)
  Solid = false
  Source = -> Face090
  Symmetric = false
FEATURE [Part::Box] Box015  label="Cube011"
  AttacherType = Attacher::AttachEngine3D
  Height = 28.8
  Length = 3
  Placement = pos=(107.3,28,21.6) rot=(0,0,1;0rad)
  Width = 7
FEATURE [Part::Box] Box016  label="Cube012"
  AttacherType = Attacher::AttachEngine3D
  Height = 3
  Length = 7.4
  Placement = pos=(107.3,28,18.6) rot=(0,0,1;0rad)
  Width = 7
FEATURE [Part::Box] Box017  label="Cube013"
  AttacherType = Attacher::AttachEngine3D
  Height = 3
  Length = 7.4
  Placement = pos=(107.3,28,50.4) rot=(0,0,1;0rad)
  Width = 7
FEATURE [Part::Cylinder] Cylinder024
  Angle = 360
  AttacherType = Attacher::AttachEngine3D
  Height = 20
  Placement = pos=(0,0,36.15) rot=(0,0,1;0rad)
  Radius = 14.3
FEATURE [Part::Cylinder] Cylinder025
  Angle = 360
  AttacherType = Attacher::AttachEngine3D
  Height = 10
  Placement = pos=(0,0,36.15) rot=(0,0,1;0rad)
  Radius = 4
FEATURE [Part::MultiFuse] Fusion066  label="removeToCreteHoleForPlugHousing009"
  Placement = pos=(70,19,36) rot=(0,1,0;1.5708rad)
  Shapes = -> [Cylinder024,Cylinder025]
FEATURE [Part::MultiFuse] Fusion065  label="plugHousingBracketHolder002"
  Shapes = -> [Box017,Box015,Box016]
FEATURE [Part::Cut] Cut025  label="plugHousingBracketHolder003"
  Base = -> Fusion065
  Placement = pos=(7,0,0) rot=(0,0,1;0rad)
  Tool = -> Fusion066
FEATURE [Sketcher::SketchObject] Sketch047
  FullyConstrained = false
  Placement = pos=(0,0,0) rot=(1,0,0;1.5708rad)
  sketch-geometry (24):
    g0: ArcOfCircle CenterX=-4 CenterY=-10.5 CenterZ=0 NormalX=0 NormalY=0 NormalZ=1 AngleXU=0 Radius=1.5 StartAngle=6e-16 EndAngle=3.14159
    g1: ArcOfCircle CenterX=-34.2 CenterY=-10.5 CenterZ=0 NormalX=0 NormalY=0 NormalZ=1 AngleXU=0 Radius=1.5 StartAngle=0 EndAngle=3.14159
    g2: ArcOfCircle CenterX=-34.2 CenterY=-27.7 CenterZ=0 NormalX=0 NormalY=0 NormalZ=1 AngleXU=0 Radius=1.5 StartAngle=3.14159 EndAngle=6.28319
    g3: ArcOfCircle CenterX=-4 CenterY=-27.7 CenterZ=0 NormalX=0 NormalY=0 NormalZ=1 AngleXU=0 Radius=1.5 StartAngle=3.1416 EndAngle=6.28319
    g4: ArcOfCircle CenterX=-10 CenterY=-4.3 CenterZ=0 NormalX=0 NormalY=0 NormalZ=1 AngleXU=0 Radius=1.5 StartAngle=2e-16 EndAngle=3.14159
    g5: ArcOfCircle CenterX=-16.1 CenterY=-1.8 CenterZ=0 NormalX=0 NormalY=0 NormalZ=1 AngleXU=0 Radius=1.5 StartAngle=5e-16 EndAngle=3.14159
    g6: ArcOfCircle CenterX=-22.1 CenterY=-1.8 CenterZ=0 NormalX=0 NormalY=0 NormalZ=1 AngleXU=0 Radius=1.5 StartAngle=5e-16 EndAngle=3.14159
    g7: ArcOfCircle CenterX=-28.2 CenterY=-4.3 CenterZ=0 NormalX=0 NormalY=0 NormalZ=1 AngleXU=0 Radius=1.5 StartAngle=2e-16 EndAngle=3.14159
    g8: ArcOfCircle CenterX=-10 CenterY=-33.9 CenterZ=0 NormalX=0 NormalY=0 NormalZ=1 AngleXU=0 Radius=1.5 StartAngle=3.14159 EndAngle=6.28319
    g9: ArcOfCircle CenterX=-16.1 CenterY=-36.4 CenterZ=0 NormalX=0 NormalY=0 NormalZ=1 AngleXU=0 Radius=1.5 StartAngle=3.14159 EndAngle=6.28319
    g10: ArcOfCircle CenterX=-22.1 CenterY=-36.4 CenterZ=0 NormalX=0 NormalY=0 NormalZ=1 AngleXU=0 Radius=1.5 StartAngle=3.14159 EndAngle=6.28319
    g11: ArcOfCircle CenterX=-28.2 CenterY=-33.9 CenterZ=0 NormalX=0 NormalY=0 NormalZ=1 AngleXU=0 Radius=1.5 StartAngle=3.14159 EndAngle=6.28319
    g12: LineSegment StartX=-35.7 StartY=-10.5 StartZ=0 EndX=-35.7 EndY=-27.7 EndZ=0
    g13: LineSegment StartX=-32.7 StartY=-10.5 StartZ=0 EndX=-32.7 EndY=-27.7 EndZ=0
    g14: LineSegment StartX=-29.7 StartY=-33.9 StartZ=0 EndX=-29.7 EndY=-4.3 EndZ=0
    g15: LineSegment StartX=-26.7 StartY=-33.9 StartZ=0 EndX=-26.7 EndY=-4.3 EndZ=0
    g16: LineSegment StartX=-2.5 StartY=-10.5 StartZ=0 EndX=-2.5 EndY=-27.7 EndZ=0
    g17: LineSegment StartX=-8.5 StartY=-4.3 StartZ=0 EndX=-8.5 EndY=-33.9 EndZ=0
    g18: LineSegment StartX=-5.5 StartY=-10.5 StartZ=0 EndX=-5.5 EndY=-27.7 EndZ=0
    g19: LineSegment StartX=-11.5 StartY=-4.3 StartZ=0 EndX=-11.5 EndY=-33.9 EndZ=0
    g20: LineSegment StartX=-14.6 StartY=-1.8 StartZ=0 EndX=-14.6 EndY=-36.4 EndZ=0
    g21: LineSegment StartX=-17.6 StartY=-1.8 StartZ=0 EndX=-17.6 EndY=-36.4 EndZ=0
    g22: LineSegment StartX=-20.6 StartY=-36.4 StartZ=0 EndX=-20.6 EndY=-1.8 EndZ=0
    g23: LineSegment StartX=-23.6 StartY=-1.8 StartZ=0 EndX=-23.6 EndY=-36.4 EndZ=0
  constraints (48):
    c: Block(g0)
    c: Block(g1)
    c: Block(g2)
    c: Block(g3)
    c: Block(g4)
    c: Block(g5)
    c: Block(g6)
    c: Block(g7)
    c: Block(g8)
    c: Block(g9)
    c: Block(g10)
    c: Block(g11)
    c: Coincident(g12,g1)
    c: Coincident(g12,g2)
    c: Vertical(g12)
    c: Coincident(g13,g1)
    c: Coincident(g13,g2)
    c: Vertical(g13)
    c: Coincident(g14,g11)
    c: Coincident(g14,g7)
    c: Vertical(g14)
    c: Coincident(g15,g11)
    c: Coincident(g15,g7)
    c: Vertical(g15)
    c: Coincident(g16,g0)
    c: Coincident(g16,g3)
    c: Vertical(g16)
    c: Coincident(g17,g4)
    c: Coincident(g17,g8)
    c: Vertical(g17)
    c: Coincident(g18,g0)
    c: Coincident(g18,g3)
    c: Vertical(g18)
    c: Coincident(g19,g4)
    c: Coincident(g19,g8)
    c: Vertical(g19)
    c: Coincident(g20,g5)
    c: Coincident(g20,g9)
    c: Vertical(g20)
    c: Coincident(g21,g5)
    c: Coincident(g21,g9)
    c: Vertical(g21)
    c: Coincident(g22,g10)
    c: Coincident(g22,g6)
    c: Vertical(g22)
    c: Coincident(g23,g6)
    c: Coincident(g23,g10)
    c: Vertical(g23)
FEATURE [Part::Extrusion] Extrude038  label="removeToCreateFanGrillHoles001"
  Base = -> Sketch047
  Dir = (0,-1,6e-16)
  DirMode = 2
  FaceMakerClass = Part::FaceMakerBullseye
  LengthFwd = 10
  LengthRev = 0
  Placement = pos=(65.4,44,54.82) rot=(0,0,1;0rad)
  Solid = true
  Symmetric = false
FEATURE [Part::Feature] Wire004
  shape: bbox 11 x 5.2 x 2e-07 mm, 0 faces, 0 solids (baked)
FEATURE [Part::Revolution] Revolve095
  Angle = 360
  Axis = (0,1,0)
  Base = (0,0,0)
  FaceMakerClass = Part::FaceMakerBullseye
  Placement = pos=(30.3,38,19.7) rot=(0,0,1;0rad)
  Solid = true
  Source = -> Wire004
  Symmetric = false
FEATURE [Part::Feature] Wire005
  shape: bbox 11 x 5.2 x 2e-07 mm, 0 faces, 0 solids (baked)
FEATURE [Part::Revolution] Revolve096
  Angle = 360
  Axis = (0,1,0)
  Base = (0,0,0)
  FaceMakerClass = Part::FaceMakerBullseye
  Placement = pos=(30.3,38,51.7) rot=(0,0,1;0rad)
  Solid = true
  Source = -> Wire005
  Symmetric = false
FEATURE [Part::Feature] Wire006
  shape: bbox 11 x 5.2 x 2e-07 mm, 0 faces, 0 solids (baked)
FEATURE [Part::Revolution] Revolve097
  Angle = 360
  Axis = (0,1,0)
  Base = (0,0,0)
  FaceMakerClass = Part::FaceMakerBullseye
  Placement = pos=(62.3,38,51.7) rot=(0,0,1;0rad)
  Solid = true
  Source = -> Wire006
  Symmetric = false
FEATURE [Part::Feature] Wire007
  shape: bbox 11 x 5.2 x 2e-07 mm, 0 faces, 0 solids (baked)
FEATURE [Part::Revolution] Revolve098
  Angle = 360
  Axis = (0,1,0)
  Base = (0,0,0)
  FaceMakerClass = Part::FaceMakerBullseye
  Placement = pos=(62.3,38,19.7) rot=(0,0,1;0rad)
  Solid = true
  Source = -> Wire007
  Symmetric = false
FEATURE [Part::MultiFuse] Fusion067  label="fanScrewHousing002"
  Shapes = -> [Revolve098,Revolve097,Revolve096,Revolve095]
FEATURE [Part::Feature] Face091 .. Face094  x4 (patterned run collapsed; names and placements below)
  shape: bbox 3.5 x 17.8 x 2e-07 mm, 1 faces, 0 solids (baked)
FEATURE [Part::Revolution] Revolve099  label="removeToCreateScrewAndThreadedInsertHole026"
  Angle = 360
  Axis = (0,1,0)
  Base = (0,0,0)
  FaceMakerClass = Part::FaceMakerBullseye
  Placement = pos=(62.3,30.3,19.7) rot=(0,0,1;0rad)
  Solid = false
  Source = -> Face091
  Symmetric = false
FEATURE [Part::Revolution] Revolve100  label="removeToCreateScrewAndThreadedInsertHole027"
  Angle = 360
  Axis = (0,1,0)
  Base = (0,0,0)
  FaceMakerClass = Part::FaceMakerBullseye
  Placement = pos=(62.3,30.3,51.7) rot=(0,0,1;0rad)
  Solid = false
  Source = -> Face092
  Symmetric = false
FEATURE [Part::Revolution] Revolve101  label="removeToCreateScrewAndThreadedInsertHole028"
  Angle = 360
  Axis = (0,1,0)
  Base = (0,0,0)
  FaceMakerClass = Part::FaceMakerBullseye
  Placement = pos=(30.3,30.3,19.7) rot=(0,0,1;0rad)
  Solid = false
  Source = -> Face093
  Symmetric = false
FEATURE [Part::Revolution] Revolve102  label="removeToCreateScrewAndThreadedInsertHole029"
  Angle = 360
  Axis = (0,1,0)
  Base = (0,0,0)
  FaceMakerClass = Part::FaceMakerBullseye
  Placement = pos=(30.3,30.3,51.7) rot=(0,0,1;0rad)
  Solid = false
  Source = -> Face094
  Symmetric = false
FEATURE [Part::MultiFuse] Fusion068  label="createThreadedInsertHolesForFan002"
  Shapes = -> [Revolve099,Revolve100,Revolve101,Revolve102]
FEATURE [Part::Cut] Cut026  label="fanScrewHousing003"
  Base = -> Fusion067
  Tool = -> Fusion068
FEATURE [Sketcher::SketchObject] Sketch048
  FullyConstrained = false
  Placement = pos=(0,0,0) rot=(1,0,0;1.5708rad)
  sketch-geometry (24):
    g0: ArcOfCircle CenterX=-4 CenterY=-10.5 CenterZ=0 NormalX=0 NormalY=0 NormalZ=1 AngleXU=0 Radius=1.5 StartAngle=6e-16 EndAngle=3.14159
    g1: ArcOfCircle CenterX=-34.2 CenterY=-10.5 CenterZ=0 NormalX=0 NormalY=0 NormalZ=1 AngleXU=0 Radius=1.5 StartAngle=0 EndAngle=3.14159
    g2: ArcOfCircle CenterX=-34.2 CenterY=-27.7 CenterZ=0 NormalX=0 NormalY=0 NormalZ=1 AngleXU=0 Radius=1.5 StartAngle=3.14159 EndAngle=6.28319
    g3: ArcOfCircle CenterX=-4 CenterY=-27.7 CenterZ=0 NormalX=0 NormalY=0 NormalZ=1 AngleXU=0 Radius=1.5 StartAngle=3.1416 EndAngle=6.28319
    g4: ArcOfCircle CenterX=-10 CenterY=-4.3 CenterZ=0 NormalX=0 NormalY=0 NormalZ=1 AngleXU=0 Radius=1.5 StartAngle=2e-16 EndAngle=3.14159
    g5: ArcOfCircle CenterX=-16.1 CenterY=-1.8 CenterZ=0 NormalX=0 NormalY=0 NormalZ=1 AngleXU=0 Radius=1.5 StartAngle=5e-16 EndAngle=3.14159
    g6: ArcOfCircle CenterX=-22.1 CenterY=-1.8 CenterZ=0 NormalX=0 NormalY=0 NormalZ=1 AngleXU=0 Radius=1.5 StartAngle=5e-16 EndAngle=3.14159
    g7: ArcOfCircle CenterX=-28.2 CenterY=-4.3 CenterZ=0 NormalX=0 NormalY=0 NormalZ=1 AngleXU=0 Radius=1.5 StartAngle=2e-16 EndAngle=3.14159
    g8: ArcOfCircle CenterX=-10 CenterY=-33.9 CenterZ=0 NormalX=0 NormalY=0 NormalZ=1 AngleXU=0 Radius=1.5 StartAngle=3.14159 EndAngle=6.28319
    g9: ArcOfCircle CenterX=-16.1 CenterY=-36.4 CenterZ=0 NormalX=0 NormalY=0 NormalZ=1 AngleXU=0 Radius=1.5 StartAngle=3.14159 EndAngle=6.28319
    g10: ArcOfCircle CenterX=-22.1 CenterY=-36.4 CenterZ=0 NormalX=0 NormalY=0 NormalZ=1 AngleXU=0 Radius=1.5 StartAngle=3.14159 EndAngle=6.28319
    g11: ArcOfCircle CenterX=-28.2 CenterY=-33.9 CenterZ=0 NormalX=0 NormalY=0 NormalZ=1 AngleXU=0 Radius=1.5 StartAngle=3.14159 EndAngle=6.28319
    g12: LineSegment StartX=-35.7 StartY=-10.5 StartZ=0 EndX=-35.7 EndY=-27.7 EndZ=0
    g13: LineSegment StartX=-32.7 StartY=-10.5 StartZ=0 EndX=-32.7 EndY=-27.7 EndZ=0
    g14: LineSegment StartX=-29.7 StartY=-33.9 StartZ=0 EndX=-29.7 EndY=-4.3 EndZ=0
    g15: LineSegment StartX=-26.7 StartY=-33.9 StartZ=0 EndX=-26.7 EndY=-4.3 EndZ=0
    g16: LineSegment StartX=-2.5 StartY=-10.5 StartZ=0 EndX=-2.5 EndY=-27.7 EndZ=0
    g17: LineSegment StartX=-8.5 StartY=-4.3 StartZ=0 EndX=-8.5 EndY=-33.9 EndZ=0
    g18: LineSegment StartX=-5.5 StartY=-10.5 StartZ=0 EndX=-5.5 EndY=-27.7 EndZ=0
    g19: LineSegment StartX=-11.5 StartY=-4.3 StartZ=0 EndX=-11.5 EndY=-33.9 EndZ=0
    g20: LineSegment StartX=-14.6 StartY=-1.8 StartZ=0 EndX=-14.6 EndY=-36.4 EndZ=0
    g21: LineSegment StartX=-17.6 StartY=-1.8 StartZ=0 EndX=-17.6 EndY=-36.4 EndZ=0
    g22: LineSegment StartX=-20.6 StartY=-36.4 StartZ=0 EndX=-20.6 EndY=-1.8 EndZ=0
    g23: LineSegment StartX=-23.6 StartY=-1.8 StartZ=0 EndX=-23.6 EndY=-36.4 EndZ=0
  constraints (48):
    c: Block(g0)
    c: Block(g1)
    c: Block(g2)
    c: Block(g3)
    c: Block(g4)
    c: Block(g5)
    c: Block(g6)
    c: Block(g7)
    c: Block(g8)
    c: Block(g9)
    c: Block(g10)
    c: Block(g11)
    c: Coincident(g12,g1)
    c: Coincident(g12,g2)
    c: Vertical(g12)
    c: Coincident(g13,g1)
    c: Coincident(g13,g2)
    c: Vertical(g13)
    c: Coincident(g14,g11)
    c: Coincident(g14,g7)
    c: Vertical(g14)
    c: Coincident(g15,g11)
    c: Coincident(g15,g7)
    c: Vertical(g15)
    c: Coincident(g16,g0)
    c: Coincident(g16,g3)
    c: Vertical(g16)
    c: Coincident(g17,g4)
    c: Coincident(g17,g8)
    c: Vertical(g17)
    c: Coincident(g18,g0)
    c: Coincident(g18,g3)
    c: Vertical(g18)
    c: Coincident(g19,g4)
    c: Coincident(g19,g8)
    c: Vertical(g19)
    c: Coincident(g20,g5)
    c: Coincident(g20,g9)
    c: Vertical(g20)
    c: Coincident(g21,g5)
    c: Coincident(g21,g9)
    c: Vertical(g21)
    c: Coincident(g22,g10)
    c: Coincident(g22,g6)
    c: Vertical(g22)
    c: Coincident(g23,g6)
    c: Coincident(g23,g10)
    c: Vertical(g23)
FEATURE [Part::Extrusion] Extrude039  label="removeToCreateFanGrillHoles002"
  Base = -> Sketch048
  Dir = (0,-1,6e-16)
  DirMode = 2
  FaceMakerClass = Part::FaceMakerBullseye
  LengthFwd = 10
  LengthRev = 0
  Placement = pos=(65.4,44,54.82) rot=(0,0,1;0rad)
  Solid = true
  Symmetric = false
FEATURE [Part::Cut] Cut027  label="fanScrewHousing004"
  Base = -> Cut026
  Tool = -> Extrude038
FEATURE [Part::Cut] Cut028  label="top014"
  Base = -> Fillet026
  Tool = -> Extrude039
FEATURE [Part::Feature] Face095 .. Face098  x4 (patterned run collapsed; names and placements below)
  shape: bbox 3.5 x 17.8 x 2e-07 mm, 1 faces, 0 solids (baked)
FEATURE [Part::Revolution] Revolve103  label="removeToCreateScrewAndThreadedInsertHole030"
  Angle = 360
  Axis = (0,1,0)
  Base = (0,0,0)
  FaceMakerClass = Part::FaceMakerBullseye
  Placement = pos=(62.3,30.3,19.7) rot=(0,0,1;0rad)
  Solid = false
  Source = -> Face095
  Symmetric = false
FEATURE [Part::Revolution] Revolve104  label="removeToCreateScrewAndThreadedInsertHole031"
  Angle = 360
  Axis = (0,1,0)
  Base = (0,0,0)
  FaceMakerClass = Part::FaceMakerBullseye
  Placement = pos=(62.3,30.3,51.7) rot=(0,0,1;0rad)
  Solid = false
  Source = -> Face096
  Symmetric = false
FEATURE [Part::Revolution] Revolve105  label="removeToCreateScrewAndThreadedInsertHole032"
  Angle = 360
  Axis = (0,1,0)
  Base = (0,0,0)
  FaceMakerClass = Part::FaceMakerBullseye
  Placement = pos=(30.3,30.3,19.7) rot=(0,0,1;0rad)
  Solid = false
  Source = -> Face097
  Symmetric = false
FEATURE [Part::Revolution] Revolve106  label="removeToCreateScrewAndThreadedInsertHole033"
  Angle = 360
  Axis = (0,1,0)
  Base = (0,0,0)
  FaceMakerClass = Part::FaceMakerBullseye
  Placement = pos=(30.3,30.3,51.7) rot=(0,0,1;0rad)
  Solid = false
  Source = -> Face098
  Symmetric = false
FEATURE [Part::MultiFuse] Fusion069  label="createThreadedInsertHolesForFan003"
  Shapes = -> [Revolve103,Revolve104,Revolve105,Revolve106]
FEATURE [Part::Cut] Cut029  label="top015"
  Base = -> Cut028
  Tool = -> Fusion054
FEATURE [Part::Cut] Cut030  label="fanScrewHousing005"
  Base = -> Cut027
  Tool = -> Fusion069
FEATURE [Part::Cylinder] Cylinder026  label="removeToCreteHoleForPlugHousing010"
  Angle = 360
  AttacherType = Attacher::AttachEngine3D
  Height = 20
  Placement = pos=(-2,19,36) rot=(0,1,0;1.5708rad)
  Radius = 14.3
FEATURE [Part::Box] Box018  label="removeToCreteHoleForPlugHousing011"
  AttacherType = Attacher::AttachEngine3D
  Height = 28.6
  Length = 10
  Placement = pos=(-2,0,21.7) rot=(0,0,1;0rad)
  Width = 19
FEATURE [Part::Box] Box019  label="wireHolderBottomCaseBit"
  AttacherType = Attacher::AttachEngine3D
  Height = 28
  Length = 10
  Placement = pos=(-2,0,22) rot=(0,0,1;0rad)
  Width = 19
FEATURE [Part::Cylinder] Cylinder027  label="removeToCreteHoleForPlugHousing012"
  Angle = 360
  AttacherType = Attacher::AttachEngine3D
  Height = 20
  Placement = pos=(-2,19,36) rot=(0,1,0;1.5708rad)
  Radius = 14.3
FEATURE [Part::Cut] Cut031  label="wireHolderBottomCaseBit001"
  Base = -> Box019
  Tool = -> Cylinder027
FEATURE [Part::MultiFuse] Fusion070  label="removeToCreteHoleForPlugHousing013"
  Shapes = -> [Box018,Cylinder026]
